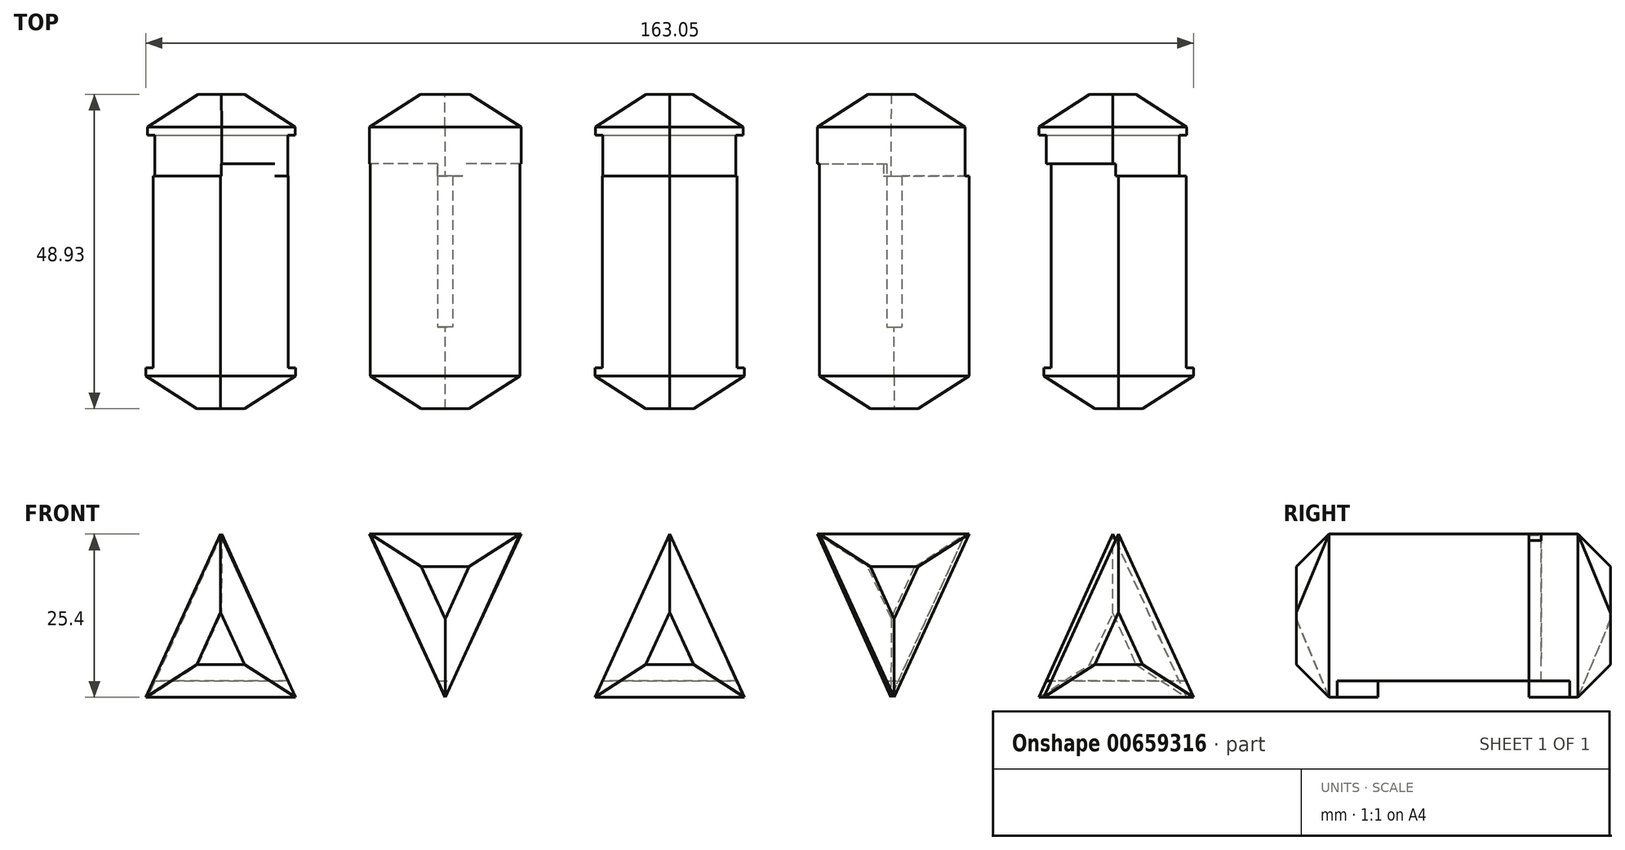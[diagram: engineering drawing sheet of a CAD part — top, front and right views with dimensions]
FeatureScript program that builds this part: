
annotation { "Feature Type Name" : "Feature", "Feature Type Description" : "" }
export const myFeature = defineFeature(function(context is Context, id is Id, definition is map)
    precondition{}
    {
        {
            var Q0;
            Q0=qCreatedBy(makeId("Top.planeOp"),FACE);
            var sketch = newSketch(context, id + "F0", { "sketchPlane" : qUnion([Q0])});
            skLineSegment(sketch, "E0.bottom", {"start": v(-40.34, -18.56) * mm, "end": v(39.23, -18.56) * mm});
            skLineSegment(sketch, "E0.top", {"start": v(-40.34, 17.67) * mm, "end": v(39.23, 17.67) * mm});
            skLineSegment(sketch, "E0.left", {"start": v(-40.34, -18.56) * mm, "end": v(-40.34, 17.67) * mm});
            skLineSegment(sketch, "E0.right", {"start": v(39.23, -18.56) * mm, "end": v(39.23, 17.67) * mm});
            skSolve(sketch);
        }
        {
            var Q0;
            Q0=makeQuery(id+"F0.imprint","IMPRINT",FACE,{"disambiguationData":[TD([[makeQuery(id+"F0.imprint","IMPRINT",EDGE,{"derivedFrom":sQuery(id+"F0.wireOp",EDGE,"E0.bottom")}),1.0]])]});
            extrude(context, id + "F1", {"entities" : qUnion([Q0]), "depth" : 12.7 * mm, "offsetDistance" : 25.4 * mm});
        }
        {
            var Q0;
            Q0=makeQuery(id+"F1.opExtrude","CAP_FACE",FACE,{"disambiguationData":[OSD([sQuery(id+"F0.wireOp",EDGE,"E0.bottom"),sQuery(id+"F0.wireOp",EDGE,"E0.top"),sQuery(id+"F0.wireOp",EDGE,"E0.left"),sQuery(id+"F0.wireOp",EDGE,"E0.right")])],"isStart":true});
            extrude(context, id + "F2", {"entities" : qUnion([Q0]), "operationType" : NewBodyOperationType.ADD, "depth" : 12.7 * mm, "offsetDistance" : 25.4 * mm});
        }
        {
            var Q0;
            {var subQ0=sQuery(id+"F0.wireOp",EDGE,"E0.left");Q0=makeQuery(id+"F2.boolean.opBoolean","MERGE",FACE,{"derivedFrom":[makeQuery(id+"F1.opExtrude","SWEPT_FACE",FACE,{"disambiguationData":[OSD([subQ0])]}),makeQuery(id+"F2.opExtrude","SWEPT_FACE",FACE,{"disambiguationData":[OSD([subQ0])]})]});}
            extrude(context, id + "F3", {"entities" : qUnion([Q0]), "operationType" : NewBodyOperationType.ADD, "depth" : 50.8 * mm, "offsetDistance" : 25.4 * mm});
        }
        {
            var Q0;
            {var subQ0=sQuery(id+"F0.wireOp",EDGE,"E0.right");Q0=makeQuery(id+"F2.boolean.opBoolean","MERGE",FACE,{"derivedFrom":[makeQuery(id+"F1.opExtrude","SWEPT_FACE",FACE,{"disambiguationData":[OSD([subQ0])]}),makeQuery(id+"F2.opExtrude","SWEPT_FACE",FACE,{"disambiguationData":[OSD([subQ0])]})]});}
            extrude(context, id + "F4", {"entities" : qUnion([Q0]), "operationType" : NewBodyOperationType.ADD, "depth" : 50.8 * mm, "offsetDistance" : 25.4 * mm});
        }
        {
            var Q0;
            {var subQ0=sQuery(id+"F0.wireOp",EDGE,"E0.bottom");Q0=makeQuery(id+"F4.boolean.opBoolean","MERGE",FACE,{"derivedFrom":[makeQuery(id+"F3.boolean.opBoolean","MERGE",FACE,{"derivedFrom":[makeQuery(id+"F2.boolean.opBoolean","MERGE",FACE,{"derivedFrom":[makeQuery(id+"F1.opExtrude","SWEPT_FACE",FACE,{"disambiguationData":[OSD([subQ0])]}),makeQuery(id+"F2.opExtrude","SWEPT_FACE",FACE,{"disambiguationData":[OSD([subQ0])]})]}),makeQuery(id+"F3.opExtrude","SWEPT_FACE",FACE,{"disambiguationData":[OSD([subQ0,sQuery(id+"F0.wireOp",EDGE,"E0.left")])]})]}),makeQuery(id+"F4.opExtrude","SWEPT_FACE",FACE,{"disambiguationData":[OSD([subQ0,sQuery(id+"F0.wireOp",EDGE,"E0.right")])]})]});}
            var sketch = newSketch(context, id + "F5", { "sketchPlane" : qUnion([Q0])});
            skLineSegment(sketch, "E1", {"start": v(-0.56, 12.7) * mm, "end": v(11.1, -12.7) * mm});
            skLineSegment(sketch, "E2", {"start": v(-0.56, 12.7) * mm, "end": v(-12.2, -12.7) * mm});
            skLineSegment(sketch, "E3", {"start": v(-12.2, -12.7) * mm, "end": v(-23.85, 12.7) * mm});
            skLineSegment(sketch, "E4", {"start": v(-23.85, 12.7) * mm, "end": v(-35.5, -12.7) * mm});
            skLineSegment(sketch, "E5", {"start": v(11.1, -12.7) * mm, "end": v(22.74, 12.7) * mm});
            skLineSegment(sketch, "E6", {"start": v(22.74, 12.7) * mm, "end": v(34.39, -12.7) * mm});
            skLineSegment(sketch, "E7", {"start": v(34.39, -12.7) * mm, "end": v(46.03, 12.7) * mm});
            skLineSegment(sketch, "E8", {"start": v(46.03, 12.7) * mm, "end": v(57.68, -12.7) * mm});
            skLineSegment(sketch, "E9", {"start": v(57.68, -12.7) * mm, "end": v(69.32, 12.7) * mm});
            skLineSegment(sketch, "E10", {"start": v(69.32, 12.7) * mm, "end": v(80.97, -12.7) * mm});
            skLineSegment(sketch, "E11", {"start": v(80.97, -12.7) * mm, "end": v(90.03, 7.05) * mm});
            skLineSegment(sketch, "E12", {"start": v(-35.5, -12.7) * mm, "end": v(-47.14, 12.7) * mm});
            skLineSegment(sketch, "E13", {"start": v(-47.14, 12.7) * mm, "end": v(-58.79, -12.7) * mm});
            skLineSegment(sketch, "E14", {"start": v(-58.79, -12.7) * mm, "end": v(-70.44, 12.7) * mm});
            skLineSegment(sketch, "E15", {"start": v(-70.44, 12.7) * mm, "end": v(-82.08, -12.7) * mm});
            skLineSegment(sketch, "E16", {"start": v(-82.08, -12.7) * mm, "end": v(-91.14, 7.05) * mm});
            skSolve(sketch);
        }
        {
            var Q0;
            {var subQ0=sQuery(id+"F0.wireOp",EDGE,"E0.top");Q0=makeQuery(id+"F4.boolean.opBoolean","MERGE",FACE,{"derivedFrom":[makeQuery(id+"F3.boolean.opBoolean","MERGE",FACE,{"derivedFrom":[makeQuery(id+"F2.boolean.opBoolean","MERGE",FACE,{"derivedFrom":[makeQuery(id+"F1.opExtrude","SWEPT_FACE",FACE,{"disambiguationData":[OSD([subQ0])]}),makeQuery(id+"F2.opExtrude","SWEPT_FACE",FACE,{"disambiguationData":[OSD([subQ0])]})]}),makeQuery(id+"F3.opExtrude","SWEPT_FACE",FACE,{"disambiguationData":[OSD([subQ0,sQuery(id+"F0.wireOp",EDGE,"E0.left")])]})]}),makeQuery(id+"F4.opExtrude","SWEPT_FACE",FACE,{"disambiguationData":[OSD([subQ0,sQuery(id+"F0.wireOp",EDGE,"E0.right")])]})]});}
            var sketch = newSketch(context, id + "F6", { "sketchPlane" : qUnion([Q0])});
            skLineSegment(sketch, "E17", {"start": v(0.56, 12.7) * mm, "end": v(12.1, -12.7) * mm});
            skLineSegment(sketch, "E18", {"start": v(12.1, -12.7) * mm, "end": v(23.69, 12.7) * mm});
            skLineSegment(sketch, "E19", {"start": v(23.69, 12.7) * mm, "end": v(35.54, -12.7) * mm});
            skLineSegment(sketch, "E20", {"start": v(35.54, -12.7) * mm, "end": v(47.26, 12.7) * mm});
            skLineSegment(sketch, "E21", {"start": v(47.26, 12.7) * mm, "end": v(58.85, -12.7) * mm});
            skLineSegment(sketch, "E22", {"start": v(58.85, -12.7) * mm, "end": v(70.3, 12.7) * mm});
            skLineSegment(sketch, "E23", {"start": v(70.3, 12.7) * mm, "end": v(81.84, -12.7) * mm});
            skLineSegment(sketch, "E24", {"start": v(81.84, -12.7) * mm, "end": v(91.14, 7.45) * mm});
            skLineSegment(sketch, "E25", {"start": v(0.56, 12.7) * mm, "end": v(-10.9, -12.7) * mm});
            skLineSegment(sketch, "E26", {"start": v(-10.9, -12.7) * mm, "end": v(-22.44, 12.7) * mm});
            skLineSegment(sketch, "E27", {"start": v(-22.44, 12.7) * mm, "end": v(-33.89, -12.7) * mm});
            skLineSegment(sketch, "E28", {"start": v(-33.89, -12.7) * mm, "end": v(-45.44, 12.7) * mm});
            skLineSegment(sketch, "E29", {"start": v(-45.44, 12.7) * mm, "end": v(-56.89, -12.7) * mm});
            skLineSegment(sketch, "E30", {"start": v(-56.89, -12.7) * mm, "end": v(-68.44, 12.7) * mm});
            skLineSegment(sketch, "E31", {"start": v(-68.44, 12.7) * mm, "end": v(-79.88, -12.7) * mm});
            skLineSegment(sketch, "E32", {"start": v(-79.88, -12.7) * mm, "end": v(-90.03, 6.92) * mm});
            skSolve(sketch);
        }
        {
            var Q0;
            {var subQ0=sQuery(id+"F5.wireOp",EDGE,"E1");Q0=makeQuery(id+"F5.imprint","IMPRINT",FACE,{"disambiguationData":[TD([[makeQuery(id+"F5.imprint","IMPRINT",EDGE,{"derivedFrom":subQ0}),-1.0]])]});}
            var Q1;
            {var subQ0=sQuery(id+"F5.wireOp",EDGE,"E6");Q1=makeQuery(id+"F5.imprint","IMPRINT",FACE,{"disambiguationData":[TD([[makeQuery(id+"F5.imprint","IMPRINT",EDGE,{"derivedFrom":subQ0}),1.0]])]});}
            var Q2;
            {var subQ0=sQuery(id+"F5.wireOp",EDGE,"E9");Q2=makeQuery(id+"F5.imprint","IMPRINT",FACE,{"disambiguationData":[TD([[makeQuery(id+"F5.imprint","IMPRINT",EDGE,{"derivedFrom":subQ0}),-1.0]])]});}
            var Q3;
            {var subQ0=sQuery(id+"F5.wireOp",EDGE,"E4");Q3=makeQuery(id+"F5.imprint","IMPRINT",FACE,{"disambiguationData":[TD([[makeQuery(id+"F5.imprint","IMPRINT",EDGE,{"derivedFrom":subQ0}),-1.0]])]});}
            var Q4;
            {var subQ0=sQuery(id+"F5.wireOp",EDGE,"E14");Q4=makeQuery(id+"F5.imprint","IMPRINT",FACE,{"disambiguationData":[TD([[makeQuery(id+"F5.imprint","IMPRINT",EDGE,{"derivedFrom":subQ0}),1.0]])]});}
            extrude(context, id + "F7", {"entities" : qUnion([Q0, Q1, Q2, Q3, Q4]), "operationType" : NewBodyOperationType.ADD, "depth" : 6.35 * mm, "offsetDistance" : 25.4 * mm});
        }
        {
            var Q0;
            Q0=makeQuery(id+"F7.opExtrude","CAP_FACE",FACE,{"disambiguationData":[OSD([sQuery(id+"F0.wireOp",EDGE,"E0.bottom"),sQuery(id+"F0.wireOp",EDGE,"E0.left"),sQuery(id+"F0.wireOp",EDGE,"E0.right"),sQuery(id+"F5.wireOp",EDGE,"E14"),sQuery(id+"F5.wireOp",EDGE,"E15")])],"isStart":false});
            var Q1;
            Q1=makeQuery(id+"F7.opExtrude","CAP_FACE",FACE,{"disambiguationData":[OSD([sQuery(id+"F0.wireOp",EDGE,"E0.bottom"),sQuery(id+"F0.wireOp",EDGE,"E0.left"),sQuery(id+"F0.wireOp",EDGE,"E0.right"),sQuery(id+"F5.wireOp",EDGE,"E4"),sQuery(id+"F5.wireOp",EDGE,"E12")])],"isStart":false});
            var Q2;
            Q2=makeQuery(id+"F7.opExtrude","CAP_FACE",FACE,{"disambiguationData":[OSD([sQuery(id+"F0.wireOp",EDGE,"E0.bottom"),sQuery(id+"F0.wireOp",EDGE,"E0.left"),sQuery(id+"F0.wireOp",EDGE,"E0.right"),sQuery(id+"F5.wireOp",EDGE,"E1"),sQuery(id+"F5.wireOp",EDGE,"E2")])],"isStart":false});
            var Q3;
            Q3=makeQuery(id+"F7.opExtrude","CAP_FACE",FACE,{"disambiguationData":[OSD([sQuery(id+"F0.wireOp",EDGE,"E0.bottom"),sQuery(id+"F0.wireOp",EDGE,"E0.left"),sQuery(id+"F0.wireOp",EDGE,"E0.right"),sQuery(id+"F5.wireOp",EDGE,"E6"),sQuery(id+"F5.wireOp",EDGE,"E7")])],"isStart":false});
            var Q4;
            Q4=makeQuery(id+"F7.opExtrude","CAP_FACE",FACE,{"disambiguationData":[OSD([sQuery(id+"F0.wireOp",EDGE,"E0.bottom"),sQuery(id+"F0.wireOp",EDGE,"E0.left"),sQuery(id+"F0.wireOp",EDGE,"E0.right"),sQuery(id+"F5.wireOp",EDGE,"E9"),sQuery(id+"F5.wireOp",EDGE,"E10")])],"isStart":false});
            chamfer(context, id + "F8", {"entities" : qUnion([Q0, Q1, Q2, Q3, Q4]), "width" : 5.08 * mm, "tangentPropagation" : true});
        }
        {
            var Q0;
            {var subQ0=sQuery(id+"F6.wireOp",EDGE,"E17");Q0=makeQuery(id+"F6.imprint","IMPRINT",FACE,{"disambiguationData":[TD([[makeQuery(id+"F6.imprint","IMPRINT",EDGE,{"derivedFrom":subQ0}),-1.0]])]});}
            var Q1;
            {var subQ0=sQuery(id+"F6.wireOp",EDGE,"E19");Q1=makeQuery(id+"F6.imprint","IMPRINT",FACE,{"disambiguationData":[TD([[makeQuery(id+"F6.imprint","IMPRINT",EDGE,{"derivedFrom":subQ0}),1.0]])]});}
            var Q2;
            {var subQ0=sQuery(id+"F6.wireOp",EDGE,"E22");Q2=makeQuery(id+"F6.imprint","IMPRINT",FACE,{"disambiguationData":[TD([[makeQuery(id+"F6.imprint","IMPRINT",EDGE,{"derivedFrom":subQ0}),-1.0]])]});}
            var Q3;
            {var subQ0=sQuery(id+"F6.wireOp",EDGE,"E27");Q3=makeQuery(id+"F6.imprint","IMPRINT",FACE,{"disambiguationData":[TD([[makeQuery(id+"F6.imprint","IMPRINT",EDGE,{"derivedFrom":subQ0}),-1.0]])]});}
            var Q4;
            {var subQ0=sQuery(id+"F6.wireOp",EDGE,"E30");Q4=makeQuery(id+"F6.imprint","IMPRINT",FACE,{"disambiguationData":[TD([[makeQuery(id+"F6.imprint","IMPRINT",EDGE,{"derivedFrom":subQ0}),1.0]])]});}
            extrude(context, id + "F9", {"entities" : qUnion([Q0, Q1, Q2, Q3, Q4]), "operationType" : NewBodyOperationType.ADD, "depth" : 6.35 * mm, "offsetDistance" : 25.4 * mm});
        }
        {
            var Q0;
            Q0=makeQuery(id+"F9.opExtrude","CAP_FACE",FACE,{"disambiguationData":[OSD([sQuery(id+"F0.wireOp",EDGE,"E0.top"),sQuery(id+"F0.wireOp",EDGE,"E0.left"),sQuery(id+"F0.wireOp",EDGE,"E0.right"),sQuery(id+"F6.wireOp",EDGE,"E30"),sQuery(id+"F6.wireOp",EDGE,"E31")])],"isStart":false});
            var Q1;
            Q1=makeQuery(id+"F9.opExtrude","CAP_FACE",FACE,{"disambiguationData":[OSD([sQuery(id+"F0.wireOp",EDGE,"E0.top"),sQuery(id+"F0.wireOp",EDGE,"E0.left"),sQuery(id+"F0.wireOp",EDGE,"E0.right"),sQuery(id+"F6.wireOp",EDGE,"E27"),sQuery(id+"F6.wireOp",EDGE,"E28")])],"isStart":false});
            var Q2;
            Q2=makeQuery(id+"F9.opExtrude","CAP_FACE",FACE,{"disambiguationData":[OSD([sQuery(id+"F0.wireOp",EDGE,"E0.top"),sQuery(id+"F0.wireOp",EDGE,"E0.left"),sQuery(id+"F0.wireOp",EDGE,"E0.right"),sQuery(id+"F6.wireOp",EDGE,"E17"),sQuery(id+"F6.wireOp",EDGE,"E25")])],"isStart":false});
            var Q3;
            Q3=makeQuery(id+"F9.opExtrude","CAP_FACE",FACE,{"disambiguationData":[OSD([sQuery(id+"F0.wireOp",EDGE,"E0.top"),sQuery(id+"F0.wireOp",EDGE,"E0.left"),sQuery(id+"F0.wireOp",EDGE,"E0.right"),sQuery(id+"F6.wireOp",EDGE,"E19"),sQuery(id+"F6.wireOp",EDGE,"E20")])],"isStart":false});
            var Q4;
            Q4=makeQuery(id+"F9.opExtrude","CAP_FACE",FACE,{"disambiguationData":[OSD([sQuery(id+"F0.wireOp",EDGE,"E0.top"),sQuery(id+"F0.wireOp",EDGE,"E0.left"),sQuery(id+"F0.wireOp",EDGE,"E0.right"),sQuery(id+"F6.wireOp",EDGE,"E22"),sQuery(id+"F6.wireOp",EDGE,"E23")])],"isStart":false});
            chamfer(context, id + "F10", {"entities" : qUnion([Q0, Q1, Q2, Q3, Q4]), "width" : 5.08 * mm, "tangentPropagation" : true});
        }
        {
            var Q0;
            {var subQ0=sQuery(id+"F0.wireOp",EDGE,"E0.right");var subQ1=sQuery(id+"F0.wireOp",EDGE,"E0.left");var subQ2=sQuery(id+"F0.wireOp",EDGE,"E0.bottom");var subQ3=makeQuery(id+"F3.opExtrude","SWEPT_FACE",FACE,{"disambiguationData":[OSD([subQ2,subQ1])]});var subQ4=sQuery(id+"F5.wireOp",EDGE,"E5");var subQ5=sQuery(id+"F5.wireOp",EDGE,"E1");var subQ6=makeQuery(id+"F4.boolean.opBoolean","MERGE",EDGE,{"derivedFrom":[makeQuery(id+"F3.boolean.opBoolean","MERGE",EDGE,{"derivedFrom":[makeQuery(id+"F2.opExtrude","CAP_EDGE",EDGE,{"disambiguationData":[OSD([subQ2])],"isStart":false}),makeQuery(id+"F3.opExtrude","SWEPT_EDGE",EDGE,{"disambiguationData":[OSD([subQ2,subQ1]),TDD([makeQuery(id+"F2.opExtrude","CAP_VERTEX",VERTEX,{"disambiguationData":[OSD([subQ2,subQ1])],"isStart":false})])]})]}),makeQuery(id+"F4.opExtrude","SWEPT_EDGE",EDGE,{"disambiguationData":[OSD([subQ2,subQ0]),TDD([makeQuery(id+"F2.opExtrude","CAP_VERTEX",VERTEX,{"disambiguationData":[OSD([subQ2,subQ0])],"isStart":false})])]})]});var subQ7=sQuery(id+"F5.wireOp",EDGE,"E3");var subQ8=sQuery(id+"F5.wireOp",EDGE,"E2");var subQ9=makeQuery(id+"F4.boolean.opBoolean","MERGE",EDGE,{"derivedFrom":[makeQuery(id+"F3.boolean.opBoolean","MERGE",EDGE,{"derivedFrom":[makeQuery(id+"F1.opExtrude","CAP_EDGE",EDGE,{"disambiguationData":[OSD([subQ2])],"isStart":false}),makeQuery(id+"F3.opExtrude","SWEPT_EDGE",EDGE,{"disambiguationData":[OSD([subQ2,subQ1]),TDD([makeQuery(id+"F1.opExtrude","CAP_VERTEX",VERTEX,{"disambiguationData":[OSD([subQ2,subQ1])],"isStart":false})])]})]}),makeQuery(id+"F4.opExtrude","SWEPT_EDGE",EDGE,{"disambiguationData":[OSD([subQ2,subQ0]),TDD([makeQuery(id+"F1.opExtrude","CAP_VERTEX",VERTEX,{"disambiguationData":[OSD([subQ2,subQ0])],"isStart":false})])]})]});var subQ10=sQuery(id+"F5.wireOp",EDGE,"E13");var subQ11=sQuery(id+"F5.wireOp",EDGE,"E6");var subQ12=sQuery(id+"F5.wireOp",EDGE,"E8");var subQ13=sQuery(id+"F5.wireOp",EDGE,"E7");var subQ14=makeQuery(id+"F1.opExtrude","SWEPT_FACE",FACE,{"disambiguationData":[OSD([subQ2])]});var subQ15=makeQuery(id+"F4.opExtrude","SWEPT_FACE",FACE,{"disambiguationData":[OSD([subQ2,subQ0])]});var subQ16=sQuery(id+"F0.wireOp",EDGE,"E0.top");var subQ17=makeQuery(id+"F2.opExtrude","SWEPT_FACE",FACE,{"disambiguationData":[OSD([subQ2])]});Q0=makeQuery(id+"F7.boolean.opBoolean","SPLIT",FACE,{"disambiguationData":[TD([subQ14,makeQuery(id+"F1.opExtrude","CAP_FACE",FACE,{"disambiguationData":[OSD([subQ2,subQ16,subQ1,subQ0])],"isStart":false}),subQ17,makeQuery(id+"F2.opExtrude","CAP_FACE",FACE,{"disambiguationData":[OSD([subQ2,subQ16,subQ1,subQ0])],"isStart":false}),makeQuery(id+"F3.opExtrude","SWEPT_FACE",FACE,{"disambiguationData":[OSD([subQ1]),TDD([makeQuery(id+"F1.opExtrude","CAP_EDGE",EDGE,{"disambiguationData":[OSD([subQ1])],"isStart":false})])]}),makeQuery(id+"F3.opExtrude","SWEPT_FACE",FACE,{"disambiguationData":[OSD([subQ1]),TDD([makeQuery(id+"F2.opExtrude","CAP_EDGE",EDGE,{"disambiguationData":[OSD([subQ1])],"isStart":false})])]}),subQ3,makeQuery(id+"F4.opExtrude","SWEPT_FACE",FACE,{"disambiguationData":[OSD([subQ0]),TDD([makeQuery(id+"F1.opExtrude","CAP_EDGE",EDGE,{"disambiguationData":[OSD([subQ0])],"isStart":false})])]}),makeQuery(id+"F4.opExtrude","SWEPT_FACE",FACE,{"disambiguationData":[OSD([subQ0]),TDD([makeQuery(id+"F2.opExtrude","CAP_EDGE",EDGE,{"disambiguationData":[OSD([subQ0])],"isStart":false})])]}),subQ15,makeQuery(id+"F7.opExtrude","SWEPT_FACE",FACE,{"disambiguationData":[OSD([subQ5])]}),makeQuery(id+"F7.opExtrude","SWEPT_FACE",FACE,{"disambiguationData":[OSD([subQ8])]}),makeQuery(id+"F7.opExtrude","SWEPT_FACE",FACE,{"disambiguationData":[OSD([subQ11])]}),makeQuery(id+"F7.opExtrude","SWEPT_FACE",FACE,{"disambiguationData":[OSD([subQ13])]}),makeQuery(id+"F7.opExtrude","SWEPT_FACE",FACE,{"disambiguationData":[OSD([subQ2,subQ1,subQ0]),TDD([makeQuery(id+"F5.imprint","IMPRINT",EDGE,{"disambiguationData":[TD([[makeQuery(id+"F5.imprint","INTERSECT",VERTEX,{"derivedFrom":[subQ9,subQ7,sQuery(id+"F5.wireOp",EDGE,"E4")]}),1.0]])],"derivedFrom":subQ9})])]}),makeQuery(id+"F7.opExtrude","SWEPT_FACE",FACE,{"disambiguationData":[OSD([subQ2,subQ1,subQ0]),TDD([makeQuery(id+"F5.imprint","IMPRINT",EDGE,{"disambiguationData":[TD([[makeQuery(id+"F5.imprint","INTERSECT",VERTEX,{"derivedFrom":[subQ9,subQ4,subQ11]}),-1.0]])],"derivedFrom":subQ9})])]}),makeQuery(id+"F7.opExtrude","SWEPT_FACE",FACE,{"disambiguationData":[OSD([subQ2,subQ1,subQ0]),TDD([makeQuery(id+"F5.imprint","IMPRINT",EDGE,{"disambiguationData":[TD([[makeQuery(id+"F5.imprint","INTERSECT",VERTEX,{"derivedFrom":[subQ6,subQ5,subQ4]}),1.0]])],"derivedFrom":subQ6})])]}),makeQuery(id+"F7.opExtrude","SWEPT_FACE",FACE,{"disambiguationData":[OSD([subQ2,subQ1,subQ0]),TDD([makeQuery(id+"F5.imprint","IMPRINT",EDGE,{"disambiguationData":[TD([[makeQuery(id+"F5.imprint","INTERSECT",VERTEX,{"derivedFrom":[subQ6,subQ12,sQuery(id+"F5.wireOp",EDGE,"E9")]}),-1.0]])],"derivedFrom":subQ6})])]}),makeQuery(id+"F7.opExtrude","SWEPT_FACE",FACE,{"disambiguationData":[OSD([subQ2,subQ1,subQ0]),TDD([makeQuery(id+"F5.imprint","IMPRINT",EDGE,{"disambiguationData":[TD([[makeQuery(id+"F5.imprint","INTERSECT",VERTEX,{"derivedFrom":[subQ6,subQ10,sQuery(id+"F5.wireOp",EDGE,"E14")]}),1.0]])],"derivedFrom":subQ6})])]})])],"derivedFrom":makeQuery(id+"F4.boolean.opBoolean","MERGE",FACE,{"derivedFrom":[makeQuery(id+"F3.boolean.opBoolean","MERGE",FACE,{"derivedFrom":[makeQuery(id+"F2.boolean.opBoolean","MERGE",FACE,{"derivedFrom":[subQ14,subQ17]}),subQ3]}),subQ15]})});}
            var Q1;
            {var subQ0=sQuery(id+"F0.wireOp",EDGE,"E0.right");var subQ1=sQuery(id+"F0.wireOp",EDGE,"E0.left");var subQ2=sQuery(id+"F0.wireOp",EDGE,"E0.bottom");var subQ3=makeQuery(id+"F3.opExtrude","SWEPT_FACE",FACE,{"disambiguationData":[OSD([subQ2,subQ1])]});var subQ4=sQuery(id+"F5.wireOp",EDGE,"E5");var subQ5=makeQuery(id+"F4.boolean.opBoolean","MERGE",EDGE,{"derivedFrom":[makeQuery(id+"F3.boolean.opBoolean","MERGE",EDGE,{"derivedFrom":[makeQuery(id+"F2.opExtrude","CAP_EDGE",EDGE,{"disambiguationData":[OSD([subQ2])],"isStart":false}),makeQuery(id+"F3.opExtrude","SWEPT_EDGE",EDGE,{"disambiguationData":[OSD([subQ2,subQ1]),TDD([makeQuery(id+"F2.opExtrude","CAP_VERTEX",VERTEX,{"disambiguationData":[OSD([subQ2,subQ1])],"isStart":false})])]})]}),makeQuery(id+"F4.opExtrude","SWEPT_EDGE",EDGE,{"disambiguationData":[OSD([subQ2,subQ0]),TDD([makeQuery(id+"F2.opExtrude","CAP_VERTEX",VERTEX,{"disambiguationData":[OSD([subQ2,subQ0])],"isStart":false})])]})]});var subQ6=sQuery(id+"F5.wireOp",EDGE,"E3");var subQ7=makeQuery(id+"F4.boolean.opBoolean","MERGE",EDGE,{"derivedFrom":[makeQuery(id+"F3.boolean.opBoolean","MERGE",EDGE,{"derivedFrom":[makeQuery(id+"F1.opExtrude","CAP_EDGE",EDGE,{"disambiguationData":[OSD([subQ2])],"isStart":false}),makeQuery(id+"F3.opExtrude","SWEPT_EDGE",EDGE,{"disambiguationData":[OSD([subQ2,subQ1]),TDD([makeQuery(id+"F1.opExtrude","CAP_VERTEX",VERTEX,{"disambiguationData":[OSD([subQ2,subQ1])],"isStart":false})])]})]}),makeQuery(id+"F4.opExtrude","SWEPT_EDGE",EDGE,{"disambiguationData":[OSD([subQ2,subQ0]),TDD([makeQuery(id+"F1.opExtrude","CAP_VERTEX",VERTEX,{"disambiguationData":[OSD([subQ2,subQ0])],"isStart":false})])]})]});var subQ8=sQuery(id+"F5.wireOp",EDGE,"E13");var subQ9=sQuery(id+"F5.wireOp",EDGE,"E6");var subQ10=sQuery(id+"F5.wireOp",EDGE,"E8");var subQ11=sQuery(id+"F5.wireOp",EDGE,"E7");var subQ12=makeQuery(id+"F1.opExtrude","SWEPT_FACE",FACE,{"disambiguationData":[OSD([subQ2])]});var subQ13=makeQuery(id+"F4.opExtrude","SWEPT_FACE",FACE,{"disambiguationData":[OSD([subQ2,subQ0])]});var subQ14=sQuery(id+"F0.wireOp",EDGE,"E0.top");var subQ15=makeQuery(id+"F2.opExtrude","SWEPT_FACE",FACE,{"disambiguationData":[OSD([subQ2])]});var subQ16=sQuery(id+"F5.wireOp",EDGE,"E9");var subQ17=sQuery(id+"F5.wireOp",EDGE,"E10");Q1=makeQuery(id+"F7.boolean.opBoolean","SPLIT",FACE,{"disambiguationData":[TD([subQ12,makeQuery(id+"F1.opExtrude","CAP_FACE",FACE,{"disambiguationData":[OSD([subQ2,subQ14,subQ1,subQ0])],"isStart":false}),subQ15,makeQuery(id+"F2.opExtrude","CAP_FACE",FACE,{"disambiguationData":[OSD([subQ2,subQ14,subQ1,subQ0])],"isStart":false}),makeQuery(id+"F3.opExtrude","SWEPT_FACE",FACE,{"disambiguationData":[OSD([subQ1]),TDD([makeQuery(id+"F1.opExtrude","CAP_EDGE",EDGE,{"disambiguationData":[OSD([subQ1])],"isStart":false})])]}),makeQuery(id+"F3.opExtrude","SWEPT_FACE",FACE,{"disambiguationData":[OSD([subQ1]),TDD([makeQuery(id+"F2.opExtrude","CAP_EDGE",EDGE,{"disambiguationData":[OSD([subQ1])],"isStart":false})])]}),subQ3,makeQuery(id+"F4.opExtrude","SWEPT_FACE",FACE,{"disambiguationData":[OSD([subQ0]),TDD([makeQuery(id+"F1.opExtrude","CAP_EDGE",EDGE,{"disambiguationData":[OSD([subQ0])],"isStart":false})])]}),makeQuery(id+"F4.opExtrude","SWEPT_FACE",FACE,{"disambiguationData":[OSD([subQ0]),TDD([makeQuery(id+"F2.opExtrude","CAP_EDGE",EDGE,{"disambiguationData":[OSD([subQ0])],"isStart":false})])]}),subQ13,makeQuery(id+"F7.opExtrude","SWEPT_FACE",FACE,{"disambiguationData":[OSD([subQ9])]}),makeQuery(id+"F7.opExtrude","SWEPT_FACE",FACE,{"disambiguationData":[OSD([subQ11])]}),makeQuery(id+"F7.opExtrude","SWEPT_FACE",FACE,{"disambiguationData":[OSD([subQ16])]}),makeQuery(id+"F7.opExtrude","SWEPT_FACE",FACE,{"disambiguationData":[OSD([subQ17])]}),makeQuery(id+"F7.opExtrude","SWEPT_FACE",FACE,{"disambiguationData":[OSD([subQ2,subQ1,subQ0]),TDD([makeQuery(id+"F5.imprint","IMPRINT",EDGE,{"disambiguationData":[TD([[makeQuery(id+"F5.imprint","INTERSECT",VERTEX,{"derivedFrom":[subQ7,subQ6,sQuery(id+"F5.wireOp",EDGE,"E4")]}),1.0]])],"derivedFrom":subQ7})])]}),makeQuery(id+"F7.opExtrude","SWEPT_FACE",FACE,{"disambiguationData":[OSD([subQ2,subQ1,subQ0]),TDD([makeQuery(id+"F5.imprint","IMPRINT",EDGE,{"disambiguationData":[TD([[makeQuery(id+"F5.imprint","INTERSECT",VERTEX,{"derivedFrom":[subQ7,subQ4,subQ9]}),-1.0]])],"derivedFrom":subQ7})])]}),makeQuery(id+"F7.opExtrude","SWEPT_FACE",FACE,{"disambiguationData":[OSD([subQ2,subQ1,subQ0]),TDD([makeQuery(id+"F5.imprint","IMPRINT",EDGE,{"disambiguationData":[TD([[makeQuery(id+"F5.imprint","INTERSECT",VERTEX,{"derivedFrom":[subQ5,sQuery(id+"F5.wireOp",EDGE,"E1"),subQ4]}),1.0]])],"derivedFrom":subQ5})])]}),makeQuery(id+"F7.opExtrude","SWEPT_FACE",FACE,{"disambiguationData":[OSD([subQ2,subQ1,subQ0]),TDD([makeQuery(id+"F5.imprint","IMPRINT",EDGE,{"disambiguationData":[TD([[makeQuery(id+"F5.imprint","INTERSECT",VERTEX,{"derivedFrom":[subQ5,subQ10,subQ16]}),-1.0]])],"derivedFrom":subQ5})])]}),makeQuery(id+"F7.opExtrude","SWEPT_FACE",FACE,{"disambiguationData":[OSD([subQ2,subQ1,subQ0]),TDD([makeQuery(id+"F5.imprint","IMPRINT",EDGE,{"disambiguationData":[TD([[makeQuery(id+"F5.imprint","INTERSECT",VERTEX,{"derivedFrom":[subQ5,subQ8,sQuery(id+"F5.wireOp",EDGE,"E14")]}),1.0]])],"derivedFrom":subQ5})])]})])],"derivedFrom":makeQuery(id+"F4.boolean.opBoolean","MERGE",FACE,{"derivedFrom":[makeQuery(id+"F3.boolean.opBoolean","MERGE",FACE,{"derivedFrom":[makeQuery(id+"F2.boolean.opBoolean","MERGE",FACE,{"derivedFrom":[subQ12,subQ15]}),subQ3]}),subQ13]})});}
            var Q2;
            {var subQ0=sQuery(id+"F0.wireOp",EDGE,"E0.right");var subQ1=sQuery(id+"F0.wireOp",EDGE,"E0.left");var subQ2=sQuery(id+"F0.wireOp",EDGE,"E0.bottom");var subQ3=makeQuery(id+"F3.opExtrude","SWEPT_FACE",FACE,{"disambiguationData":[OSD([subQ2,subQ1])]});var subQ4=sQuery(id+"F5.wireOp",EDGE,"E5");var subQ5=makeQuery(id+"F4.boolean.opBoolean","MERGE",EDGE,{"derivedFrom":[makeQuery(id+"F3.boolean.opBoolean","MERGE",EDGE,{"derivedFrom":[makeQuery(id+"F2.opExtrude","CAP_EDGE",EDGE,{"disambiguationData":[OSD([subQ2])],"isStart":false}),makeQuery(id+"F3.opExtrude","SWEPT_EDGE",EDGE,{"disambiguationData":[OSD([subQ2,subQ1]),TDD([makeQuery(id+"F2.opExtrude","CAP_VERTEX",VERTEX,{"disambiguationData":[OSD([subQ2,subQ1])],"isStart":false})])]})]}),makeQuery(id+"F4.opExtrude","SWEPT_EDGE",EDGE,{"disambiguationData":[OSD([subQ2,subQ0]),TDD([makeQuery(id+"F2.opExtrude","CAP_VERTEX",VERTEX,{"disambiguationData":[OSD([subQ2,subQ0])],"isStart":false})])]})]});var subQ6=sQuery(id+"F5.wireOp",EDGE,"E3");var subQ7=makeQuery(id+"F4.boolean.opBoolean","MERGE",EDGE,{"derivedFrom":[makeQuery(id+"F3.boolean.opBoolean","MERGE",EDGE,{"derivedFrom":[makeQuery(id+"F1.opExtrude","CAP_EDGE",EDGE,{"disambiguationData":[OSD([subQ2])],"isStart":false}),makeQuery(id+"F3.opExtrude","SWEPT_EDGE",EDGE,{"disambiguationData":[OSD([subQ2,subQ1]),TDD([makeQuery(id+"F1.opExtrude","CAP_VERTEX",VERTEX,{"disambiguationData":[OSD([subQ2,subQ1])],"isStart":false})])]})]}),makeQuery(id+"F4.opExtrude","SWEPT_EDGE",EDGE,{"disambiguationData":[OSD([subQ2,subQ0]),TDD([makeQuery(id+"F1.opExtrude","CAP_VERTEX",VERTEX,{"disambiguationData":[OSD([subQ2,subQ0])],"isStart":false})])]})]});var subQ8=sQuery(id+"F5.wireOp",EDGE,"E13");var subQ9=sQuery(id+"F5.wireOp",EDGE,"E8");var subQ10=makeQuery(id+"F1.opExtrude","SWEPT_FACE",FACE,{"disambiguationData":[OSD([subQ2])]});var subQ11=makeQuery(id+"F4.opExtrude","SWEPT_FACE",FACE,{"disambiguationData":[OSD([subQ2,subQ0])]});var subQ12=sQuery(id+"F0.wireOp",EDGE,"E0.top");var subQ13=makeQuery(id+"F2.opExtrude","SWEPT_FACE",FACE,{"disambiguationData":[OSD([subQ2])]});var subQ14=sQuery(id+"F5.wireOp",EDGE,"E9");var subQ15=sQuery(id+"F5.wireOp",EDGE,"E10");Q2=makeQuery(id+"F7.boolean.opBoolean","SPLIT",FACE,{"disambiguationData":[TD([subQ10,makeQuery(id+"F1.opExtrude","CAP_FACE",FACE,{"disambiguationData":[OSD([subQ2,subQ12,subQ1,subQ0])],"isStart":false}),subQ13,makeQuery(id+"F2.opExtrude","CAP_FACE",FACE,{"disambiguationData":[OSD([subQ2,subQ12,subQ1,subQ0])],"isStart":false}),makeQuery(id+"F3.opExtrude","SWEPT_FACE",FACE,{"disambiguationData":[OSD([subQ1]),TDD([makeQuery(id+"F1.opExtrude","CAP_EDGE",EDGE,{"disambiguationData":[OSD([subQ1])],"isStart":false})])]}),makeQuery(id+"F3.opExtrude","SWEPT_FACE",FACE,{"disambiguationData":[OSD([subQ1]),TDD([makeQuery(id+"F2.opExtrude","CAP_EDGE",EDGE,{"disambiguationData":[OSD([subQ1])],"isStart":false})])]}),subQ3,makeQuery(id+"F4.opExtrude","SWEPT_FACE",FACE,{"disambiguationData":[OSD([subQ0]),TDD([makeQuery(id+"F1.opExtrude","CAP_EDGE",EDGE,{"disambiguationData":[OSD([subQ0])],"isStart":false})])]}),makeQuery(id+"F4.opExtrude","SWEPT_FACE",FACE,{"disambiguationData":[OSD([subQ0]),TDD([makeQuery(id+"F2.opExtrude","CAP_EDGE",EDGE,{"disambiguationData":[OSD([subQ0])],"isStart":false})])]}),subQ11,makeQuery(id+"F4.opExtrude","CAP_FACE",FACE,{"disambiguationData":[OSD([subQ0])],"isStart":false}),makeQuery(id+"F7.opExtrude","SWEPT_FACE",FACE,{"disambiguationData":[OSD([subQ14])]}),makeQuery(id+"F7.opExtrude","SWEPT_FACE",FACE,{"disambiguationData":[OSD([subQ15])]}),makeQuery(id+"F7.opExtrude","SWEPT_FACE",FACE,{"disambiguationData":[OSD([subQ2,subQ1,subQ0]),TDD([makeQuery(id+"F5.imprint","IMPRINT",EDGE,{"disambiguationData":[TD([[makeQuery(id+"F5.imprint","INTERSECT",VERTEX,{"derivedFrom":[subQ7,subQ6,sQuery(id+"F5.wireOp",EDGE,"E4")]}),1.0]])],"derivedFrom":subQ7})])]}),makeQuery(id+"F7.opExtrude","SWEPT_FACE",FACE,{"disambiguationData":[OSD([subQ2,subQ1,subQ0]),TDD([makeQuery(id+"F5.imprint","IMPRINT",EDGE,{"disambiguationData":[TD([[makeQuery(id+"F5.imprint","INTERSECT",VERTEX,{"derivedFrom":[subQ7,subQ4,sQuery(id+"F5.wireOp",EDGE,"E6")]}),-1.0]])],"derivedFrom":subQ7})])]}),makeQuery(id+"F7.opExtrude","SWEPT_FACE",FACE,{"disambiguationData":[OSD([subQ2,subQ1,subQ0]),TDD([makeQuery(id+"F5.imprint","IMPRINT",EDGE,{"disambiguationData":[TD([[makeQuery(id+"F5.imprint","INTERSECT",VERTEX,{"derivedFrom":[subQ5,sQuery(id+"F5.wireOp",EDGE,"E1"),subQ4]}),1.0]])],"derivedFrom":subQ5})])]}),makeQuery(id+"F7.opExtrude","SWEPT_FACE",FACE,{"disambiguationData":[OSD([subQ2,subQ1,subQ0]),TDD([makeQuery(id+"F5.imprint","IMPRINT",EDGE,{"disambiguationData":[TD([[makeQuery(id+"F5.imprint","INTERSECT",VERTEX,{"derivedFrom":[subQ5,subQ9,subQ14]}),-1.0]])],"derivedFrom":subQ5})])]}),makeQuery(id+"F7.opExtrude","SWEPT_FACE",FACE,{"disambiguationData":[OSD([subQ2,subQ1,subQ0]),TDD([makeQuery(id+"F5.imprint","IMPRINT",EDGE,{"disambiguationData":[TD([[makeQuery(id+"F5.imprint","INTERSECT",VERTEX,{"derivedFrom":[subQ5,subQ8,sQuery(id+"F5.wireOp",EDGE,"E14")]}),1.0]])],"derivedFrom":subQ5})])]})])],"derivedFrom":makeQuery(id+"F4.boolean.opBoolean","MERGE",FACE,{"derivedFrom":[makeQuery(id+"F3.boolean.opBoolean","MERGE",FACE,{"derivedFrom":[makeQuery(id+"F2.boolean.opBoolean","MERGE",FACE,{"derivedFrom":[subQ10,subQ13]}),subQ3]}),subQ11]})});}
            var Q3;
            {var subQ0=sQuery(id+"F0.wireOp",EDGE,"E0.right");var subQ1=sQuery(id+"F5.wireOp",EDGE,"E12");var subQ2=sQuery(id+"F0.wireOp",EDGE,"E0.left");var subQ3=sQuery(id+"F0.wireOp",EDGE,"E0.bottom");var subQ4=makeQuery(id+"F3.opExtrude","SWEPT_FACE",FACE,{"disambiguationData":[OSD([subQ3,subQ2])]});var subQ5=sQuery(id+"F5.wireOp",EDGE,"E5");var subQ6=sQuery(id+"F5.wireOp",EDGE,"E1");var subQ7=makeQuery(id+"F4.boolean.opBoolean","MERGE",EDGE,{"derivedFrom":[makeQuery(id+"F3.boolean.opBoolean","MERGE",EDGE,{"derivedFrom":[makeQuery(id+"F2.opExtrude","CAP_EDGE",EDGE,{"disambiguationData":[OSD([subQ3])],"isStart":false}),makeQuery(id+"F3.opExtrude","SWEPT_EDGE",EDGE,{"disambiguationData":[OSD([subQ3,subQ2]),TDD([makeQuery(id+"F2.opExtrude","CAP_VERTEX",VERTEX,{"disambiguationData":[OSD([subQ3,subQ2])],"isStart":false})])]})]}),makeQuery(id+"F4.opExtrude","SWEPT_EDGE",EDGE,{"disambiguationData":[OSD([subQ3,subQ0]),TDD([makeQuery(id+"F2.opExtrude","CAP_VERTEX",VERTEX,{"disambiguationData":[OSD([subQ3,subQ0])],"isStart":false})])]})]});var subQ8=sQuery(id+"F5.wireOp",EDGE,"E3");var subQ9=sQuery(id+"F5.wireOp",EDGE,"E2");var subQ10=sQuery(id+"F5.wireOp",EDGE,"E4");var subQ11=makeQuery(id+"F4.boolean.opBoolean","MERGE",EDGE,{"derivedFrom":[makeQuery(id+"F3.boolean.opBoolean","MERGE",EDGE,{"derivedFrom":[makeQuery(id+"F1.opExtrude","CAP_EDGE",EDGE,{"disambiguationData":[OSD([subQ3])],"isStart":false}),makeQuery(id+"F3.opExtrude","SWEPT_EDGE",EDGE,{"disambiguationData":[OSD([subQ3,subQ2]),TDD([makeQuery(id+"F1.opExtrude","CAP_VERTEX",VERTEX,{"disambiguationData":[OSD([subQ3,subQ2])],"isStart":false})])]})]}),makeQuery(id+"F4.opExtrude","SWEPT_EDGE",EDGE,{"disambiguationData":[OSD([subQ3,subQ0]),TDD([makeQuery(id+"F1.opExtrude","CAP_VERTEX",VERTEX,{"disambiguationData":[OSD([subQ3,subQ0])],"isStart":false})])]})]});var subQ12=sQuery(id+"F5.wireOp",EDGE,"E13");var subQ13=sQuery(id+"F5.wireOp",EDGE,"E8");var subQ14=makeQuery(id+"F1.opExtrude","SWEPT_FACE",FACE,{"disambiguationData":[OSD([subQ3])]});var subQ15=makeQuery(id+"F4.opExtrude","SWEPT_FACE",FACE,{"disambiguationData":[OSD([subQ3,subQ0])]});var subQ16=sQuery(id+"F0.wireOp",EDGE,"E0.top");var subQ17=makeQuery(id+"F2.opExtrude","SWEPT_FACE",FACE,{"disambiguationData":[OSD([subQ3])]});Q3=makeQuery(id+"F7.boolean.opBoolean","SPLIT",FACE,{"disambiguationData":[TD([subQ14,makeQuery(id+"F1.opExtrude","CAP_FACE",FACE,{"disambiguationData":[OSD([subQ3,subQ16,subQ2,subQ0])],"isStart":false}),subQ17,makeQuery(id+"F2.opExtrude","CAP_FACE",FACE,{"disambiguationData":[OSD([subQ3,subQ16,subQ2,subQ0])],"isStart":false}),makeQuery(id+"F3.opExtrude","SWEPT_FACE",FACE,{"disambiguationData":[OSD([subQ2]),TDD([makeQuery(id+"F1.opExtrude","CAP_EDGE",EDGE,{"disambiguationData":[OSD([subQ2])],"isStart":false})])]}),makeQuery(id+"F3.opExtrude","SWEPT_FACE",FACE,{"disambiguationData":[OSD([subQ2]),TDD([makeQuery(id+"F2.opExtrude","CAP_EDGE",EDGE,{"disambiguationData":[OSD([subQ2])],"isStart":false})])]}),subQ4,makeQuery(id+"F4.opExtrude","SWEPT_FACE",FACE,{"disambiguationData":[OSD([subQ0]),TDD([makeQuery(id+"F1.opExtrude","CAP_EDGE",EDGE,{"disambiguationData":[OSD([subQ0])],"isStart":false})])]}),makeQuery(id+"F4.opExtrude","SWEPT_FACE",FACE,{"disambiguationData":[OSD([subQ0]),TDD([makeQuery(id+"F2.opExtrude","CAP_EDGE",EDGE,{"disambiguationData":[OSD([subQ0])],"isStart":false})])]}),subQ15,makeQuery(id+"F7.opExtrude","SWEPT_FACE",FACE,{"disambiguationData":[OSD([subQ6])]}),makeQuery(id+"F7.opExtrude","SWEPT_FACE",FACE,{"disambiguationData":[OSD([subQ9])]}),makeQuery(id+"F7.opExtrude","SWEPT_FACE",FACE,{"disambiguationData":[OSD([subQ10])]}),makeQuery(id+"F7.opExtrude","SWEPT_FACE",FACE,{"disambiguationData":[OSD([subQ1])]}),makeQuery(id+"F7.opExtrude","SWEPT_FACE",FACE,{"disambiguationData":[OSD([subQ3,subQ2,subQ0]),TDD([makeQuery(id+"F5.imprint","IMPRINT",EDGE,{"disambiguationData":[TD([[makeQuery(id+"F5.imprint","INTERSECT",VERTEX,{"derivedFrom":[subQ11,subQ8,subQ10]}),1.0]])],"derivedFrom":subQ11})])]}),makeQuery(id+"F7.opExtrude","SWEPT_FACE",FACE,{"disambiguationData":[OSD([subQ3,subQ2,subQ0]),TDD([makeQuery(id+"F5.imprint","IMPRINT",EDGE,{"disambiguationData":[TD([[makeQuery(id+"F5.imprint","INTERSECT",VERTEX,{"derivedFrom":[subQ11,subQ5,sQuery(id+"F5.wireOp",EDGE,"E6")]}),-1.0]])],"derivedFrom":subQ11})])]}),makeQuery(id+"F7.opExtrude","SWEPT_FACE",FACE,{"disambiguationData":[OSD([subQ3,subQ2,subQ0]),TDD([makeQuery(id+"F5.imprint","IMPRINT",EDGE,{"disambiguationData":[TD([[makeQuery(id+"F5.imprint","INTERSECT",VERTEX,{"derivedFrom":[subQ7,subQ6,subQ5]}),1.0]])],"derivedFrom":subQ7})])]}),makeQuery(id+"F7.opExtrude","SWEPT_FACE",FACE,{"disambiguationData":[OSD([subQ3,subQ2,subQ0]),TDD([makeQuery(id+"F5.imprint","IMPRINT",EDGE,{"disambiguationData":[TD([[makeQuery(id+"F5.imprint","INTERSECT",VERTEX,{"derivedFrom":[subQ7,subQ13,sQuery(id+"F5.wireOp",EDGE,"E9")]}),-1.0]])],"derivedFrom":subQ7})])]}),makeQuery(id+"F7.opExtrude","SWEPT_FACE",FACE,{"disambiguationData":[OSD([subQ3,subQ2,subQ0]),TDD([makeQuery(id+"F5.imprint","IMPRINT",EDGE,{"disambiguationData":[TD([[makeQuery(id+"F5.imprint","INTERSECT",VERTEX,{"derivedFrom":[subQ7,subQ12,sQuery(id+"F5.wireOp",EDGE,"E14")]}),1.0]])],"derivedFrom":subQ7})])]})])],"derivedFrom":makeQuery(id+"F4.boolean.opBoolean","MERGE",FACE,{"derivedFrom":[makeQuery(id+"F3.boolean.opBoolean","MERGE",FACE,{"derivedFrom":[makeQuery(id+"F2.boolean.opBoolean","MERGE",FACE,{"derivedFrom":[subQ14,subQ17]}),subQ4]}),subQ15]})});}
            var Q4;
            {var subQ0=sQuery(id+"F0.wireOp",EDGE,"E0.right");var subQ1=sQuery(id+"F5.wireOp",EDGE,"E14");var subQ2=sQuery(id+"F5.wireOp",EDGE,"E12");var subQ3=sQuery(id+"F0.wireOp",EDGE,"E0.left");var subQ4=sQuery(id+"F0.wireOp",EDGE,"E0.bottom");var subQ5=makeQuery(id+"F3.opExtrude","SWEPT_FACE",FACE,{"disambiguationData":[OSD([subQ4,subQ3])]});var subQ6=sQuery(id+"F5.wireOp",EDGE,"E5");var subQ7=makeQuery(id+"F4.boolean.opBoolean","MERGE",EDGE,{"derivedFrom":[makeQuery(id+"F3.boolean.opBoolean","MERGE",EDGE,{"derivedFrom":[makeQuery(id+"F2.opExtrude","CAP_EDGE",EDGE,{"disambiguationData":[OSD([subQ4])],"isStart":false}),makeQuery(id+"F3.opExtrude","SWEPT_EDGE",EDGE,{"disambiguationData":[OSD([subQ4,subQ3]),TDD([makeQuery(id+"F2.opExtrude","CAP_VERTEX",VERTEX,{"disambiguationData":[OSD([subQ4,subQ3])],"isStart":false})])]})]}),makeQuery(id+"F4.opExtrude","SWEPT_EDGE",EDGE,{"disambiguationData":[OSD([subQ4,subQ0]),TDD([makeQuery(id+"F2.opExtrude","CAP_VERTEX",VERTEX,{"disambiguationData":[OSD([subQ4,subQ0])],"isStart":false})])]})]});var subQ8=sQuery(id+"F5.wireOp",EDGE,"E3");var subQ9=sQuery(id+"F5.wireOp",EDGE,"E4");var subQ10=makeQuery(id+"F4.boolean.opBoolean","MERGE",EDGE,{"derivedFrom":[makeQuery(id+"F3.boolean.opBoolean","MERGE",EDGE,{"derivedFrom":[makeQuery(id+"F1.opExtrude","CAP_EDGE",EDGE,{"disambiguationData":[OSD([subQ4])],"isStart":false}),makeQuery(id+"F3.opExtrude","SWEPT_EDGE",EDGE,{"disambiguationData":[OSD([subQ4,subQ3]),TDD([makeQuery(id+"F1.opExtrude","CAP_VERTEX",VERTEX,{"disambiguationData":[OSD([subQ4,subQ3])],"isStart":false})])]})]}),makeQuery(id+"F4.opExtrude","SWEPT_EDGE",EDGE,{"disambiguationData":[OSD([subQ4,subQ0]),TDD([makeQuery(id+"F1.opExtrude","CAP_VERTEX",VERTEX,{"disambiguationData":[OSD([subQ4,subQ0])],"isStart":false})])]})]});var subQ11=sQuery(id+"F5.wireOp",EDGE,"E13");var subQ12=sQuery(id+"F5.wireOp",EDGE,"E8");var subQ13=makeQuery(id+"F1.opExtrude","SWEPT_FACE",FACE,{"disambiguationData":[OSD([subQ4])]});var subQ14=makeQuery(id+"F4.opExtrude","SWEPT_FACE",FACE,{"disambiguationData":[OSD([subQ4,subQ0])]});var subQ15=sQuery(id+"F0.wireOp",EDGE,"E0.top");var subQ16=sQuery(id+"F5.wireOp",EDGE,"E15");var subQ17=makeQuery(id+"F2.opExtrude","SWEPT_FACE",FACE,{"disambiguationData":[OSD([subQ4])]});Q4=makeQuery(id+"F7.boolean.opBoolean","SPLIT",FACE,{"disambiguationData":[TD([subQ13,makeQuery(id+"F1.opExtrude","CAP_FACE",FACE,{"disambiguationData":[OSD([subQ4,subQ15,subQ3,subQ0])],"isStart":false}),subQ17,makeQuery(id+"F2.opExtrude","CAP_FACE",FACE,{"disambiguationData":[OSD([subQ4,subQ15,subQ3,subQ0])],"isStart":false}),makeQuery(id+"F3.opExtrude","SWEPT_FACE",FACE,{"disambiguationData":[OSD([subQ3]),TDD([makeQuery(id+"F1.opExtrude","CAP_EDGE",EDGE,{"disambiguationData":[OSD([subQ3])],"isStart":false})])]}),makeQuery(id+"F3.opExtrude","SWEPT_FACE",FACE,{"disambiguationData":[OSD([subQ3]),TDD([makeQuery(id+"F2.opExtrude","CAP_EDGE",EDGE,{"disambiguationData":[OSD([subQ3])],"isStart":false})])]}),subQ5,makeQuery(id+"F4.opExtrude","SWEPT_FACE",FACE,{"disambiguationData":[OSD([subQ0]),TDD([makeQuery(id+"F1.opExtrude","CAP_EDGE",EDGE,{"disambiguationData":[OSD([subQ0])],"isStart":false})])]}),makeQuery(id+"F4.opExtrude","SWEPT_FACE",FACE,{"disambiguationData":[OSD([subQ0]),TDD([makeQuery(id+"F2.opExtrude","CAP_EDGE",EDGE,{"disambiguationData":[OSD([subQ0])],"isStart":false})])]}),subQ14,makeQuery(id+"F7.opExtrude","SWEPT_FACE",FACE,{"disambiguationData":[OSD([subQ9])]}),makeQuery(id+"F7.opExtrude","SWEPT_FACE",FACE,{"disambiguationData":[OSD([subQ2])]}),makeQuery(id+"F7.opExtrude","SWEPT_FACE",FACE,{"disambiguationData":[OSD([subQ1])]}),makeQuery(id+"F7.opExtrude","SWEPT_FACE",FACE,{"disambiguationData":[OSD([subQ16])]}),makeQuery(id+"F7.opExtrude","SWEPT_FACE",FACE,{"disambiguationData":[OSD([subQ4,subQ3,subQ0]),TDD([makeQuery(id+"F5.imprint","IMPRINT",EDGE,{"disambiguationData":[TD([[makeQuery(id+"F5.imprint","INTERSECT",VERTEX,{"derivedFrom":[subQ10,subQ8,subQ9]}),1.0]])],"derivedFrom":subQ10})])]}),makeQuery(id+"F7.opExtrude","SWEPT_FACE",FACE,{"disambiguationData":[OSD([subQ4,subQ3,subQ0]),TDD([makeQuery(id+"F5.imprint","IMPRINT",EDGE,{"disambiguationData":[TD([[makeQuery(id+"F5.imprint","INTERSECT",VERTEX,{"derivedFrom":[subQ10,subQ6,sQuery(id+"F5.wireOp",EDGE,"E6")]}),-1.0]])],"derivedFrom":subQ10})])]}),makeQuery(id+"F7.opExtrude","SWEPT_FACE",FACE,{"disambiguationData":[OSD([subQ4,subQ3,subQ0]),TDD([makeQuery(id+"F5.imprint","IMPRINT",EDGE,{"disambiguationData":[TD([[makeQuery(id+"F5.imprint","INTERSECT",VERTEX,{"derivedFrom":[subQ7,sQuery(id+"F5.wireOp",EDGE,"E1"),subQ6]}),1.0]])],"derivedFrom":subQ7})])]}),makeQuery(id+"F7.opExtrude","SWEPT_FACE",FACE,{"disambiguationData":[OSD([subQ4,subQ3,subQ0]),TDD([makeQuery(id+"F5.imprint","IMPRINT",EDGE,{"disambiguationData":[TD([[makeQuery(id+"F5.imprint","INTERSECT",VERTEX,{"derivedFrom":[subQ7,subQ12,sQuery(id+"F5.wireOp",EDGE,"E9")]}),-1.0]])],"derivedFrom":subQ7})])]}),makeQuery(id+"F7.opExtrude","SWEPT_FACE",FACE,{"disambiguationData":[OSD([subQ4,subQ3,subQ0]),TDD([makeQuery(id+"F5.imprint","IMPRINT",EDGE,{"disambiguationData":[TD([[makeQuery(id+"F5.imprint","INTERSECT",VERTEX,{"derivedFrom":[subQ7,subQ11,subQ1]}),1.0]])],"derivedFrom":subQ7})])]})])],"derivedFrom":makeQuery(id+"F4.boolean.opBoolean","MERGE",FACE,{"derivedFrom":[makeQuery(id+"F3.boolean.opBoolean","MERGE",FACE,{"derivedFrom":[makeQuery(id+"F2.boolean.opBoolean","MERGE",FACE,{"derivedFrom":[subQ13,subQ17]}),subQ5]}),subQ14]})});}
            var Q5;
            {var subQ0=sQuery(id+"F0.wireOp",EDGE,"E0.right");var subQ1=sQuery(id+"F5.wireOp",EDGE,"E14");var subQ2=sQuery(id+"F0.wireOp",EDGE,"E0.left");var subQ3=sQuery(id+"F0.wireOp",EDGE,"E0.bottom");var subQ4=makeQuery(id+"F3.opExtrude","SWEPT_FACE",FACE,{"disambiguationData":[OSD([subQ3,subQ2])]});var subQ5=sQuery(id+"F5.wireOp",EDGE,"E5");var subQ6=makeQuery(id+"F4.boolean.opBoolean","MERGE",EDGE,{"derivedFrom":[makeQuery(id+"F3.boolean.opBoolean","MERGE",EDGE,{"derivedFrom":[makeQuery(id+"F2.opExtrude","CAP_EDGE",EDGE,{"disambiguationData":[OSD([subQ3])],"isStart":false}),makeQuery(id+"F3.opExtrude","SWEPT_EDGE",EDGE,{"disambiguationData":[OSD([subQ3,subQ2]),TDD([makeQuery(id+"F2.opExtrude","CAP_VERTEX",VERTEX,{"disambiguationData":[OSD([subQ3,subQ2])],"isStart":false})])]})]}),makeQuery(id+"F4.opExtrude","SWEPT_EDGE",EDGE,{"disambiguationData":[OSD([subQ3,subQ0]),TDD([makeQuery(id+"F2.opExtrude","CAP_VERTEX",VERTEX,{"disambiguationData":[OSD([subQ3,subQ0])],"isStart":false})])]})]});var subQ7=sQuery(id+"F5.wireOp",EDGE,"E3");var subQ8=makeQuery(id+"F4.boolean.opBoolean","MERGE",EDGE,{"derivedFrom":[makeQuery(id+"F3.boolean.opBoolean","MERGE",EDGE,{"derivedFrom":[makeQuery(id+"F1.opExtrude","CAP_EDGE",EDGE,{"disambiguationData":[OSD([subQ3])],"isStart":false}),makeQuery(id+"F3.opExtrude","SWEPT_EDGE",EDGE,{"disambiguationData":[OSD([subQ3,subQ2]),TDD([makeQuery(id+"F1.opExtrude","CAP_VERTEX",VERTEX,{"disambiguationData":[OSD([subQ3,subQ2])],"isStart":false})])]})]}),makeQuery(id+"F4.opExtrude","SWEPT_EDGE",EDGE,{"disambiguationData":[OSD([subQ3,subQ0]),TDD([makeQuery(id+"F1.opExtrude","CAP_VERTEX",VERTEX,{"disambiguationData":[OSD([subQ3,subQ0])],"isStart":false})])]})]});var subQ9=sQuery(id+"F5.wireOp",EDGE,"E13");var subQ10=sQuery(id+"F5.wireOp",EDGE,"E8");var subQ11=makeQuery(id+"F1.opExtrude","SWEPT_FACE",FACE,{"disambiguationData":[OSD([subQ3])]});var subQ12=makeQuery(id+"F4.opExtrude","SWEPT_FACE",FACE,{"disambiguationData":[OSD([subQ3,subQ0])]});var subQ13=sQuery(id+"F0.wireOp",EDGE,"E0.top");var subQ14=sQuery(id+"F5.wireOp",EDGE,"E15");var subQ15=makeQuery(id+"F2.opExtrude","SWEPT_FACE",FACE,{"disambiguationData":[OSD([subQ3])]});Q5=makeQuery(id+"F7.boolean.opBoolean","SPLIT",FACE,{"disambiguationData":[TD([subQ11,makeQuery(id+"F1.opExtrude","CAP_FACE",FACE,{"disambiguationData":[OSD([subQ3,subQ13,subQ2,subQ0])],"isStart":false}),subQ15,makeQuery(id+"F2.opExtrude","CAP_FACE",FACE,{"disambiguationData":[OSD([subQ3,subQ13,subQ2,subQ0])],"isStart":false}),makeQuery(id+"F3.opExtrude","SWEPT_FACE",FACE,{"disambiguationData":[OSD([subQ2]),TDD([makeQuery(id+"F1.opExtrude","CAP_EDGE",EDGE,{"disambiguationData":[OSD([subQ2])],"isStart":false})])]}),makeQuery(id+"F3.opExtrude","SWEPT_FACE",FACE,{"disambiguationData":[OSD([subQ2]),TDD([makeQuery(id+"F2.opExtrude","CAP_EDGE",EDGE,{"disambiguationData":[OSD([subQ2])],"isStart":false})])]}),subQ4,makeQuery(id+"F3.opExtrude","CAP_FACE",FACE,{"disambiguationData":[OSD([subQ2])],"isStart":false}),makeQuery(id+"F4.opExtrude","SWEPT_FACE",FACE,{"disambiguationData":[OSD([subQ0]),TDD([makeQuery(id+"F1.opExtrude","CAP_EDGE",EDGE,{"disambiguationData":[OSD([subQ0])],"isStart":false})])]}),makeQuery(id+"F4.opExtrude","SWEPT_FACE",FACE,{"disambiguationData":[OSD([subQ0]),TDD([makeQuery(id+"F2.opExtrude","CAP_EDGE",EDGE,{"disambiguationData":[OSD([subQ0])],"isStart":false})])]}),subQ12,makeQuery(id+"F7.opExtrude","SWEPT_FACE",FACE,{"disambiguationData":[OSD([subQ1])]}),makeQuery(id+"F7.opExtrude","SWEPT_FACE",FACE,{"disambiguationData":[OSD([subQ14])]}),makeQuery(id+"F7.opExtrude","SWEPT_FACE",FACE,{"disambiguationData":[OSD([subQ3,subQ2,subQ0]),TDD([makeQuery(id+"F5.imprint","IMPRINT",EDGE,{"disambiguationData":[TD([[makeQuery(id+"F5.imprint","INTERSECT",VERTEX,{"derivedFrom":[subQ8,subQ7,sQuery(id+"F5.wireOp",EDGE,"E4")]}),1.0]])],"derivedFrom":subQ8})])]}),makeQuery(id+"F7.opExtrude","SWEPT_FACE",FACE,{"disambiguationData":[OSD([subQ3,subQ2,subQ0]),TDD([makeQuery(id+"F5.imprint","IMPRINT",EDGE,{"disambiguationData":[TD([[makeQuery(id+"F5.imprint","INTERSECT",VERTEX,{"derivedFrom":[subQ8,subQ5,sQuery(id+"F5.wireOp",EDGE,"E6")]}),-1.0]])],"derivedFrom":subQ8})])]}),makeQuery(id+"F7.opExtrude","SWEPT_FACE",FACE,{"disambiguationData":[OSD([subQ3,subQ2,subQ0]),TDD([makeQuery(id+"F5.imprint","IMPRINT",EDGE,{"disambiguationData":[TD([[makeQuery(id+"F5.imprint","INTERSECT",VERTEX,{"derivedFrom":[subQ6,sQuery(id+"F5.wireOp",EDGE,"E1"),subQ5]}),1.0]])],"derivedFrom":subQ6})])]}),makeQuery(id+"F7.opExtrude","SWEPT_FACE",FACE,{"disambiguationData":[OSD([subQ3,subQ2,subQ0]),TDD([makeQuery(id+"F5.imprint","IMPRINT",EDGE,{"disambiguationData":[TD([[makeQuery(id+"F5.imprint","INTERSECT",VERTEX,{"derivedFrom":[subQ6,subQ10,sQuery(id+"F5.wireOp",EDGE,"E9")]}),-1.0]])],"derivedFrom":subQ6})])]}),makeQuery(id+"F7.opExtrude","SWEPT_FACE",FACE,{"disambiguationData":[OSD([subQ3,subQ2,subQ0]),TDD([makeQuery(id+"F5.imprint","IMPRINT",EDGE,{"disambiguationData":[TD([[makeQuery(id+"F5.imprint","INTERSECT",VERTEX,{"derivedFrom":[subQ6,subQ9,subQ1]}),1.0]])],"derivedFrom":subQ6})])]})])],"derivedFrom":makeQuery(id+"F4.boolean.opBoolean","MERGE",FACE,{"derivedFrom":[makeQuery(id+"F3.boolean.opBoolean","MERGE",FACE,{"derivedFrom":[makeQuery(id+"F2.boolean.opBoolean","MERGE",FACE,{"derivedFrom":[subQ11,subQ15]}),subQ4]}),subQ12]})});}
            var Q6;
            {var subQ0=sQuery(id+"F6.wireOp",EDGE,"E18");var subQ1=sQuery(id+"F0.wireOp",EDGE,"E0.right");var subQ2=sQuery(id+"F0.wireOp",EDGE,"E0.top");var subQ3=sQuery(id+"F0.wireOp",EDGE,"E0.left");var subQ4=makeQuery(id+"F4.boolean.opBoolean","MERGE",EDGE,{"derivedFrom":[makeQuery(id+"F3.boolean.opBoolean","MERGE",EDGE,{"derivedFrom":[makeQuery(id+"F2.opExtrude","CAP_EDGE",EDGE,{"disambiguationData":[OSD([subQ2])],"isStart":false}),makeQuery(id+"F3.opExtrude","SWEPT_EDGE",EDGE,{"disambiguationData":[OSD([subQ2,subQ3]),TDD([makeQuery(id+"F2.opExtrude","CAP_VERTEX",VERTEX,{"disambiguationData":[OSD([subQ2,subQ3])],"isStart":false})])]})]}),makeQuery(id+"F4.opExtrude","SWEPT_EDGE",EDGE,{"disambiguationData":[OSD([subQ2,subQ1]),TDD([makeQuery(id+"F2.opExtrude","CAP_VERTEX",VERTEX,{"disambiguationData":[OSD([subQ2,subQ1])],"isStart":false})])]})]});var subQ5=sQuery(id+"F6.wireOp",EDGE,"E26");var subQ6=sQuery(id+"F6.wireOp",EDGE,"E23");var subQ7=makeQuery(id+"F3.opExtrude","SWEPT_FACE",FACE,{"disambiguationData":[OSD([subQ2,subQ3])]});var subQ8=sQuery(id+"F6.wireOp",EDGE,"E22");var subQ9=makeQuery(id+"F4.boolean.opBoolean","MERGE",EDGE,{"derivedFrom":[makeQuery(id+"F3.boolean.opBoolean","MERGE",EDGE,{"derivedFrom":[makeQuery(id+"F1.opExtrude","CAP_EDGE",EDGE,{"disambiguationData":[OSD([subQ2])],"isStart":false}),makeQuery(id+"F3.opExtrude","SWEPT_EDGE",EDGE,{"disambiguationData":[OSD([subQ2,subQ3]),TDD([makeQuery(id+"F1.opExtrude","CAP_VERTEX",VERTEX,{"disambiguationData":[OSD([subQ2,subQ3])],"isStart":false})])]})]}),makeQuery(id+"F4.opExtrude","SWEPT_EDGE",EDGE,{"disambiguationData":[OSD([subQ2,subQ1]),TDD([makeQuery(id+"F1.opExtrude","CAP_VERTEX",VERTEX,{"disambiguationData":[OSD([subQ2,subQ1])],"isStart":false})])]})]});var subQ10=sQuery(id+"F6.wireOp",EDGE,"E21");var subQ11=sQuery(id+"F5.wireOp",EDGE,"E13");var subQ12=sQuery(id+"F0.wireOp",EDGE,"E0.bottom");var subQ13=makeQuery(id+"F4.boolean.opBoolean","MERGE",EDGE,{"derivedFrom":[makeQuery(id+"F3.boolean.opBoolean","MERGE",EDGE,{"derivedFrom":[makeQuery(id+"F2.opExtrude","CAP_EDGE",EDGE,{"disambiguationData":[OSD([subQ12])],"isStart":false}),makeQuery(id+"F3.opExtrude","SWEPT_EDGE",EDGE,{"disambiguationData":[OSD([subQ12,subQ3]),TDD([makeQuery(id+"F2.opExtrude","CAP_VERTEX",VERTEX,{"disambiguationData":[OSD([subQ12,subQ3])],"isStart":false})])]})]}),makeQuery(id+"F4.opExtrude","SWEPT_EDGE",EDGE,{"disambiguationData":[OSD([subQ12,subQ1]),TDD([makeQuery(id+"F2.opExtrude","CAP_VERTEX",VERTEX,{"disambiguationData":[OSD([subQ12,subQ1])],"isStart":false})])]})]});var subQ14=sQuery(id+"F5.wireOp",EDGE,"E5");var subQ15=sQuery(id+"F5.wireOp",EDGE,"E3");var subQ16=makeQuery(id+"F4.opExtrude","SWEPT_FACE",FACE,{"disambiguationData":[OSD([subQ2,subQ1])]});var subQ17=makeQuery(id+"F2.opExtrude","SWEPT_FACE",FACE,{"disambiguationData":[OSD([subQ2])]});var subQ18=sQuery(id+"F6.wireOp",EDGE,"E29");var subQ19=sQuery(id+"F5.wireOp",EDGE,"E8");var subQ20=makeQuery(id+"F4.boolean.opBoolean","MERGE",EDGE,{"derivedFrom":[makeQuery(id+"F3.boolean.opBoolean","MERGE",EDGE,{"derivedFrom":[makeQuery(id+"F1.opExtrude","CAP_EDGE",EDGE,{"disambiguationData":[OSD([subQ12])],"isStart":false}),makeQuery(id+"F3.opExtrude","SWEPT_EDGE",EDGE,{"disambiguationData":[OSD([subQ12,subQ3]),TDD([makeQuery(id+"F1.opExtrude","CAP_VERTEX",VERTEX,{"disambiguationData":[OSD([subQ12,subQ3])],"isStart":false})])]})]}),makeQuery(id+"F4.opExtrude","SWEPT_EDGE",EDGE,{"disambiguationData":[OSD([subQ12,subQ1]),TDD([makeQuery(id+"F1.opExtrude","CAP_VERTEX",VERTEX,{"disambiguationData":[OSD([subQ12,subQ1])],"isStart":false})])]})]});var subQ21=makeQuery(id+"F1.opExtrude","SWEPT_FACE",FACE,{"disambiguationData":[OSD([subQ2])]});Q6=makeQuery(id+"F9.boolean.opBoolean","SPLIT",FACE,{"disambiguationData":[TD([makeQuery(id+"F1.opExtrude","CAP_FACE",FACE,{"disambiguationData":[OSD([subQ12,subQ2,subQ3,subQ1])],"isStart":false}),subQ21,subQ17,makeQuery(id+"F2.opExtrude","CAP_FACE",FACE,{"disambiguationData":[OSD([subQ12,subQ2,subQ3,subQ1])],"isStart":false}),makeQuery(id+"F3.opExtrude","SWEPT_FACE",FACE,{"disambiguationData":[OSD([subQ3]),TDD([makeQuery(id+"F1.opExtrude","CAP_EDGE",EDGE,{"disambiguationData":[OSD([subQ3])],"isStart":false})])]}),makeQuery(id+"F3.opExtrude","SWEPT_FACE",FACE,{"disambiguationData":[OSD([subQ3]),TDD([makeQuery(id+"F2.opExtrude","CAP_EDGE",EDGE,{"disambiguationData":[OSD([subQ3])],"isStart":false})])]}),subQ7,makeQuery(id+"F3.opExtrude","CAP_FACE",FACE,{"disambiguationData":[OSD([subQ3])],"isStart":false}),makeQuery(id+"F4.opExtrude","SWEPT_FACE",FACE,{"disambiguationData":[OSD([subQ1]),TDD([makeQuery(id+"F1.opExtrude","CAP_EDGE",EDGE,{"disambiguationData":[OSD([subQ1])],"isStart":false})])]}),makeQuery(id+"F4.opExtrude","SWEPT_FACE",FACE,{"disambiguationData":[OSD([subQ1]),TDD([makeQuery(id+"F2.opExtrude","CAP_EDGE",EDGE,{"disambiguationData":[OSD([subQ1])],"isStart":false})])]}),subQ16,makeQuery(id+"F7.opExtrude","SWEPT_FACE",FACE,{"disambiguationData":[OSD([subQ12,subQ3,subQ1]),TDD([makeQuery(id+"F5.imprint","IMPRINT",EDGE,{"disambiguationData":[TD([[makeQuery(id+"F5.imprint","INTERSECT",VERTEX,{"derivedFrom":[subQ20,subQ15,sQuery(id+"F5.wireOp",EDGE,"E4")]}),1.0]])],"derivedFrom":subQ20})])]}),makeQuery(id+"F7.opExtrude","SWEPT_FACE",FACE,{"disambiguationData":[OSD([subQ12,subQ3,subQ1]),TDD([makeQuery(id+"F5.imprint","IMPRINT",EDGE,{"disambiguationData":[TD([[makeQuery(id+"F5.imprint","INTERSECT",VERTEX,{"derivedFrom":[subQ20,subQ14,sQuery(id+"F5.wireOp",EDGE,"E6")]}),-1.0]])],"derivedFrom":subQ20})])]}),makeQuery(id+"F7.opExtrude","SWEPT_FACE",FACE,{"disambiguationData":[OSD([subQ12,subQ3,subQ1]),TDD([makeQuery(id+"F5.imprint","IMPRINT",EDGE,{"disambiguationData":[TD([[makeQuery(id+"F5.imprint","INTERSECT",VERTEX,{"derivedFrom":[subQ13,sQuery(id+"F5.wireOp",EDGE,"E1"),subQ14]}),1.0]])],"derivedFrom":subQ13})])]}),makeQuery(id+"F7.opExtrude","SWEPT_FACE",FACE,{"disambiguationData":[OSD([subQ12,subQ3,subQ1]),TDD([makeQuery(id+"F5.imprint","IMPRINT",EDGE,{"disambiguationData":[TD([[makeQuery(id+"F5.imprint","INTERSECT",VERTEX,{"derivedFrom":[subQ13,subQ19,sQuery(id+"F5.wireOp",EDGE,"E9")]}),-1.0]])],"derivedFrom":subQ13})])]}),makeQuery(id+"F7.opExtrude","SWEPT_FACE",FACE,{"disambiguationData":[OSD([subQ12,subQ3,subQ1]),TDD([makeQuery(id+"F5.imprint","IMPRINT",EDGE,{"disambiguationData":[TD([[makeQuery(id+"F5.imprint","INTERSECT",VERTEX,{"derivedFrom":[subQ13,subQ11,sQuery(id+"F5.wireOp",EDGE,"E14")]}),1.0]])],"derivedFrom":subQ13})])]}),makeQuery(id+"F9.opExtrude","SWEPT_FACE",FACE,{"disambiguationData":[OSD([subQ8])]}),makeQuery(id+"F9.opExtrude","SWEPT_FACE",FACE,{"disambiguationData":[OSD([subQ6])]}),makeQuery(id+"F9.opExtrude","SWEPT_FACE",FACE,{"disambiguationData":[OSD([subQ2,subQ3,subQ1]),TDD([makeQuery(id+"F6.imprint","IMPRINT",EDGE,{"disambiguationData":[TD([[makeQuery(id+"F6.imprint","INTERSECT",VERTEX,{"derivedFrom":[subQ9,subQ0,sQuery(id+"F6.wireOp",EDGE,"E19")]}),1.0]])],"derivedFrom":subQ9})])]}),makeQuery(id+"F9.opExtrude","SWEPT_FACE",FACE,{"disambiguationData":[OSD([subQ2,subQ3,subQ1]),TDD([makeQuery(id+"F6.imprint","IMPRINT",EDGE,{"disambiguationData":[TD([[makeQuery(id+"F6.imprint","INTERSECT",VERTEX,{"derivedFrom":[subQ9,subQ5,sQuery(id+"F6.wireOp",EDGE,"E27")]}),-1.0]])],"derivedFrom":subQ9})])]}),makeQuery(id+"F9.opExtrude","SWEPT_FACE",FACE,{"disambiguationData":[OSD([subQ2,subQ3,subQ1]),TDD([makeQuery(id+"F6.imprint","IMPRINT",EDGE,{"disambiguationData":[TD([[makeQuery(id+"F6.imprint","INTERSECT",VERTEX,{"derivedFrom":[subQ4,sQuery(id+"F6.wireOp",EDGE,"E17"),subQ0]}),-1.0]])],"derivedFrom":subQ4})])]}),makeQuery(id+"F9.opExtrude","SWEPT_FACE",FACE,{"disambiguationData":[OSD([subQ2,subQ3,subQ1]),TDD([makeQuery(id+"F6.imprint","IMPRINT",EDGE,{"disambiguationData":[TD([[makeQuery(id+"F6.imprint","INTERSECT",VERTEX,{"derivedFrom":[subQ4,subQ10,subQ8]}),1.0]])],"derivedFrom":subQ4})])]}),makeQuery(id+"F9.opExtrude","SWEPT_FACE",FACE,{"disambiguationData":[OSD([subQ2,subQ3,subQ1]),TDD([makeQuery(id+"F6.imprint","IMPRINT",EDGE,{"disambiguationData":[TD([[makeQuery(id+"F6.imprint","INTERSECT",VERTEX,{"derivedFrom":[subQ4,subQ18,sQuery(id+"F6.wireOp",EDGE,"E30")]}),-1.0]])],"derivedFrom":subQ4})])]})])],"derivedFrom":makeQuery(id+"F4.boolean.opBoolean","MERGE",FACE,{"derivedFrom":[makeQuery(id+"F3.boolean.opBoolean","MERGE",FACE,{"derivedFrom":[makeQuery(id+"F2.boolean.opBoolean","MERGE",FACE,{"derivedFrom":[subQ21,subQ17]}),subQ7]}),subQ16]})});}
            var Q7;
            {var subQ0=sQuery(id+"F6.wireOp",EDGE,"E18");var subQ1=sQuery(id+"F0.wireOp",EDGE,"E0.right");var subQ2=sQuery(id+"F0.wireOp",EDGE,"E0.top");var subQ3=sQuery(id+"F0.wireOp",EDGE,"E0.left");var subQ4=makeQuery(id+"F4.boolean.opBoolean","MERGE",EDGE,{"derivedFrom":[makeQuery(id+"F3.boolean.opBoolean","MERGE",EDGE,{"derivedFrom":[makeQuery(id+"F2.opExtrude","CAP_EDGE",EDGE,{"disambiguationData":[OSD([subQ2])],"isStart":false}),makeQuery(id+"F3.opExtrude","SWEPT_EDGE",EDGE,{"disambiguationData":[OSD([subQ2,subQ3]),TDD([makeQuery(id+"F2.opExtrude","CAP_VERTEX",VERTEX,{"disambiguationData":[OSD([subQ2,subQ3])],"isStart":false})])]})]}),makeQuery(id+"F4.opExtrude","SWEPT_EDGE",EDGE,{"disambiguationData":[OSD([subQ2,subQ1]),TDD([makeQuery(id+"F2.opExtrude","CAP_VERTEX",VERTEX,{"disambiguationData":[OSD([subQ2,subQ1])],"isStart":false})])]})]});var subQ5=sQuery(id+"F6.wireOp",EDGE,"E26");var subQ6=makeQuery(id+"F4.boolean.opBoolean","MERGE",EDGE,{"derivedFrom":[makeQuery(id+"F3.boolean.opBoolean","MERGE",EDGE,{"derivedFrom":[makeQuery(id+"F1.opExtrude","CAP_EDGE",EDGE,{"disambiguationData":[OSD([subQ2])],"isStart":false}),makeQuery(id+"F3.opExtrude","SWEPT_EDGE",EDGE,{"disambiguationData":[OSD([subQ2,subQ3]),TDD([makeQuery(id+"F1.opExtrude","CAP_VERTEX",VERTEX,{"disambiguationData":[OSD([subQ2,subQ3])],"isStart":false})])]})]}),makeQuery(id+"F4.opExtrude","SWEPT_EDGE",EDGE,{"disambiguationData":[OSD([subQ2,subQ1]),TDD([makeQuery(id+"F1.opExtrude","CAP_VERTEX",VERTEX,{"disambiguationData":[OSD([subQ2,subQ1])],"isStart":false})])]})]});var subQ7=sQuery(id+"F6.wireOp",EDGE,"E29");var subQ8=makeQuery(id+"F2.opExtrude","SWEPT_FACE",FACE,{"disambiguationData":[OSD([subQ2])]});var subQ9=sQuery(id+"F6.wireOp",EDGE,"E23");var subQ10=makeQuery(id+"F3.opExtrude","SWEPT_FACE",FACE,{"disambiguationData":[OSD([subQ2,subQ3])]});var subQ11=sQuery(id+"F6.wireOp",EDGE,"E22");var subQ12=sQuery(id+"F6.wireOp",EDGE,"E20");var subQ13=sQuery(id+"F6.wireOp",EDGE,"E19");var subQ14=sQuery(id+"F6.wireOp",EDGE,"E21");var subQ15=sQuery(id+"F5.wireOp",EDGE,"E13");var subQ16=sQuery(id+"F0.wireOp",EDGE,"E0.bottom");var subQ17=makeQuery(id+"F4.boolean.opBoolean","MERGE",EDGE,{"derivedFrom":[makeQuery(id+"F3.boolean.opBoolean","MERGE",EDGE,{"derivedFrom":[makeQuery(id+"F2.opExtrude","CAP_EDGE",EDGE,{"disambiguationData":[OSD([subQ16])],"isStart":false}),makeQuery(id+"F3.opExtrude","SWEPT_EDGE",EDGE,{"disambiguationData":[OSD([subQ16,subQ3]),TDD([makeQuery(id+"F2.opExtrude","CAP_VERTEX",VERTEX,{"disambiguationData":[OSD([subQ16,subQ3])],"isStart":false})])]})]}),makeQuery(id+"F4.opExtrude","SWEPT_EDGE",EDGE,{"disambiguationData":[OSD([subQ16,subQ1]),TDD([makeQuery(id+"F2.opExtrude","CAP_VERTEX",VERTEX,{"disambiguationData":[OSD([subQ16,subQ1])],"isStart":false})])]})]});var subQ18=sQuery(id+"F5.wireOp",EDGE,"E5");var subQ19=sQuery(id+"F5.wireOp",EDGE,"E3");var subQ20=sQuery(id+"F5.wireOp",EDGE,"E8");var subQ21=makeQuery(id+"F4.boolean.opBoolean","MERGE",EDGE,{"derivedFrom":[makeQuery(id+"F3.boolean.opBoolean","MERGE",EDGE,{"derivedFrom":[makeQuery(id+"F1.opExtrude","CAP_EDGE",EDGE,{"disambiguationData":[OSD([subQ16])],"isStart":false}),makeQuery(id+"F3.opExtrude","SWEPT_EDGE",EDGE,{"disambiguationData":[OSD([subQ16,subQ3]),TDD([makeQuery(id+"F1.opExtrude","CAP_VERTEX",VERTEX,{"disambiguationData":[OSD([subQ16,subQ3])],"isStart":false})])]})]}),makeQuery(id+"F4.opExtrude","SWEPT_EDGE",EDGE,{"disambiguationData":[OSD([subQ16,subQ1]),TDD([makeQuery(id+"F1.opExtrude","CAP_VERTEX",VERTEX,{"disambiguationData":[OSD([subQ16,subQ1])],"isStart":false})])]})]});var subQ22=makeQuery(id+"F1.opExtrude","SWEPT_FACE",FACE,{"disambiguationData":[OSD([subQ2])]});var subQ23=makeQuery(id+"F4.opExtrude","SWEPT_FACE",FACE,{"disambiguationData":[OSD([subQ2,subQ1])]});Q7=makeQuery(id+"F9.boolean.opBoolean","SPLIT",FACE,{"disambiguationData":[TD([makeQuery(id+"F1.opExtrude","CAP_FACE",FACE,{"disambiguationData":[OSD([subQ16,subQ2,subQ3,subQ1])],"isStart":false}),subQ22,subQ8,makeQuery(id+"F2.opExtrude","CAP_FACE",FACE,{"disambiguationData":[OSD([subQ16,subQ2,subQ3,subQ1])],"isStart":false}),makeQuery(id+"F3.opExtrude","SWEPT_FACE",FACE,{"disambiguationData":[OSD([subQ3]),TDD([makeQuery(id+"F1.opExtrude","CAP_EDGE",EDGE,{"disambiguationData":[OSD([subQ3])],"isStart":false})])]}),makeQuery(id+"F3.opExtrude","SWEPT_FACE",FACE,{"disambiguationData":[OSD([subQ3]),TDD([makeQuery(id+"F2.opExtrude","CAP_EDGE",EDGE,{"disambiguationData":[OSD([subQ3])],"isStart":false})])]}),subQ10,makeQuery(id+"F4.opExtrude","SWEPT_FACE",FACE,{"disambiguationData":[OSD([subQ1]),TDD([makeQuery(id+"F1.opExtrude","CAP_EDGE",EDGE,{"disambiguationData":[OSD([subQ1])],"isStart":false})])]}),makeQuery(id+"F4.opExtrude","SWEPT_FACE",FACE,{"disambiguationData":[OSD([subQ1]),TDD([makeQuery(id+"F2.opExtrude","CAP_EDGE",EDGE,{"disambiguationData":[OSD([subQ1])],"isStart":false})])]}),subQ23,makeQuery(id+"F7.opExtrude","SWEPT_FACE",FACE,{"disambiguationData":[OSD([subQ16,subQ3,subQ1]),TDD([makeQuery(id+"F5.imprint","IMPRINT",EDGE,{"disambiguationData":[TD([[makeQuery(id+"F5.imprint","INTERSECT",VERTEX,{"derivedFrom":[subQ21,subQ19,sQuery(id+"F5.wireOp",EDGE,"E4")]}),1.0]])],"derivedFrom":subQ21})])]}),makeQuery(id+"F7.opExtrude","SWEPT_FACE",FACE,{"disambiguationData":[OSD([subQ16,subQ3,subQ1]),TDD([makeQuery(id+"F5.imprint","IMPRINT",EDGE,{"disambiguationData":[TD([[makeQuery(id+"F5.imprint","INTERSECT",VERTEX,{"derivedFrom":[subQ21,subQ18,sQuery(id+"F5.wireOp",EDGE,"E6")]}),-1.0]])],"derivedFrom":subQ21})])]}),makeQuery(id+"F7.opExtrude","SWEPT_FACE",FACE,{"disambiguationData":[OSD([subQ16,subQ3,subQ1]),TDD([makeQuery(id+"F5.imprint","IMPRINT",EDGE,{"disambiguationData":[TD([[makeQuery(id+"F5.imprint","INTERSECT",VERTEX,{"derivedFrom":[subQ17,sQuery(id+"F5.wireOp",EDGE,"E1"),subQ18]}),1.0]])],"derivedFrom":subQ17})])]}),makeQuery(id+"F7.opExtrude","SWEPT_FACE",FACE,{"disambiguationData":[OSD([subQ16,subQ3,subQ1]),TDD([makeQuery(id+"F5.imprint","IMPRINT",EDGE,{"disambiguationData":[TD([[makeQuery(id+"F5.imprint","INTERSECT",VERTEX,{"derivedFrom":[subQ17,subQ20,sQuery(id+"F5.wireOp",EDGE,"E9")]}),-1.0]])],"derivedFrom":subQ17})])]}),makeQuery(id+"F7.opExtrude","SWEPT_FACE",FACE,{"disambiguationData":[OSD([subQ16,subQ3,subQ1]),TDD([makeQuery(id+"F5.imprint","IMPRINT",EDGE,{"disambiguationData":[TD([[makeQuery(id+"F5.imprint","INTERSECT",VERTEX,{"derivedFrom":[subQ17,subQ15,sQuery(id+"F5.wireOp",EDGE,"E14")]}),1.0]])],"derivedFrom":subQ17})])]}),makeQuery(id+"F9.opExtrude","SWEPT_FACE",FACE,{"disambiguationData":[OSD([subQ13])]}),makeQuery(id+"F9.opExtrude","SWEPT_FACE",FACE,{"disambiguationData":[OSD([subQ12])]}),makeQuery(id+"F9.opExtrude","SWEPT_FACE",FACE,{"disambiguationData":[OSD([subQ11])]}),makeQuery(id+"F9.opExtrude","SWEPT_FACE",FACE,{"disambiguationData":[OSD([subQ9])]}),makeQuery(id+"F9.opExtrude","SWEPT_FACE",FACE,{"disambiguationData":[OSD([subQ2,subQ3,subQ1]),TDD([makeQuery(id+"F6.imprint","IMPRINT",EDGE,{"disambiguationData":[TD([[makeQuery(id+"F6.imprint","INTERSECT",VERTEX,{"derivedFrom":[subQ6,subQ0,subQ13]}),1.0]])],"derivedFrom":subQ6})])]}),makeQuery(id+"F9.opExtrude","SWEPT_FACE",FACE,{"disambiguationData":[OSD([subQ2,subQ3,subQ1]),TDD([makeQuery(id+"F6.imprint","IMPRINT",EDGE,{"disambiguationData":[TD([[makeQuery(id+"F6.imprint","INTERSECT",VERTEX,{"derivedFrom":[subQ6,subQ5,sQuery(id+"F6.wireOp",EDGE,"E27")]}),-1.0]])],"derivedFrom":subQ6})])]}),makeQuery(id+"F9.opExtrude","SWEPT_FACE",FACE,{"disambiguationData":[OSD([subQ2,subQ3,subQ1]),TDD([makeQuery(id+"F6.imprint","IMPRINT",EDGE,{"disambiguationData":[TD([[makeQuery(id+"F6.imprint","INTERSECT",VERTEX,{"derivedFrom":[subQ4,sQuery(id+"F6.wireOp",EDGE,"E17"),subQ0]}),-1.0]])],"derivedFrom":subQ4})])]}),makeQuery(id+"F9.opExtrude","SWEPT_FACE",FACE,{"disambiguationData":[OSD([subQ2,subQ3,subQ1]),TDD([makeQuery(id+"F6.imprint","IMPRINT",EDGE,{"disambiguationData":[TD([[makeQuery(id+"F6.imprint","INTERSECT",VERTEX,{"derivedFrom":[subQ4,subQ14,subQ11]}),1.0]])],"derivedFrom":subQ4})])]}),makeQuery(id+"F9.opExtrude","SWEPT_FACE",FACE,{"disambiguationData":[OSD([subQ2,subQ3,subQ1]),TDD([makeQuery(id+"F6.imprint","IMPRINT",EDGE,{"disambiguationData":[TD([[makeQuery(id+"F6.imprint","INTERSECT",VERTEX,{"derivedFrom":[subQ4,subQ7,sQuery(id+"F6.wireOp",EDGE,"E30")]}),-1.0]])],"derivedFrom":subQ4})])]})])],"derivedFrom":makeQuery(id+"F4.boolean.opBoolean","MERGE",FACE,{"derivedFrom":[makeQuery(id+"F3.boolean.opBoolean","MERGE",FACE,{"derivedFrom":[makeQuery(id+"F2.boolean.opBoolean","MERGE",FACE,{"derivedFrom":[subQ22,subQ8]}),subQ10]}),subQ23]})});}
            var Q8;
            {var subQ0=sQuery(id+"F6.wireOp",EDGE,"E18");var subQ1=sQuery(id+"F6.wireOp",EDGE,"E17");var subQ2=sQuery(id+"F0.wireOp",EDGE,"E0.right");var subQ3=sQuery(id+"F0.wireOp",EDGE,"E0.top");var subQ4=sQuery(id+"F0.wireOp",EDGE,"E0.left");var subQ5=makeQuery(id+"F4.boolean.opBoolean","MERGE",EDGE,{"derivedFrom":[makeQuery(id+"F3.boolean.opBoolean","MERGE",EDGE,{"derivedFrom":[makeQuery(id+"F2.opExtrude","CAP_EDGE",EDGE,{"disambiguationData":[OSD([subQ3])],"isStart":false}),makeQuery(id+"F3.opExtrude","SWEPT_EDGE",EDGE,{"disambiguationData":[OSD([subQ3,subQ4]),TDD([makeQuery(id+"F2.opExtrude","CAP_VERTEX",VERTEX,{"disambiguationData":[OSD([subQ3,subQ4])],"isStart":false})])]})]}),makeQuery(id+"F4.opExtrude","SWEPT_EDGE",EDGE,{"disambiguationData":[OSD([subQ3,subQ2]),TDD([makeQuery(id+"F2.opExtrude","CAP_VERTEX",VERTEX,{"disambiguationData":[OSD([subQ3,subQ2])],"isStart":false})])]})]});var subQ6=sQuery(id+"F6.wireOp",EDGE,"E26");var subQ7=sQuery(id+"F6.wireOp",EDGE,"E25");var subQ8=makeQuery(id+"F4.boolean.opBoolean","MERGE",EDGE,{"derivedFrom":[makeQuery(id+"F3.boolean.opBoolean","MERGE",EDGE,{"derivedFrom":[makeQuery(id+"F1.opExtrude","CAP_EDGE",EDGE,{"disambiguationData":[OSD([subQ3])],"isStart":false}),makeQuery(id+"F3.opExtrude","SWEPT_EDGE",EDGE,{"disambiguationData":[OSD([subQ3,subQ4]),TDD([makeQuery(id+"F1.opExtrude","CAP_VERTEX",VERTEX,{"disambiguationData":[OSD([subQ3,subQ4])],"isStart":false})])]})]}),makeQuery(id+"F4.opExtrude","SWEPT_EDGE",EDGE,{"disambiguationData":[OSD([subQ3,subQ2]),TDD([makeQuery(id+"F1.opExtrude","CAP_VERTEX",VERTEX,{"disambiguationData":[OSD([subQ3,subQ2])],"isStart":false})])]})]});var subQ9=sQuery(id+"F6.wireOp",EDGE,"E29");var subQ10=makeQuery(id+"F2.opExtrude","SWEPT_FACE",FACE,{"disambiguationData":[OSD([subQ3])]});var subQ11=sQuery(id+"F6.wireOp",EDGE,"E20");var subQ12=sQuery(id+"F6.wireOp",EDGE,"E19");var subQ13=sQuery(id+"F6.wireOp",EDGE,"E21");var subQ14=sQuery(id+"F5.wireOp",EDGE,"E13");var subQ15=sQuery(id+"F0.wireOp",EDGE,"E0.bottom");var subQ16=makeQuery(id+"F4.boolean.opBoolean","MERGE",EDGE,{"derivedFrom":[makeQuery(id+"F3.boolean.opBoolean","MERGE",EDGE,{"derivedFrom":[makeQuery(id+"F2.opExtrude","CAP_EDGE",EDGE,{"disambiguationData":[OSD([subQ15])],"isStart":false}),makeQuery(id+"F3.opExtrude","SWEPT_EDGE",EDGE,{"disambiguationData":[OSD([subQ15,subQ4]),TDD([makeQuery(id+"F2.opExtrude","CAP_VERTEX",VERTEX,{"disambiguationData":[OSD([subQ15,subQ4])],"isStart":false})])]})]}),makeQuery(id+"F4.opExtrude","SWEPT_EDGE",EDGE,{"disambiguationData":[OSD([subQ15,subQ2]),TDD([makeQuery(id+"F2.opExtrude","CAP_VERTEX",VERTEX,{"disambiguationData":[OSD([subQ15,subQ2])],"isStart":false})])]})]});var subQ17=sQuery(id+"F5.wireOp",EDGE,"E5");var subQ18=sQuery(id+"F5.wireOp",EDGE,"E3");var subQ19=sQuery(id+"F5.wireOp",EDGE,"E8");var subQ20=makeQuery(id+"F3.opExtrude","SWEPT_FACE",FACE,{"disambiguationData":[OSD([subQ3,subQ4])]});var subQ21=makeQuery(id+"F4.boolean.opBoolean","MERGE",EDGE,{"derivedFrom":[makeQuery(id+"F3.boolean.opBoolean","MERGE",EDGE,{"derivedFrom":[makeQuery(id+"F1.opExtrude","CAP_EDGE",EDGE,{"disambiguationData":[OSD([subQ15])],"isStart":false}),makeQuery(id+"F3.opExtrude","SWEPT_EDGE",EDGE,{"disambiguationData":[OSD([subQ15,subQ4]),TDD([makeQuery(id+"F1.opExtrude","CAP_VERTEX",VERTEX,{"disambiguationData":[OSD([subQ15,subQ4])],"isStart":false})])]})]}),makeQuery(id+"F4.opExtrude","SWEPT_EDGE",EDGE,{"disambiguationData":[OSD([subQ15,subQ2]),TDD([makeQuery(id+"F1.opExtrude","CAP_VERTEX",VERTEX,{"disambiguationData":[OSD([subQ15,subQ2])],"isStart":false})])]})]});var subQ22=makeQuery(id+"F1.opExtrude","SWEPT_FACE",FACE,{"disambiguationData":[OSD([subQ3])]});var subQ23=makeQuery(id+"F4.opExtrude","SWEPT_FACE",FACE,{"disambiguationData":[OSD([subQ3,subQ2])]});Q8=makeQuery(id+"F9.boolean.opBoolean","SPLIT",FACE,{"disambiguationData":[TD([makeQuery(id+"F1.opExtrude","CAP_FACE",FACE,{"disambiguationData":[OSD([subQ15,subQ3,subQ4,subQ2])],"isStart":false}),subQ22,subQ10,makeQuery(id+"F2.opExtrude","CAP_FACE",FACE,{"disambiguationData":[OSD([subQ15,subQ3,subQ4,subQ2])],"isStart":false}),makeQuery(id+"F3.opExtrude","SWEPT_FACE",FACE,{"disambiguationData":[OSD([subQ4]),TDD([makeQuery(id+"F1.opExtrude","CAP_EDGE",EDGE,{"disambiguationData":[OSD([subQ4])],"isStart":false})])]}),makeQuery(id+"F3.opExtrude","SWEPT_FACE",FACE,{"disambiguationData":[OSD([subQ4]),TDD([makeQuery(id+"F2.opExtrude","CAP_EDGE",EDGE,{"disambiguationData":[OSD([subQ4])],"isStart":false})])]}),subQ20,makeQuery(id+"F4.opExtrude","SWEPT_FACE",FACE,{"disambiguationData":[OSD([subQ2]),TDD([makeQuery(id+"F1.opExtrude","CAP_EDGE",EDGE,{"disambiguationData":[OSD([subQ2])],"isStart":false})])]}),makeQuery(id+"F4.opExtrude","SWEPT_FACE",FACE,{"disambiguationData":[OSD([subQ2]),TDD([makeQuery(id+"F2.opExtrude","CAP_EDGE",EDGE,{"disambiguationData":[OSD([subQ2])],"isStart":false})])]}),subQ23,makeQuery(id+"F7.opExtrude","SWEPT_FACE",FACE,{"disambiguationData":[OSD([subQ15,subQ4,subQ2]),TDD([makeQuery(id+"F5.imprint","IMPRINT",EDGE,{"disambiguationData":[TD([[makeQuery(id+"F5.imprint","INTERSECT",VERTEX,{"derivedFrom":[subQ21,subQ18,sQuery(id+"F5.wireOp",EDGE,"E4")]}),1.0]])],"derivedFrom":subQ21})])]}),makeQuery(id+"F7.opExtrude","SWEPT_FACE",FACE,{"disambiguationData":[OSD([subQ15,subQ4,subQ2]),TDD([makeQuery(id+"F5.imprint","IMPRINT",EDGE,{"disambiguationData":[TD([[makeQuery(id+"F5.imprint","INTERSECT",VERTEX,{"derivedFrom":[subQ21,subQ17,sQuery(id+"F5.wireOp",EDGE,"E6")]}),-1.0]])],"derivedFrom":subQ21})])]}),makeQuery(id+"F7.opExtrude","SWEPT_FACE",FACE,{"disambiguationData":[OSD([subQ15,subQ4,subQ2]),TDD([makeQuery(id+"F5.imprint","IMPRINT",EDGE,{"disambiguationData":[TD([[makeQuery(id+"F5.imprint","INTERSECT",VERTEX,{"derivedFrom":[subQ16,sQuery(id+"F5.wireOp",EDGE,"E1"),subQ17]}),1.0]])],"derivedFrom":subQ16})])]}),makeQuery(id+"F7.opExtrude","SWEPT_FACE",FACE,{"disambiguationData":[OSD([subQ15,subQ4,subQ2]),TDD([makeQuery(id+"F5.imprint","IMPRINT",EDGE,{"disambiguationData":[TD([[makeQuery(id+"F5.imprint","INTERSECT",VERTEX,{"derivedFrom":[subQ16,subQ19,sQuery(id+"F5.wireOp",EDGE,"E9")]}),-1.0]])],"derivedFrom":subQ16})])]}),makeQuery(id+"F7.opExtrude","SWEPT_FACE",FACE,{"disambiguationData":[OSD([subQ15,subQ4,subQ2]),TDD([makeQuery(id+"F5.imprint","IMPRINT",EDGE,{"disambiguationData":[TD([[makeQuery(id+"F5.imprint","INTERSECT",VERTEX,{"derivedFrom":[subQ16,subQ14,sQuery(id+"F5.wireOp",EDGE,"E14")]}),1.0]])],"derivedFrom":subQ16})])]}),makeQuery(id+"F9.opExtrude","SWEPT_FACE",FACE,{"disambiguationData":[OSD([subQ1])]}),makeQuery(id+"F9.opExtrude","SWEPT_FACE",FACE,{"disambiguationData":[OSD([subQ12])]}),makeQuery(id+"F9.opExtrude","SWEPT_FACE",FACE,{"disambiguationData":[OSD([subQ11])]}),makeQuery(id+"F9.opExtrude","SWEPT_FACE",FACE,{"disambiguationData":[OSD([subQ7])]}),makeQuery(id+"F9.opExtrude","SWEPT_FACE",FACE,{"disambiguationData":[OSD([subQ3,subQ4,subQ2]),TDD([makeQuery(id+"F6.imprint","IMPRINT",EDGE,{"disambiguationData":[TD([[makeQuery(id+"F6.imprint","INTERSECT",VERTEX,{"derivedFrom":[subQ8,subQ0,subQ12]}),1.0]])],"derivedFrom":subQ8})])]}),makeQuery(id+"F9.opExtrude","SWEPT_FACE",FACE,{"disambiguationData":[OSD([subQ3,subQ4,subQ2]),TDD([makeQuery(id+"F6.imprint","IMPRINT",EDGE,{"disambiguationData":[TD([[makeQuery(id+"F6.imprint","INTERSECT",VERTEX,{"derivedFrom":[subQ8,subQ6,sQuery(id+"F6.wireOp",EDGE,"E27")]}),-1.0]])],"derivedFrom":subQ8})])]}),makeQuery(id+"F9.opExtrude","SWEPT_FACE",FACE,{"disambiguationData":[OSD([subQ3,subQ4,subQ2]),TDD([makeQuery(id+"F6.imprint","IMPRINT",EDGE,{"disambiguationData":[TD([[makeQuery(id+"F6.imprint","INTERSECT",VERTEX,{"derivedFrom":[subQ5,subQ1,subQ0]}),-1.0]])],"derivedFrom":subQ5})])]}),makeQuery(id+"F9.opExtrude","SWEPT_FACE",FACE,{"disambiguationData":[OSD([subQ3,subQ4,subQ2]),TDD([makeQuery(id+"F6.imprint","IMPRINT",EDGE,{"disambiguationData":[TD([[makeQuery(id+"F6.imprint","INTERSECT",VERTEX,{"derivedFrom":[subQ5,subQ13,sQuery(id+"F6.wireOp",EDGE,"E22")]}),1.0]])],"derivedFrom":subQ5})])]}),makeQuery(id+"F9.opExtrude","SWEPT_FACE",FACE,{"disambiguationData":[OSD([subQ3,subQ4,subQ2]),TDD([makeQuery(id+"F6.imprint","IMPRINT",EDGE,{"disambiguationData":[TD([[makeQuery(id+"F6.imprint","INTERSECT",VERTEX,{"derivedFrom":[subQ5,subQ9,sQuery(id+"F6.wireOp",EDGE,"E30")]}),-1.0]])],"derivedFrom":subQ5})])]})])],"derivedFrom":makeQuery(id+"F4.boolean.opBoolean","MERGE",FACE,{"derivedFrom":[makeQuery(id+"F3.boolean.opBoolean","MERGE",FACE,{"derivedFrom":[makeQuery(id+"F2.boolean.opBoolean","MERGE",FACE,{"derivedFrom":[subQ22,subQ10]}),subQ20]}),subQ23]})});}
            var Q9;
            {var subQ0=sQuery(id+"F6.wireOp",EDGE,"E18");var subQ1=sQuery(id+"F6.wireOp",EDGE,"E17");var subQ2=sQuery(id+"F0.wireOp",EDGE,"E0.right");var subQ3=sQuery(id+"F0.wireOp",EDGE,"E0.top");var subQ4=sQuery(id+"F0.wireOp",EDGE,"E0.left");var subQ5=makeQuery(id+"F4.boolean.opBoolean","MERGE",EDGE,{"derivedFrom":[makeQuery(id+"F3.boolean.opBoolean","MERGE",EDGE,{"derivedFrom":[makeQuery(id+"F2.opExtrude","CAP_EDGE",EDGE,{"disambiguationData":[OSD([subQ3])],"isStart":false}),makeQuery(id+"F3.opExtrude","SWEPT_EDGE",EDGE,{"disambiguationData":[OSD([subQ3,subQ4]),TDD([makeQuery(id+"F2.opExtrude","CAP_VERTEX",VERTEX,{"disambiguationData":[OSD([subQ3,subQ4])],"isStart":false})])]})]}),makeQuery(id+"F4.opExtrude","SWEPT_EDGE",EDGE,{"disambiguationData":[OSD([subQ3,subQ2]),TDD([makeQuery(id+"F2.opExtrude","CAP_VERTEX",VERTEX,{"disambiguationData":[OSD([subQ3,subQ2])],"isStart":false})])]})]});var subQ6=sQuery(id+"F6.wireOp",EDGE,"E26");var subQ7=sQuery(id+"F6.wireOp",EDGE,"E25");var subQ8=sQuery(id+"F6.wireOp",EDGE,"E27");var subQ9=makeQuery(id+"F4.boolean.opBoolean","MERGE",EDGE,{"derivedFrom":[makeQuery(id+"F3.boolean.opBoolean","MERGE",EDGE,{"derivedFrom":[makeQuery(id+"F1.opExtrude","CAP_EDGE",EDGE,{"disambiguationData":[OSD([subQ3])],"isStart":false}),makeQuery(id+"F3.opExtrude","SWEPT_EDGE",EDGE,{"disambiguationData":[OSD([subQ3,subQ4]),TDD([makeQuery(id+"F1.opExtrude","CAP_VERTEX",VERTEX,{"disambiguationData":[OSD([subQ3,subQ4])],"isStart":false})])]})]}),makeQuery(id+"F4.opExtrude","SWEPT_EDGE",EDGE,{"disambiguationData":[OSD([subQ3,subQ2]),TDD([makeQuery(id+"F1.opExtrude","CAP_VERTEX",VERTEX,{"disambiguationData":[OSD([subQ3,subQ2])],"isStart":false})])]})]});var subQ10=sQuery(id+"F6.wireOp",EDGE,"E29");var subQ11=sQuery(id+"F6.wireOp",EDGE,"E28");var subQ12=makeQuery(id+"F2.opExtrude","SWEPT_FACE",FACE,{"disambiguationData":[OSD([subQ3])]});var subQ13=sQuery(id+"F6.wireOp",EDGE,"E21");var subQ14=sQuery(id+"F5.wireOp",EDGE,"E13");var subQ15=sQuery(id+"F0.wireOp",EDGE,"E0.bottom");var subQ16=makeQuery(id+"F4.boolean.opBoolean","MERGE",EDGE,{"derivedFrom":[makeQuery(id+"F3.boolean.opBoolean","MERGE",EDGE,{"derivedFrom":[makeQuery(id+"F2.opExtrude","CAP_EDGE",EDGE,{"disambiguationData":[OSD([subQ15])],"isStart":false}),makeQuery(id+"F3.opExtrude","SWEPT_EDGE",EDGE,{"disambiguationData":[OSD([subQ15,subQ4]),TDD([makeQuery(id+"F2.opExtrude","CAP_VERTEX",VERTEX,{"disambiguationData":[OSD([subQ15,subQ4])],"isStart":false})])]})]}),makeQuery(id+"F4.opExtrude","SWEPT_EDGE",EDGE,{"disambiguationData":[OSD([subQ15,subQ2]),TDD([makeQuery(id+"F2.opExtrude","CAP_VERTEX",VERTEX,{"disambiguationData":[OSD([subQ15,subQ2])],"isStart":false})])]})]});var subQ17=sQuery(id+"F5.wireOp",EDGE,"E5");var subQ18=sQuery(id+"F5.wireOp",EDGE,"E3");var subQ19=sQuery(id+"F5.wireOp",EDGE,"E8");var subQ20=makeQuery(id+"F3.opExtrude","SWEPT_FACE",FACE,{"disambiguationData":[OSD([subQ3,subQ4])]});var subQ21=makeQuery(id+"F4.boolean.opBoolean","MERGE",EDGE,{"derivedFrom":[makeQuery(id+"F3.boolean.opBoolean","MERGE",EDGE,{"derivedFrom":[makeQuery(id+"F1.opExtrude","CAP_EDGE",EDGE,{"disambiguationData":[OSD([subQ15])],"isStart":false}),makeQuery(id+"F3.opExtrude","SWEPT_EDGE",EDGE,{"disambiguationData":[OSD([subQ15,subQ4]),TDD([makeQuery(id+"F1.opExtrude","CAP_VERTEX",VERTEX,{"disambiguationData":[OSD([subQ15,subQ4])],"isStart":false})])]})]}),makeQuery(id+"F4.opExtrude","SWEPT_EDGE",EDGE,{"disambiguationData":[OSD([subQ15,subQ2]),TDD([makeQuery(id+"F1.opExtrude","CAP_VERTEX",VERTEX,{"disambiguationData":[OSD([subQ15,subQ2])],"isStart":false})])]})]});var subQ22=makeQuery(id+"F1.opExtrude","SWEPT_FACE",FACE,{"disambiguationData":[OSD([subQ3])]});var subQ23=makeQuery(id+"F4.opExtrude","SWEPT_FACE",FACE,{"disambiguationData":[OSD([subQ3,subQ2])]});Q9=makeQuery(id+"F9.boolean.opBoolean","SPLIT",FACE,{"disambiguationData":[TD([makeQuery(id+"F1.opExtrude","CAP_FACE",FACE,{"disambiguationData":[OSD([subQ15,subQ3,subQ4,subQ2])],"isStart":false}),subQ22,subQ12,makeQuery(id+"F2.opExtrude","CAP_FACE",FACE,{"disambiguationData":[OSD([subQ15,subQ3,subQ4,subQ2])],"isStart":false}),makeQuery(id+"F3.opExtrude","SWEPT_FACE",FACE,{"disambiguationData":[OSD([subQ4]),TDD([makeQuery(id+"F1.opExtrude","CAP_EDGE",EDGE,{"disambiguationData":[OSD([subQ4])],"isStart":false})])]}),makeQuery(id+"F3.opExtrude","SWEPT_FACE",FACE,{"disambiguationData":[OSD([subQ4]),TDD([makeQuery(id+"F2.opExtrude","CAP_EDGE",EDGE,{"disambiguationData":[OSD([subQ4])],"isStart":false})])]}),subQ20,makeQuery(id+"F4.opExtrude","SWEPT_FACE",FACE,{"disambiguationData":[OSD([subQ2]),TDD([makeQuery(id+"F1.opExtrude","CAP_EDGE",EDGE,{"disambiguationData":[OSD([subQ2])],"isStart":false})])]}),makeQuery(id+"F4.opExtrude","SWEPT_FACE",FACE,{"disambiguationData":[OSD([subQ2]),TDD([makeQuery(id+"F2.opExtrude","CAP_EDGE",EDGE,{"disambiguationData":[OSD([subQ2])],"isStart":false})])]}),subQ23,makeQuery(id+"F7.opExtrude","SWEPT_FACE",FACE,{"disambiguationData":[OSD([subQ15,subQ4,subQ2]),TDD([makeQuery(id+"F5.imprint","IMPRINT",EDGE,{"disambiguationData":[TD([[makeQuery(id+"F5.imprint","INTERSECT",VERTEX,{"derivedFrom":[subQ21,subQ18,sQuery(id+"F5.wireOp",EDGE,"E4")]}),1.0]])],"derivedFrom":subQ21})])]}),makeQuery(id+"F7.opExtrude","SWEPT_FACE",FACE,{"disambiguationData":[OSD([subQ15,subQ4,subQ2]),TDD([makeQuery(id+"F5.imprint","IMPRINT",EDGE,{"disambiguationData":[TD([[makeQuery(id+"F5.imprint","INTERSECT",VERTEX,{"derivedFrom":[subQ21,subQ17,sQuery(id+"F5.wireOp",EDGE,"E6")]}),-1.0]])],"derivedFrom":subQ21})])]}),makeQuery(id+"F7.opExtrude","SWEPT_FACE",FACE,{"disambiguationData":[OSD([subQ15,subQ4,subQ2]),TDD([makeQuery(id+"F5.imprint","IMPRINT",EDGE,{"disambiguationData":[TD([[makeQuery(id+"F5.imprint","INTERSECT",VERTEX,{"derivedFrom":[subQ16,sQuery(id+"F5.wireOp",EDGE,"E1"),subQ17]}),1.0]])],"derivedFrom":subQ16})])]}),makeQuery(id+"F7.opExtrude","SWEPT_FACE",FACE,{"disambiguationData":[OSD([subQ15,subQ4,subQ2]),TDD([makeQuery(id+"F5.imprint","IMPRINT",EDGE,{"disambiguationData":[TD([[makeQuery(id+"F5.imprint","INTERSECT",VERTEX,{"derivedFrom":[subQ16,subQ19,sQuery(id+"F5.wireOp",EDGE,"E9")]}),-1.0]])],"derivedFrom":subQ16})])]}),makeQuery(id+"F7.opExtrude","SWEPT_FACE",FACE,{"disambiguationData":[OSD([subQ15,subQ4,subQ2]),TDD([makeQuery(id+"F5.imprint","IMPRINT",EDGE,{"disambiguationData":[TD([[makeQuery(id+"F5.imprint","INTERSECT",VERTEX,{"derivedFrom":[subQ16,subQ14,sQuery(id+"F5.wireOp",EDGE,"E14")]}),1.0]])],"derivedFrom":subQ16})])]}),makeQuery(id+"F9.opExtrude","SWEPT_FACE",FACE,{"disambiguationData":[OSD([subQ1])]}),makeQuery(id+"F9.opExtrude","SWEPT_FACE",FACE,{"disambiguationData":[OSD([subQ7])]}),makeQuery(id+"F9.opExtrude","SWEPT_FACE",FACE,{"disambiguationData":[OSD([subQ8])]}),makeQuery(id+"F9.opExtrude","SWEPT_FACE",FACE,{"disambiguationData":[OSD([subQ11])]}),makeQuery(id+"F9.opExtrude","SWEPT_FACE",FACE,{"disambiguationData":[OSD([subQ3,subQ4,subQ2]),TDD([makeQuery(id+"F6.imprint","IMPRINT",EDGE,{"disambiguationData":[TD([[makeQuery(id+"F6.imprint","INTERSECT",VERTEX,{"derivedFrom":[subQ9,subQ0,sQuery(id+"F6.wireOp",EDGE,"E19")]}),1.0]])],"derivedFrom":subQ9})])]}),makeQuery(id+"F9.opExtrude","SWEPT_FACE",FACE,{"disambiguationData":[OSD([subQ3,subQ4,subQ2]),TDD([makeQuery(id+"F6.imprint","IMPRINT",EDGE,{"disambiguationData":[TD([[makeQuery(id+"F6.imprint","INTERSECT",VERTEX,{"derivedFrom":[subQ9,subQ6,subQ8]}),-1.0]])],"derivedFrom":subQ9})])]}),makeQuery(id+"F9.opExtrude","SWEPT_FACE",FACE,{"disambiguationData":[OSD([subQ3,subQ4,subQ2]),TDD([makeQuery(id+"F6.imprint","IMPRINT",EDGE,{"disambiguationData":[TD([[makeQuery(id+"F6.imprint","INTERSECT",VERTEX,{"derivedFrom":[subQ5,subQ1,subQ0]}),-1.0]])],"derivedFrom":subQ5})])]}),makeQuery(id+"F9.opExtrude","SWEPT_FACE",FACE,{"disambiguationData":[OSD([subQ3,subQ4,subQ2]),TDD([makeQuery(id+"F6.imprint","IMPRINT",EDGE,{"disambiguationData":[TD([[makeQuery(id+"F6.imprint","INTERSECT",VERTEX,{"derivedFrom":[subQ5,subQ13,sQuery(id+"F6.wireOp",EDGE,"E22")]}),1.0]])],"derivedFrom":subQ5})])]}),makeQuery(id+"F9.opExtrude","SWEPT_FACE",FACE,{"disambiguationData":[OSD([subQ3,subQ4,subQ2]),TDD([makeQuery(id+"F6.imprint","IMPRINT",EDGE,{"disambiguationData":[TD([[makeQuery(id+"F6.imprint","INTERSECT",VERTEX,{"derivedFrom":[subQ5,subQ10,sQuery(id+"F6.wireOp",EDGE,"E30")]}),-1.0]])],"derivedFrom":subQ5})])]})])],"derivedFrom":makeQuery(id+"F4.boolean.opBoolean","MERGE",FACE,{"derivedFrom":[makeQuery(id+"F3.boolean.opBoolean","MERGE",FACE,{"derivedFrom":[makeQuery(id+"F2.boolean.opBoolean","MERGE",FACE,{"derivedFrom":[subQ22,subQ12]}),subQ20]}),subQ23]})});}
            var Q10;
            {var subQ0=sQuery(id+"F6.wireOp",EDGE,"E18");var subQ1=sQuery(id+"F0.wireOp",EDGE,"E0.right");var subQ2=sQuery(id+"F0.wireOp",EDGE,"E0.top");var subQ3=sQuery(id+"F0.wireOp",EDGE,"E0.left");var subQ4=makeQuery(id+"F4.boolean.opBoolean","MERGE",EDGE,{"derivedFrom":[makeQuery(id+"F3.boolean.opBoolean","MERGE",EDGE,{"derivedFrom":[makeQuery(id+"F2.opExtrude","CAP_EDGE",EDGE,{"disambiguationData":[OSD([subQ2])],"isStart":false}),makeQuery(id+"F3.opExtrude","SWEPT_EDGE",EDGE,{"disambiguationData":[OSD([subQ2,subQ3]),TDD([makeQuery(id+"F2.opExtrude","CAP_VERTEX",VERTEX,{"disambiguationData":[OSD([subQ2,subQ3])],"isStart":false})])]})]}),makeQuery(id+"F4.opExtrude","SWEPT_EDGE",EDGE,{"disambiguationData":[OSD([subQ2,subQ1]),TDD([makeQuery(id+"F2.opExtrude","CAP_VERTEX",VERTEX,{"disambiguationData":[OSD([subQ2,subQ1])],"isStart":false})])]})]});var subQ5=sQuery(id+"F6.wireOp",EDGE,"E26");var subQ6=sQuery(id+"F6.wireOp",EDGE,"E27");var subQ7=makeQuery(id+"F4.boolean.opBoolean","MERGE",EDGE,{"derivedFrom":[makeQuery(id+"F3.boolean.opBoolean","MERGE",EDGE,{"derivedFrom":[makeQuery(id+"F1.opExtrude","CAP_EDGE",EDGE,{"disambiguationData":[OSD([subQ2])],"isStart":false}),makeQuery(id+"F3.opExtrude","SWEPT_EDGE",EDGE,{"disambiguationData":[OSD([subQ2,subQ3]),TDD([makeQuery(id+"F1.opExtrude","CAP_VERTEX",VERTEX,{"disambiguationData":[OSD([subQ2,subQ3])],"isStart":false})])]})]}),makeQuery(id+"F4.opExtrude","SWEPT_EDGE",EDGE,{"disambiguationData":[OSD([subQ2,subQ1]),TDD([makeQuery(id+"F1.opExtrude","CAP_VERTEX",VERTEX,{"disambiguationData":[OSD([subQ2,subQ1])],"isStart":false})])]})]});var subQ8=sQuery(id+"F6.wireOp",EDGE,"E29");var subQ9=sQuery(id+"F6.wireOp",EDGE,"E28");var subQ10=makeQuery(id+"F2.opExtrude","SWEPT_FACE",FACE,{"disambiguationData":[OSD([subQ2])]});var subQ11=sQuery(id+"F6.wireOp",EDGE,"E21");var subQ12=sQuery(id+"F5.wireOp",EDGE,"E13");var subQ13=sQuery(id+"F0.wireOp",EDGE,"E0.bottom");var subQ14=makeQuery(id+"F4.boolean.opBoolean","MERGE",EDGE,{"derivedFrom":[makeQuery(id+"F3.boolean.opBoolean","MERGE",EDGE,{"derivedFrom":[makeQuery(id+"F2.opExtrude","CAP_EDGE",EDGE,{"disambiguationData":[OSD([subQ13])],"isStart":false}),makeQuery(id+"F3.opExtrude","SWEPT_EDGE",EDGE,{"disambiguationData":[OSD([subQ13,subQ3]),TDD([makeQuery(id+"F2.opExtrude","CAP_VERTEX",VERTEX,{"disambiguationData":[OSD([subQ13,subQ3])],"isStart":false})])]})]}),makeQuery(id+"F4.opExtrude","SWEPT_EDGE",EDGE,{"disambiguationData":[OSD([subQ13,subQ1]),TDD([makeQuery(id+"F2.opExtrude","CAP_VERTEX",VERTEX,{"disambiguationData":[OSD([subQ13,subQ1])],"isStart":false})])]})]});var subQ15=sQuery(id+"F5.wireOp",EDGE,"E5");var subQ16=sQuery(id+"F5.wireOp",EDGE,"E3");var subQ17=sQuery(id+"F6.wireOp",EDGE,"E31");var subQ18=sQuery(id+"F5.wireOp",EDGE,"E8");var subQ19=makeQuery(id+"F3.opExtrude","SWEPT_FACE",FACE,{"disambiguationData":[OSD([subQ2,subQ3])]});var subQ20=sQuery(id+"F6.wireOp",EDGE,"E30");var subQ21=makeQuery(id+"F4.boolean.opBoolean","MERGE",EDGE,{"derivedFrom":[makeQuery(id+"F3.boolean.opBoolean","MERGE",EDGE,{"derivedFrom":[makeQuery(id+"F1.opExtrude","CAP_EDGE",EDGE,{"disambiguationData":[OSD([subQ13])],"isStart":false}),makeQuery(id+"F3.opExtrude","SWEPT_EDGE",EDGE,{"disambiguationData":[OSD([subQ13,subQ3]),TDD([makeQuery(id+"F1.opExtrude","CAP_VERTEX",VERTEX,{"disambiguationData":[OSD([subQ13,subQ3])],"isStart":false})])]})]}),makeQuery(id+"F4.opExtrude","SWEPT_EDGE",EDGE,{"disambiguationData":[OSD([subQ13,subQ1]),TDD([makeQuery(id+"F1.opExtrude","CAP_VERTEX",VERTEX,{"disambiguationData":[OSD([subQ13,subQ1])],"isStart":false})])]})]});var subQ22=makeQuery(id+"F1.opExtrude","SWEPT_FACE",FACE,{"disambiguationData":[OSD([subQ2])]});var subQ23=makeQuery(id+"F4.opExtrude","SWEPT_FACE",FACE,{"disambiguationData":[OSD([subQ2,subQ1])]});Q10=makeQuery(id+"F9.boolean.opBoolean","SPLIT",FACE,{"disambiguationData":[TD([makeQuery(id+"F1.opExtrude","CAP_FACE",FACE,{"disambiguationData":[OSD([subQ13,subQ2,subQ3,subQ1])],"isStart":false}),subQ22,subQ10,makeQuery(id+"F2.opExtrude","CAP_FACE",FACE,{"disambiguationData":[OSD([subQ13,subQ2,subQ3,subQ1])],"isStart":false}),makeQuery(id+"F3.opExtrude","SWEPT_FACE",FACE,{"disambiguationData":[OSD([subQ3]),TDD([makeQuery(id+"F1.opExtrude","CAP_EDGE",EDGE,{"disambiguationData":[OSD([subQ3])],"isStart":false})])]}),makeQuery(id+"F3.opExtrude","SWEPT_FACE",FACE,{"disambiguationData":[OSD([subQ3]),TDD([makeQuery(id+"F2.opExtrude","CAP_EDGE",EDGE,{"disambiguationData":[OSD([subQ3])],"isStart":false})])]}),subQ19,makeQuery(id+"F4.opExtrude","SWEPT_FACE",FACE,{"disambiguationData":[OSD([subQ1]),TDD([makeQuery(id+"F1.opExtrude","CAP_EDGE",EDGE,{"disambiguationData":[OSD([subQ1])],"isStart":false})])]}),makeQuery(id+"F4.opExtrude","SWEPT_FACE",FACE,{"disambiguationData":[OSD([subQ1]),TDD([makeQuery(id+"F2.opExtrude","CAP_EDGE",EDGE,{"disambiguationData":[OSD([subQ1])],"isStart":false})])]}),subQ23,makeQuery(id+"F7.opExtrude","SWEPT_FACE",FACE,{"disambiguationData":[OSD([subQ13,subQ3,subQ1]),TDD([makeQuery(id+"F5.imprint","IMPRINT",EDGE,{"disambiguationData":[TD([[makeQuery(id+"F5.imprint","INTERSECT",VERTEX,{"derivedFrom":[subQ21,subQ16,sQuery(id+"F5.wireOp",EDGE,"E4")]}),1.0]])],"derivedFrom":subQ21})])]}),makeQuery(id+"F7.opExtrude","SWEPT_FACE",FACE,{"disambiguationData":[OSD([subQ13,subQ3,subQ1]),TDD([makeQuery(id+"F5.imprint","IMPRINT",EDGE,{"disambiguationData":[TD([[makeQuery(id+"F5.imprint","INTERSECT",VERTEX,{"derivedFrom":[subQ21,subQ15,sQuery(id+"F5.wireOp",EDGE,"E6")]}),-1.0]])],"derivedFrom":subQ21})])]}),makeQuery(id+"F7.opExtrude","SWEPT_FACE",FACE,{"disambiguationData":[OSD([subQ13,subQ3,subQ1]),TDD([makeQuery(id+"F5.imprint","IMPRINT",EDGE,{"disambiguationData":[TD([[makeQuery(id+"F5.imprint","INTERSECT",VERTEX,{"derivedFrom":[subQ14,sQuery(id+"F5.wireOp",EDGE,"E1"),subQ15]}),1.0]])],"derivedFrom":subQ14})])]}),makeQuery(id+"F7.opExtrude","SWEPT_FACE",FACE,{"disambiguationData":[OSD([subQ13,subQ3,subQ1]),TDD([makeQuery(id+"F5.imprint","IMPRINT",EDGE,{"disambiguationData":[TD([[makeQuery(id+"F5.imprint","INTERSECT",VERTEX,{"derivedFrom":[subQ14,subQ18,sQuery(id+"F5.wireOp",EDGE,"E9")]}),-1.0]])],"derivedFrom":subQ14})])]}),makeQuery(id+"F7.opExtrude","SWEPT_FACE",FACE,{"disambiguationData":[OSD([subQ13,subQ3,subQ1]),TDD([makeQuery(id+"F5.imprint","IMPRINT",EDGE,{"disambiguationData":[TD([[makeQuery(id+"F5.imprint","INTERSECT",VERTEX,{"derivedFrom":[subQ14,subQ12,sQuery(id+"F5.wireOp",EDGE,"E14")]}),1.0]])],"derivedFrom":subQ14})])]}),makeQuery(id+"F9.opExtrude","SWEPT_FACE",FACE,{"disambiguationData":[OSD([subQ6])]}),makeQuery(id+"F9.opExtrude","SWEPT_FACE",FACE,{"disambiguationData":[OSD([subQ9])]}),makeQuery(id+"F9.opExtrude","SWEPT_FACE",FACE,{"disambiguationData":[OSD([subQ20])]}),makeQuery(id+"F9.opExtrude","SWEPT_FACE",FACE,{"disambiguationData":[OSD([subQ17])]}),makeQuery(id+"F9.opExtrude","SWEPT_FACE",FACE,{"disambiguationData":[OSD([subQ2,subQ3,subQ1]),TDD([makeQuery(id+"F6.imprint","IMPRINT",EDGE,{"disambiguationData":[TD([[makeQuery(id+"F6.imprint","INTERSECT",VERTEX,{"derivedFrom":[subQ7,subQ0,sQuery(id+"F6.wireOp",EDGE,"E19")]}),1.0]])],"derivedFrom":subQ7})])]}),makeQuery(id+"F9.opExtrude","SWEPT_FACE",FACE,{"disambiguationData":[OSD([subQ2,subQ3,subQ1]),TDD([makeQuery(id+"F6.imprint","IMPRINT",EDGE,{"disambiguationData":[TD([[makeQuery(id+"F6.imprint","INTERSECT",VERTEX,{"derivedFrom":[subQ7,subQ5,subQ6]}),-1.0]])],"derivedFrom":subQ7})])]}),makeQuery(id+"F9.opExtrude","SWEPT_FACE",FACE,{"disambiguationData":[OSD([subQ2,subQ3,subQ1]),TDD([makeQuery(id+"F6.imprint","IMPRINT",EDGE,{"disambiguationData":[TD([[makeQuery(id+"F6.imprint","INTERSECT",VERTEX,{"derivedFrom":[subQ4,sQuery(id+"F6.wireOp",EDGE,"E17"),subQ0]}),-1.0]])],"derivedFrom":subQ4})])]}),makeQuery(id+"F9.opExtrude","SWEPT_FACE",FACE,{"disambiguationData":[OSD([subQ2,subQ3,subQ1]),TDD([makeQuery(id+"F6.imprint","IMPRINT",EDGE,{"disambiguationData":[TD([[makeQuery(id+"F6.imprint","INTERSECT",VERTEX,{"derivedFrom":[subQ4,subQ11,sQuery(id+"F6.wireOp",EDGE,"E22")]}),1.0]])],"derivedFrom":subQ4})])]}),makeQuery(id+"F9.opExtrude","SWEPT_FACE",FACE,{"disambiguationData":[OSD([subQ2,subQ3,subQ1]),TDD([makeQuery(id+"F6.imprint","IMPRINT",EDGE,{"disambiguationData":[TD([[makeQuery(id+"F6.imprint","INTERSECT",VERTEX,{"derivedFrom":[subQ4,subQ8,subQ20]}),-1.0]])],"derivedFrom":subQ4})])]})])],"derivedFrom":makeQuery(id+"F4.boolean.opBoolean","MERGE",FACE,{"derivedFrom":[makeQuery(id+"F3.boolean.opBoolean","MERGE",FACE,{"derivedFrom":[makeQuery(id+"F2.boolean.opBoolean","MERGE",FACE,{"derivedFrom":[subQ22,subQ10]}),subQ19]}),subQ23]})});}
            var Q11;
            {var subQ0=sQuery(id+"F6.wireOp",EDGE,"E18");var subQ1=sQuery(id+"F0.wireOp",EDGE,"E0.right");var subQ2=sQuery(id+"F0.wireOp",EDGE,"E0.top");var subQ3=sQuery(id+"F0.wireOp",EDGE,"E0.left");var subQ4=makeQuery(id+"F4.boolean.opBoolean","MERGE",EDGE,{"derivedFrom":[makeQuery(id+"F3.boolean.opBoolean","MERGE",EDGE,{"derivedFrom":[makeQuery(id+"F2.opExtrude","CAP_EDGE",EDGE,{"disambiguationData":[OSD([subQ2])],"isStart":false}),makeQuery(id+"F3.opExtrude","SWEPT_EDGE",EDGE,{"disambiguationData":[OSD([subQ2,subQ3]),TDD([makeQuery(id+"F2.opExtrude","CAP_VERTEX",VERTEX,{"disambiguationData":[OSD([subQ2,subQ3])],"isStart":false})])]})]}),makeQuery(id+"F4.opExtrude","SWEPT_EDGE",EDGE,{"disambiguationData":[OSD([subQ2,subQ1]),TDD([makeQuery(id+"F2.opExtrude","CAP_VERTEX",VERTEX,{"disambiguationData":[OSD([subQ2,subQ1])],"isStart":false})])]})]});var subQ5=sQuery(id+"F6.wireOp",EDGE,"E26");var subQ6=makeQuery(id+"F4.boolean.opBoolean","MERGE",EDGE,{"derivedFrom":[makeQuery(id+"F3.boolean.opBoolean","MERGE",EDGE,{"derivedFrom":[makeQuery(id+"F1.opExtrude","CAP_EDGE",EDGE,{"disambiguationData":[OSD([subQ2])],"isStart":false}),makeQuery(id+"F3.opExtrude","SWEPT_EDGE",EDGE,{"disambiguationData":[OSD([subQ2,subQ3]),TDD([makeQuery(id+"F1.opExtrude","CAP_VERTEX",VERTEX,{"disambiguationData":[OSD([subQ2,subQ3])],"isStart":false})])]})]}),makeQuery(id+"F4.opExtrude","SWEPT_EDGE",EDGE,{"disambiguationData":[OSD([subQ2,subQ1]),TDD([makeQuery(id+"F1.opExtrude","CAP_VERTEX",VERTEX,{"disambiguationData":[OSD([subQ2,subQ1])],"isStart":false})])]})]});var subQ7=sQuery(id+"F6.wireOp",EDGE,"E29");var subQ8=makeQuery(id+"F2.opExtrude","SWEPT_FACE",FACE,{"disambiguationData":[OSD([subQ2])]});var subQ9=sQuery(id+"F6.wireOp",EDGE,"E21");var subQ10=sQuery(id+"F5.wireOp",EDGE,"E13");var subQ11=sQuery(id+"F0.wireOp",EDGE,"E0.bottom");var subQ12=makeQuery(id+"F4.boolean.opBoolean","MERGE",EDGE,{"derivedFrom":[makeQuery(id+"F3.boolean.opBoolean","MERGE",EDGE,{"derivedFrom":[makeQuery(id+"F2.opExtrude","CAP_EDGE",EDGE,{"disambiguationData":[OSD([subQ11])],"isStart":false}),makeQuery(id+"F3.opExtrude","SWEPT_EDGE",EDGE,{"disambiguationData":[OSD([subQ11,subQ3]),TDD([makeQuery(id+"F2.opExtrude","CAP_VERTEX",VERTEX,{"disambiguationData":[OSD([subQ11,subQ3])],"isStart":false})])]})]}),makeQuery(id+"F4.opExtrude","SWEPT_EDGE",EDGE,{"disambiguationData":[OSD([subQ11,subQ1]),TDD([makeQuery(id+"F2.opExtrude","CAP_VERTEX",VERTEX,{"disambiguationData":[OSD([subQ11,subQ1])],"isStart":false})])]})]});var subQ13=sQuery(id+"F5.wireOp",EDGE,"E5");var subQ14=sQuery(id+"F5.wireOp",EDGE,"E3");var subQ15=sQuery(id+"F6.wireOp",EDGE,"E31");var subQ16=sQuery(id+"F5.wireOp",EDGE,"E8");var subQ17=makeQuery(id+"F3.opExtrude","SWEPT_FACE",FACE,{"disambiguationData":[OSD([subQ2,subQ3])]});var subQ18=sQuery(id+"F6.wireOp",EDGE,"E30");var subQ19=makeQuery(id+"F4.boolean.opBoolean","MERGE",EDGE,{"derivedFrom":[makeQuery(id+"F3.boolean.opBoolean","MERGE",EDGE,{"derivedFrom":[makeQuery(id+"F1.opExtrude","CAP_EDGE",EDGE,{"disambiguationData":[OSD([subQ11])],"isStart":false}),makeQuery(id+"F3.opExtrude","SWEPT_EDGE",EDGE,{"disambiguationData":[OSD([subQ11,subQ3]),TDD([makeQuery(id+"F1.opExtrude","CAP_VERTEX",VERTEX,{"disambiguationData":[OSD([subQ11,subQ3])],"isStart":false})])]})]}),makeQuery(id+"F4.opExtrude","SWEPT_EDGE",EDGE,{"disambiguationData":[OSD([subQ11,subQ1]),TDD([makeQuery(id+"F1.opExtrude","CAP_VERTEX",VERTEX,{"disambiguationData":[OSD([subQ11,subQ1])],"isStart":false})])]})]});var subQ20=makeQuery(id+"F1.opExtrude","SWEPT_FACE",FACE,{"disambiguationData":[OSD([subQ2])]});var subQ21=makeQuery(id+"F4.opExtrude","SWEPT_FACE",FACE,{"disambiguationData":[OSD([subQ2,subQ1])]});Q11=makeQuery(id+"F9.boolean.opBoolean","SPLIT",FACE,{"disambiguationData":[TD([makeQuery(id+"F1.opExtrude","CAP_FACE",FACE,{"disambiguationData":[OSD([subQ11,subQ2,subQ3,subQ1])],"isStart":false}),subQ20,subQ8,makeQuery(id+"F2.opExtrude","CAP_FACE",FACE,{"disambiguationData":[OSD([subQ11,subQ2,subQ3,subQ1])],"isStart":false}),makeQuery(id+"F3.opExtrude","SWEPT_FACE",FACE,{"disambiguationData":[OSD([subQ3]),TDD([makeQuery(id+"F1.opExtrude","CAP_EDGE",EDGE,{"disambiguationData":[OSD([subQ3])],"isStart":false})])]}),makeQuery(id+"F3.opExtrude","SWEPT_FACE",FACE,{"disambiguationData":[OSD([subQ3]),TDD([makeQuery(id+"F2.opExtrude","CAP_EDGE",EDGE,{"disambiguationData":[OSD([subQ3])],"isStart":false})])]}),subQ17,makeQuery(id+"F4.opExtrude","SWEPT_FACE",FACE,{"disambiguationData":[OSD([subQ1]),TDD([makeQuery(id+"F1.opExtrude","CAP_EDGE",EDGE,{"disambiguationData":[OSD([subQ1])],"isStart":false})])]}),makeQuery(id+"F4.opExtrude","SWEPT_FACE",FACE,{"disambiguationData":[OSD([subQ1]),TDD([makeQuery(id+"F2.opExtrude","CAP_EDGE",EDGE,{"disambiguationData":[OSD([subQ1])],"isStart":false})])]}),subQ21,makeQuery(id+"F4.opExtrude","CAP_FACE",FACE,{"disambiguationData":[OSD([subQ1])],"isStart":false}),makeQuery(id+"F7.opExtrude","SWEPT_FACE",FACE,{"disambiguationData":[OSD([subQ11,subQ3,subQ1]),TDD([makeQuery(id+"F5.imprint","IMPRINT",EDGE,{"disambiguationData":[TD([[makeQuery(id+"F5.imprint","INTERSECT",VERTEX,{"derivedFrom":[subQ19,subQ14,sQuery(id+"F5.wireOp",EDGE,"E4")]}),1.0]])],"derivedFrom":subQ19})])]}),makeQuery(id+"F7.opExtrude","SWEPT_FACE",FACE,{"disambiguationData":[OSD([subQ11,subQ3,subQ1]),TDD([makeQuery(id+"F5.imprint","IMPRINT",EDGE,{"disambiguationData":[TD([[makeQuery(id+"F5.imprint","INTERSECT",VERTEX,{"derivedFrom":[subQ19,subQ13,sQuery(id+"F5.wireOp",EDGE,"E6")]}),-1.0]])],"derivedFrom":subQ19})])]}),makeQuery(id+"F7.opExtrude","SWEPT_FACE",FACE,{"disambiguationData":[OSD([subQ11,subQ3,subQ1]),TDD([makeQuery(id+"F5.imprint","IMPRINT",EDGE,{"disambiguationData":[TD([[makeQuery(id+"F5.imprint","INTERSECT",VERTEX,{"derivedFrom":[subQ12,sQuery(id+"F5.wireOp",EDGE,"E1"),subQ13]}),1.0]])],"derivedFrom":subQ12})])]}),makeQuery(id+"F7.opExtrude","SWEPT_FACE",FACE,{"disambiguationData":[OSD([subQ11,subQ3,subQ1]),TDD([makeQuery(id+"F5.imprint","IMPRINT",EDGE,{"disambiguationData":[TD([[makeQuery(id+"F5.imprint","INTERSECT",VERTEX,{"derivedFrom":[subQ12,subQ16,sQuery(id+"F5.wireOp",EDGE,"E9")]}),-1.0]])],"derivedFrom":subQ12})])]}),makeQuery(id+"F7.opExtrude","SWEPT_FACE",FACE,{"disambiguationData":[OSD([subQ11,subQ3,subQ1]),TDD([makeQuery(id+"F5.imprint","IMPRINT",EDGE,{"disambiguationData":[TD([[makeQuery(id+"F5.imprint","INTERSECT",VERTEX,{"derivedFrom":[subQ12,subQ10,sQuery(id+"F5.wireOp",EDGE,"E14")]}),1.0]])],"derivedFrom":subQ12})])]}),makeQuery(id+"F9.opExtrude","SWEPT_FACE",FACE,{"disambiguationData":[OSD([subQ18])]}),makeQuery(id+"F9.opExtrude","SWEPT_FACE",FACE,{"disambiguationData":[OSD([subQ15])]}),makeQuery(id+"F9.opExtrude","SWEPT_FACE",FACE,{"disambiguationData":[OSD([subQ2,subQ3,subQ1]),TDD([makeQuery(id+"F6.imprint","IMPRINT",EDGE,{"disambiguationData":[TD([[makeQuery(id+"F6.imprint","INTERSECT",VERTEX,{"derivedFrom":[subQ6,subQ0,sQuery(id+"F6.wireOp",EDGE,"E19")]}),1.0]])],"derivedFrom":subQ6})])]}),makeQuery(id+"F9.opExtrude","SWEPT_FACE",FACE,{"disambiguationData":[OSD([subQ2,subQ3,subQ1]),TDD([makeQuery(id+"F6.imprint","IMPRINT",EDGE,{"disambiguationData":[TD([[makeQuery(id+"F6.imprint","INTERSECT",VERTEX,{"derivedFrom":[subQ6,subQ5,sQuery(id+"F6.wireOp",EDGE,"E27")]}),-1.0]])],"derivedFrom":subQ6})])]}),makeQuery(id+"F9.opExtrude","SWEPT_FACE",FACE,{"disambiguationData":[OSD([subQ2,subQ3,subQ1]),TDD([makeQuery(id+"F6.imprint","IMPRINT",EDGE,{"disambiguationData":[TD([[makeQuery(id+"F6.imprint","INTERSECT",VERTEX,{"derivedFrom":[subQ4,sQuery(id+"F6.wireOp",EDGE,"E17"),subQ0]}),-1.0]])],"derivedFrom":subQ4})])]}),makeQuery(id+"F9.opExtrude","SWEPT_FACE",FACE,{"disambiguationData":[OSD([subQ2,subQ3,subQ1]),TDD([makeQuery(id+"F6.imprint","IMPRINT",EDGE,{"disambiguationData":[TD([[makeQuery(id+"F6.imprint","INTERSECT",VERTEX,{"derivedFrom":[subQ4,subQ9,sQuery(id+"F6.wireOp",EDGE,"E22")]}),1.0]])],"derivedFrom":subQ4})])]}),makeQuery(id+"F9.opExtrude","SWEPT_FACE",FACE,{"disambiguationData":[OSD([subQ2,subQ3,subQ1]),TDD([makeQuery(id+"F6.imprint","IMPRINT",EDGE,{"disambiguationData":[TD([[makeQuery(id+"F6.imprint","INTERSECT",VERTEX,{"derivedFrom":[subQ4,subQ7,subQ18]}),-1.0]])],"derivedFrom":subQ4})])]})])],"derivedFrom":makeQuery(id+"F4.boolean.opBoolean","MERGE",FACE,{"derivedFrom":[makeQuery(id+"F3.boolean.opBoolean","MERGE",FACE,{"derivedFrom":[makeQuery(id+"F2.boolean.opBoolean","MERGE",FACE,{"derivedFrom":[subQ20,subQ8]}),subQ17]}),subQ21]})});}
            extrude(context, id + "F11", {"entities" : qUnion([Q0, Q1, Q2, Q3, Q4, Q5, Q6, Q7, Q8, Q9, Q10, Q11]), "operationType" : NewBodyOperationType.REMOVE, "oppositeDirection" : true, "depth" : 6.35 * mm, "offsetDistance" : 25.4 * mm});
        }
        {
            var Q0;
            {var subQ0=sQuery(id+"F6.wireOp",EDGE,"E18");var subQ1=sQuery(id+"F0.wireOp",EDGE,"E0.right");var subQ2=sQuery(id+"F0.wireOp",EDGE,"E0.top");var subQ3=sQuery(id+"F0.wireOp",EDGE,"E0.left");var subQ4=makeQuery(id+"F4.boolean.opBoolean","MERGE",EDGE,{"derivedFrom":[makeQuery(id+"F3.boolean.opBoolean","MERGE",EDGE,{"derivedFrom":[makeQuery(id+"F2.opExtrude","CAP_EDGE",EDGE,{"disambiguationData":[OSD([subQ2])],"isStart":false}),makeQuery(id+"F3.opExtrude","SWEPT_EDGE",EDGE,{"disambiguationData":[OSD([subQ2,subQ3]),TDD([makeQuery(id+"F2.opExtrude","CAP_VERTEX",VERTEX,{"disambiguationData":[OSD([subQ2,subQ3])],"isStart":false})])]})]}),makeQuery(id+"F4.opExtrude","SWEPT_EDGE",EDGE,{"disambiguationData":[OSD([subQ2,subQ1]),TDD([makeQuery(id+"F2.opExtrude","CAP_VERTEX",VERTEX,{"disambiguationData":[OSD([subQ2,subQ1])],"isStart":false})])]})]});var subQ5=sQuery(id+"F6.wireOp",EDGE,"E26");var subQ6=sQuery(id+"F6.wireOp",EDGE,"E23");var subQ7=makeQuery(id+"F3.opExtrude","SWEPT_FACE",FACE,{"disambiguationData":[OSD([subQ2,subQ3])]});var subQ8=sQuery(id+"F6.wireOp",EDGE,"E22");var subQ9=makeQuery(id+"F4.boolean.opBoolean","MERGE",EDGE,{"derivedFrom":[makeQuery(id+"F3.boolean.opBoolean","MERGE",EDGE,{"derivedFrom":[makeQuery(id+"F1.opExtrude","CAP_EDGE",EDGE,{"disambiguationData":[OSD([subQ2])],"isStart":false}),makeQuery(id+"F3.opExtrude","SWEPT_EDGE",EDGE,{"disambiguationData":[OSD([subQ2,subQ3]),TDD([makeQuery(id+"F1.opExtrude","CAP_VERTEX",VERTEX,{"disambiguationData":[OSD([subQ2,subQ3])],"isStart":false})])]})]}),makeQuery(id+"F4.opExtrude","SWEPT_EDGE",EDGE,{"disambiguationData":[OSD([subQ2,subQ1]),TDD([makeQuery(id+"F1.opExtrude","CAP_VERTEX",VERTEX,{"disambiguationData":[OSD([subQ2,subQ1])],"isStart":false})])]})]});var subQ10=sQuery(id+"F6.wireOp",EDGE,"E21");var subQ11=sQuery(id+"F5.wireOp",EDGE,"E13");var subQ12=sQuery(id+"F0.wireOp",EDGE,"E0.bottom");var subQ13=makeQuery(id+"F4.boolean.opBoolean","MERGE",EDGE,{"derivedFrom":[makeQuery(id+"F3.boolean.opBoolean","MERGE",EDGE,{"derivedFrom":[makeQuery(id+"F2.opExtrude","CAP_EDGE",EDGE,{"disambiguationData":[OSD([subQ12])],"isStart":false}),makeQuery(id+"F3.opExtrude","SWEPT_EDGE",EDGE,{"disambiguationData":[OSD([subQ12,subQ3]),TDD([makeQuery(id+"F2.opExtrude","CAP_VERTEX",VERTEX,{"disambiguationData":[OSD([subQ12,subQ3])],"isStart":false})])]})]}),makeQuery(id+"F4.opExtrude","SWEPT_EDGE",EDGE,{"disambiguationData":[OSD([subQ12,subQ1]),TDD([makeQuery(id+"F2.opExtrude","CAP_VERTEX",VERTEX,{"disambiguationData":[OSD([subQ12,subQ1])],"isStart":false})])]})]});var subQ14=sQuery(id+"F5.wireOp",EDGE,"E5");var subQ15=sQuery(id+"F5.wireOp",EDGE,"E3");var subQ16=makeQuery(id+"F4.opExtrude","SWEPT_FACE",FACE,{"disambiguationData":[OSD([subQ2,subQ1])]});var subQ17=makeQuery(id+"F2.opExtrude","SWEPT_FACE",FACE,{"disambiguationData":[OSD([subQ2])]});var subQ18=sQuery(id+"F6.wireOp",EDGE,"E29");var subQ19=sQuery(id+"F5.wireOp",EDGE,"E8");var subQ20=makeQuery(id+"F4.boolean.opBoolean","MERGE",EDGE,{"derivedFrom":[makeQuery(id+"F3.boolean.opBoolean","MERGE",EDGE,{"derivedFrom":[makeQuery(id+"F1.opExtrude","CAP_EDGE",EDGE,{"disambiguationData":[OSD([subQ12])],"isStart":false}),makeQuery(id+"F3.opExtrude","SWEPT_EDGE",EDGE,{"disambiguationData":[OSD([subQ12,subQ3]),TDD([makeQuery(id+"F1.opExtrude","CAP_VERTEX",VERTEX,{"disambiguationData":[OSD([subQ12,subQ3])],"isStart":false})])]})]}),makeQuery(id+"F4.opExtrude","SWEPT_EDGE",EDGE,{"disambiguationData":[OSD([subQ12,subQ1]),TDD([makeQuery(id+"F1.opExtrude","CAP_VERTEX",VERTEX,{"disambiguationData":[OSD([subQ12,subQ1])],"isStart":false})])]})]});var subQ21=makeQuery(id+"F1.opExtrude","SWEPT_FACE",FACE,{"disambiguationData":[OSD([subQ2])]});Q0=makeQuery(id+"F9.boolean.opBoolean","SPLIT",FACE,{"disambiguationData":[TD([makeQuery(id+"F1.opExtrude","CAP_FACE",FACE,{"disambiguationData":[OSD([subQ12,subQ2,subQ3,subQ1])],"isStart":false}),subQ21,subQ17,makeQuery(id+"F2.opExtrude","CAP_FACE",FACE,{"disambiguationData":[OSD([subQ12,subQ2,subQ3,subQ1])],"isStart":false}),makeQuery(id+"F3.opExtrude","SWEPT_FACE",FACE,{"disambiguationData":[OSD([subQ3]),TDD([makeQuery(id+"F1.opExtrude","CAP_EDGE",EDGE,{"disambiguationData":[OSD([subQ3])],"isStart":false})])]}),makeQuery(id+"F3.opExtrude","SWEPT_FACE",FACE,{"disambiguationData":[OSD([subQ3]),TDD([makeQuery(id+"F2.opExtrude","CAP_EDGE",EDGE,{"disambiguationData":[OSD([subQ3])],"isStart":false})])]}),subQ7,makeQuery(id+"F3.opExtrude","CAP_FACE",FACE,{"disambiguationData":[OSD([subQ3])],"isStart":false}),makeQuery(id+"F4.opExtrude","SWEPT_FACE",FACE,{"disambiguationData":[OSD([subQ1]),TDD([makeQuery(id+"F1.opExtrude","CAP_EDGE",EDGE,{"disambiguationData":[OSD([subQ1])],"isStart":false})])]}),makeQuery(id+"F4.opExtrude","SWEPT_FACE",FACE,{"disambiguationData":[OSD([subQ1]),TDD([makeQuery(id+"F2.opExtrude","CAP_EDGE",EDGE,{"disambiguationData":[OSD([subQ1])],"isStart":false})])]}),subQ16,makeQuery(id+"F7.opExtrude","SWEPT_FACE",FACE,{"disambiguationData":[OSD([subQ12,subQ3,subQ1]),TDD([makeQuery(id+"F5.imprint","IMPRINT",EDGE,{"disambiguationData":[TD([[makeQuery(id+"F5.imprint","INTERSECT",VERTEX,{"derivedFrom":[subQ20,subQ15,sQuery(id+"F5.wireOp",EDGE,"E4")]}),1.0]])],"derivedFrom":subQ20})])]}),makeQuery(id+"F7.opExtrude","SWEPT_FACE",FACE,{"disambiguationData":[OSD([subQ12,subQ3,subQ1]),TDD([makeQuery(id+"F5.imprint","IMPRINT",EDGE,{"disambiguationData":[TD([[makeQuery(id+"F5.imprint","INTERSECT",VERTEX,{"derivedFrom":[subQ20,subQ14,sQuery(id+"F5.wireOp",EDGE,"E6")]}),-1.0]])],"derivedFrom":subQ20})])]}),makeQuery(id+"F7.opExtrude","SWEPT_FACE",FACE,{"disambiguationData":[OSD([subQ12,subQ3,subQ1]),TDD([makeQuery(id+"F5.imprint","IMPRINT",EDGE,{"disambiguationData":[TD([[makeQuery(id+"F5.imprint","INTERSECT",VERTEX,{"derivedFrom":[subQ13,sQuery(id+"F5.wireOp",EDGE,"E1"),subQ14]}),1.0]])],"derivedFrom":subQ13})])]}),makeQuery(id+"F7.opExtrude","SWEPT_FACE",FACE,{"disambiguationData":[OSD([subQ12,subQ3,subQ1]),TDD([makeQuery(id+"F5.imprint","IMPRINT",EDGE,{"disambiguationData":[TD([[makeQuery(id+"F5.imprint","INTERSECT",VERTEX,{"derivedFrom":[subQ13,subQ19,sQuery(id+"F5.wireOp",EDGE,"E9")]}),-1.0]])],"derivedFrom":subQ13})])]}),makeQuery(id+"F7.opExtrude","SWEPT_FACE",FACE,{"disambiguationData":[OSD([subQ12,subQ3,subQ1]),TDD([makeQuery(id+"F5.imprint","IMPRINT",EDGE,{"disambiguationData":[TD([[makeQuery(id+"F5.imprint","INTERSECT",VERTEX,{"derivedFrom":[subQ13,subQ11,sQuery(id+"F5.wireOp",EDGE,"E14")]}),1.0]])],"derivedFrom":subQ13})])]}),makeQuery(id+"F9.opExtrude","SWEPT_FACE",FACE,{"disambiguationData":[OSD([subQ8])]}),makeQuery(id+"F9.opExtrude","SWEPT_FACE",FACE,{"disambiguationData":[OSD([subQ6])]}),makeQuery(id+"F9.opExtrude","SWEPT_FACE",FACE,{"disambiguationData":[OSD([subQ2,subQ3,subQ1]),TDD([makeQuery(id+"F6.imprint","IMPRINT",EDGE,{"disambiguationData":[TD([[makeQuery(id+"F6.imprint","INTERSECT",VERTEX,{"derivedFrom":[subQ9,subQ0,sQuery(id+"F6.wireOp",EDGE,"E19")]}),1.0]])],"derivedFrom":subQ9})])]}),makeQuery(id+"F9.opExtrude","SWEPT_FACE",FACE,{"disambiguationData":[OSD([subQ2,subQ3,subQ1]),TDD([makeQuery(id+"F6.imprint","IMPRINT",EDGE,{"disambiguationData":[TD([[makeQuery(id+"F6.imprint","INTERSECT",VERTEX,{"derivedFrom":[subQ9,subQ5,sQuery(id+"F6.wireOp",EDGE,"E27")]}),-1.0]])],"derivedFrom":subQ9})])]}),makeQuery(id+"F9.opExtrude","SWEPT_FACE",FACE,{"disambiguationData":[OSD([subQ2,subQ3,subQ1]),TDD([makeQuery(id+"F6.imprint","IMPRINT",EDGE,{"disambiguationData":[TD([[makeQuery(id+"F6.imprint","INTERSECT",VERTEX,{"derivedFrom":[subQ4,sQuery(id+"F6.wireOp",EDGE,"E17"),subQ0]}),-1.0]])],"derivedFrom":subQ4})])]}),makeQuery(id+"F9.opExtrude","SWEPT_FACE",FACE,{"disambiguationData":[OSD([subQ2,subQ3,subQ1]),TDD([makeQuery(id+"F6.imprint","IMPRINT",EDGE,{"disambiguationData":[TD([[makeQuery(id+"F6.imprint","INTERSECT",VERTEX,{"derivedFrom":[subQ4,subQ10,subQ8]}),1.0]])],"derivedFrom":subQ4})])]}),makeQuery(id+"F9.opExtrude","SWEPT_FACE",FACE,{"disambiguationData":[OSD([subQ2,subQ3,subQ1]),TDD([makeQuery(id+"F6.imprint","IMPRINT",EDGE,{"disambiguationData":[TD([[makeQuery(id+"F6.imprint","INTERSECT",VERTEX,{"derivedFrom":[subQ4,subQ18,sQuery(id+"F6.wireOp",EDGE,"E30")]}),-1.0]])],"derivedFrom":subQ4})])]})])],"derivedFrom":makeQuery(id+"F4.boolean.opBoolean","MERGE",FACE,{"derivedFrom":[makeQuery(id+"F3.boolean.opBoolean","MERGE",FACE,{"derivedFrom":[makeQuery(id+"F2.boolean.opBoolean","MERGE",FACE,{"derivedFrom":[subQ21,subQ17]}),subQ7]}),subQ16]})});}
            var Q1;
            {var subQ0=sQuery(id+"F6.wireOp",EDGE,"E18");var subQ1=sQuery(id+"F0.wireOp",EDGE,"E0.right");var subQ2=sQuery(id+"F0.wireOp",EDGE,"E0.top");var subQ3=sQuery(id+"F0.wireOp",EDGE,"E0.left");var subQ4=makeQuery(id+"F4.boolean.opBoolean","MERGE",EDGE,{"derivedFrom":[makeQuery(id+"F3.boolean.opBoolean","MERGE",EDGE,{"derivedFrom":[makeQuery(id+"F2.opExtrude","CAP_EDGE",EDGE,{"disambiguationData":[OSD([subQ2])],"isStart":false}),makeQuery(id+"F3.opExtrude","SWEPT_EDGE",EDGE,{"disambiguationData":[OSD([subQ2,subQ3]),TDD([makeQuery(id+"F2.opExtrude","CAP_VERTEX",VERTEX,{"disambiguationData":[OSD([subQ2,subQ3])],"isStart":false})])]})]}),makeQuery(id+"F4.opExtrude","SWEPT_EDGE",EDGE,{"disambiguationData":[OSD([subQ2,subQ1]),TDD([makeQuery(id+"F2.opExtrude","CAP_VERTEX",VERTEX,{"disambiguationData":[OSD([subQ2,subQ1])],"isStart":false})])]})]});var subQ5=sQuery(id+"F6.wireOp",EDGE,"E26");var subQ6=makeQuery(id+"F4.boolean.opBoolean","MERGE",EDGE,{"derivedFrom":[makeQuery(id+"F3.boolean.opBoolean","MERGE",EDGE,{"derivedFrom":[makeQuery(id+"F1.opExtrude","CAP_EDGE",EDGE,{"disambiguationData":[OSD([subQ2])],"isStart":false}),makeQuery(id+"F3.opExtrude","SWEPT_EDGE",EDGE,{"disambiguationData":[OSD([subQ2,subQ3]),TDD([makeQuery(id+"F1.opExtrude","CAP_VERTEX",VERTEX,{"disambiguationData":[OSD([subQ2,subQ3])],"isStart":false})])]})]}),makeQuery(id+"F4.opExtrude","SWEPT_EDGE",EDGE,{"disambiguationData":[OSD([subQ2,subQ1]),TDD([makeQuery(id+"F1.opExtrude","CAP_VERTEX",VERTEX,{"disambiguationData":[OSD([subQ2,subQ1])],"isStart":false})])]})]});var subQ7=sQuery(id+"F6.wireOp",EDGE,"E29");var subQ8=makeQuery(id+"F2.opExtrude","SWEPT_FACE",FACE,{"disambiguationData":[OSD([subQ2])]});var subQ9=sQuery(id+"F6.wireOp",EDGE,"E23");var subQ10=makeQuery(id+"F3.opExtrude","SWEPT_FACE",FACE,{"disambiguationData":[OSD([subQ2,subQ3])]});var subQ11=sQuery(id+"F6.wireOp",EDGE,"E22");var subQ12=sQuery(id+"F6.wireOp",EDGE,"E20");var subQ13=sQuery(id+"F6.wireOp",EDGE,"E19");var subQ14=sQuery(id+"F6.wireOp",EDGE,"E21");var subQ15=sQuery(id+"F5.wireOp",EDGE,"E13");var subQ16=sQuery(id+"F0.wireOp",EDGE,"E0.bottom");var subQ17=makeQuery(id+"F4.boolean.opBoolean","MERGE",EDGE,{"derivedFrom":[makeQuery(id+"F3.boolean.opBoolean","MERGE",EDGE,{"derivedFrom":[makeQuery(id+"F2.opExtrude","CAP_EDGE",EDGE,{"disambiguationData":[OSD([subQ16])],"isStart":false}),makeQuery(id+"F3.opExtrude","SWEPT_EDGE",EDGE,{"disambiguationData":[OSD([subQ16,subQ3]),TDD([makeQuery(id+"F2.opExtrude","CAP_VERTEX",VERTEX,{"disambiguationData":[OSD([subQ16,subQ3])],"isStart":false})])]})]}),makeQuery(id+"F4.opExtrude","SWEPT_EDGE",EDGE,{"disambiguationData":[OSD([subQ16,subQ1]),TDD([makeQuery(id+"F2.opExtrude","CAP_VERTEX",VERTEX,{"disambiguationData":[OSD([subQ16,subQ1])],"isStart":false})])]})]});var subQ18=sQuery(id+"F5.wireOp",EDGE,"E5");var subQ19=sQuery(id+"F5.wireOp",EDGE,"E3");var subQ20=sQuery(id+"F5.wireOp",EDGE,"E8");var subQ21=makeQuery(id+"F4.boolean.opBoolean","MERGE",EDGE,{"derivedFrom":[makeQuery(id+"F3.boolean.opBoolean","MERGE",EDGE,{"derivedFrom":[makeQuery(id+"F1.opExtrude","CAP_EDGE",EDGE,{"disambiguationData":[OSD([subQ16])],"isStart":false}),makeQuery(id+"F3.opExtrude","SWEPT_EDGE",EDGE,{"disambiguationData":[OSD([subQ16,subQ3]),TDD([makeQuery(id+"F1.opExtrude","CAP_VERTEX",VERTEX,{"disambiguationData":[OSD([subQ16,subQ3])],"isStart":false})])]})]}),makeQuery(id+"F4.opExtrude","SWEPT_EDGE",EDGE,{"disambiguationData":[OSD([subQ16,subQ1]),TDD([makeQuery(id+"F1.opExtrude","CAP_VERTEX",VERTEX,{"disambiguationData":[OSD([subQ16,subQ1])],"isStart":false})])]})]});var subQ22=makeQuery(id+"F1.opExtrude","SWEPT_FACE",FACE,{"disambiguationData":[OSD([subQ2])]});var subQ23=makeQuery(id+"F4.opExtrude","SWEPT_FACE",FACE,{"disambiguationData":[OSD([subQ2,subQ1])]});Q1=makeQuery(id+"F9.boolean.opBoolean","SPLIT",FACE,{"disambiguationData":[TD([makeQuery(id+"F1.opExtrude","CAP_FACE",FACE,{"disambiguationData":[OSD([subQ16,subQ2,subQ3,subQ1])],"isStart":false}),subQ22,subQ8,makeQuery(id+"F2.opExtrude","CAP_FACE",FACE,{"disambiguationData":[OSD([subQ16,subQ2,subQ3,subQ1])],"isStart":false}),makeQuery(id+"F3.opExtrude","SWEPT_FACE",FACE,{"disambiguationData":[OSD([subQ3]),TDD([makeQuery(id+"F1.opExtrude","CAP_EDGE",EDGE,{"disambiguationData":[OSD([subQ3])],"isStart":false})])]}),makeQuery(id+"F3.opExtrude","SWEPT_FACE",FACE,{"disambiguationData":[OSD([subQ3]),TDD([makeQuery(id+"F2.opExtrude","CAP_EDGE",EDGE,{"disambiguationData":[OSD([subQ3])],"isStart":false})])]}),subQ10,makeQuery(id+"F4.opExtrude","SWEPT_FACE",FACE,{"disambiguationData":[OSD([subQ1]),TDD([makeQuery(id+"F1.opExtrude","CAP_EDGE",EDGE,{"disambiguationData":[OSD([subQ1])],"isStart":false})])]}),makeQuery(id+"F4.opExtrude","SWEPT_FACE",FACE,{"disambiguationData":[OSD([subQ1]),TDD([makeQuery(id+"F2.opExtrude","CAP_EDGE",EDGE,{"disambiguationData":[OSD([subQ1])],"isStart":false})])]}),subQ23,makeQuery(id+"F7.opExtrude","SWEPT_FACE",FACE,{"disambiguationData":[OSD([subQ16,subQ3,subQ1]),TDD([makeQuery(id+"F5.imprint","IMPRINT",EDGE,{"disambiguationData":[TD([[makeQuery(id+"F5.imprint","INTERSECT",VERTEX,{"derivedFrom":[subQ21,subQ19,sQuery(id+"F5.wireOp",EDGE,"E4")]}),1.0]])],"derivedFrom":subQ21})])]}),makeQuery(id+"F7.opExtrude","SWEPT_FACE",FACE,{"disambiguationData":[OSD([subQ16,subQ3,subQ1]),TDD([makeQuery(id+"F5.imprint","IMPRINT",EDGE,{"disambiguationData":[TD([[makeQuery(id+"F5.imprint","INTERSECT",VERTEX,{"derivedFrom":[subQ21,subQ18,sQuery(id+"F5.wireOp",EDGE,"E6")]}),-1.0]])],"derivedFrom":subQ21})])]}),makeQuery(id+"F7.opExtrude","SWEPT_FACE",FACE,{"disambiguationData":[OSD([subQ16,subQ3,subQ1]),TDD([makeQuery(id+"F5.imprint","IMPRINT",EDGE,{"disambiguationData":[TD([[makeQuery(id+"F5.imprint","INTERSECT",VERTEX,{"derivedFrom":[subQ17,sQuery(id+"F5.wireOp",EDGE,"E1"),subQ18]}),1.0]])],"derivedFrom":subQ17})])]}),makeQuery(id+"F7.opExtrude","SWEPT_FACE",FACE,{"disambiguationData":[OSD([subQ16,subQ3,subQ1]),TDD([makeQuery(id+"F5.imprint","IMPRINT",EDGE,{"disambiguationData":[TD([[makeQuery(id+"F5.imprint","INTERSECT",VERTEX,{"derivedFrom":[subQ17,subQ20,sQuery(id+"F5.wireOp",EDGE,"E9")]}),-1.0]])],"derivedFrom":subQ17})])]}),makeQuery(id+"F7.opExtrude","SWEPT_FACE",FACE,{"disambiguationData":[OSD([subQ16,subQ3,subQ1]),TDD([makeQuery(id+"F5.imprint","IMPRINT",EDGE,{"disambiguationData":[TD([[makeQuery(id+"F5.imprint","INTERSECT",VERTEX,{"derivedFrom":[subQ17,subQ15,sQuery(id+"F5.wireOp",EDGE,"E14")]}),1.0]])],"derivedFrom":subQ17})])]}),makeQuery(id+"F9.opExtrude","SWEPT_FACE",FACE,{"disambiguationData":[OSD([subQ13])]}),makeQuery(id+"F9.opExtrude","SWEPT_FACE",FACE,{"disambiguationData":[OSD([subQ12])]}),makeQuery(id+"F9.opExtrude","SWEPT_FACE",FACE,{"disambiguationData":[OSD([subQ11])]}),makeQuery(id+"F9.opExtrude","SWEPT_FACE",FACE,{"disambiguationData":[OSD([subQ9])]}),makeQuery(id+"F9.opExtrude","SWEPT_FACE",FACE,{"disambiguationData":[OSD([subQ2,subQ3,subQ1]),TDD([makeQuery(id+"F6.imprint","IMPRINT",EDGE,{"disambiguationData":[TD([[makeQuery(id+"F6.imprint","INTERSECT",VERTEX,{"derivedFrom":[subQ6,subQ0,subQ13]}),1.0]])],"derivedFrom":subQ6})])]}),makeQuery(id+"F9.opExtrude","SWEPT_FACE",FACE,{"disambiguationData":[OSD([subQ2,subQ3,subQ1]),TDD([makeQuery(id+"F6.imprint","IMPRINT",EDGE,{"disambiguationData":[TD([[makeQuery(id+"F6.imprint","INTERSECT",VERTEX,{"derivedFrom":[subQ6,subQ5,sQuery(id+"F6.wireOp",EDGE,"E27")]}),-1.0]])],"derivedFrom":subQ6})])]}),makeQuery(id+"F9.opExtrude","SWEPT_FACE",FACE,{"disambiguationData":[OSD([subQ2,subQ3,subQ1]),TDD([makeQuery(id+"F6.imprint","IMPRINT",EDGE,{"disambiguationData":[TD([[makeQuery(id+"F6.imprint","INTERSECT",VERTEX,{"derivedFrom":[subQ4,sQuery(id+"F6.wireOp",EDGE,"E17"),subQ0]}),-1.0]])],"derivedFrom":subQ4})])]}),makeQuery(id+"F9.opExtrude","SWEPT_FACE",FACE,{"disambiguationData":[OSD([subQ2,subQ3,subQ1]),TDD([makeQuery(id+"F6.imprint","IMPRINT",EDGE,{"disambiguationData":[TD([[makeQuery(id+"F6.imprint","INTERSECT",VERTEX,{"derivedFrom":[subQ4,subQ14,subQ11]}),1.0]])],"derivedFrom":subQ4})])]}),makeQuery(id+"F9.opExtrude","SWEPT_FACE",FACE,{"disambiguationData":[OSD([subQ2,subQ3,subQ1]),TDD([makeQuery(id+"F6.imprint","IMPRINT",EDGE,{"disambiguationData":[TD([[makeQuery(id+"F6.imprint","INTERSECT",VERTEX,{"derivedFrom":[subQ4,subQ7,sQuery(id+"F6.wireOp",EDGE,"E30")]}),-1.0]])],"derivedFrom":subQ4})])]})])],"derivedFrom":makeQuery(id+"F4.boolean.opBoolean","MERGE",FACE,{"derivedFrom":[makeQuery(id+"F3.boolean.opBoolean","MERGE",FACE,{"derivedFrom":[makeQuery(id+"F2.boolean.opBoolean","MERGE",FACE,{"derivedFrom":[subQ22,subQ8]}),subQ10]}),subQ23]})});}
            var Q2;
            {var subQ0=sQuery(id+"F6.wireOp",EDGE,"E18");var subQ1=sQuery(id+"F6.wireOp",EDGE,"E17");var subQ2=sQuery(id+"F0.wireOp",EDGE,"E0.right");var subQ3=sQuery(id+"F0.wireOp",EDGE,"E0.top");var subQ4=sQuery(id+"F0.wireOp",EDGE,"E0.left");var subQ5=makeQuery(id+"F4.boolean.opBoolean","MERGE",EDGE,{"derivedFrom":[makeQuery(id+"F3.boolean.opBoolean","MERGE",EDGE,{"derivedFrom":[makeQuery(id+"F2.opExtrude","CAP_EDGE",EDGE,{"disambiguationData":[OSD([subQ3])],"isStart":false}),makeQuery(id+"F3.opExtrude","SWEPT_EDGE",EDGE,{"disambiguationData":[OSD([subQ3,subQ4]),TDD([makeQuery(id+"F2.opExtrude","CAP_VERTEX",VERTEX,{"disambiguationData":[OSD([subQ3,subQ4])],"isStart":false})])]})]}),makeQuery(id+"F4.opExtrude","SWEPT_EDGE",EDGE,{"disambiguationData":[OSD([subQ3,subQ2]),TDD([makeQuery(id+"F2.opExtrude","CAP_VERTEX",VERTEX,{"disambiguationData":[OSD([subQ3,subQ2])],"isStart":false})])]})]});var subQ6=sQuery(id+"F6.wireOp",EDGE,"E26");var subQ7=sQuery(id+"F6.wireOp",EDGE,"E25");var subQ8=makeQuery(id+"F4.boolean.opBoolean","MERGE",EDGE,{"derivedFrom":[makeQuery(id+"F3.boolean.opBoolean","MERGE",EDGE,{"derivedFrom":[makeQuery(id+"F1.opExtrude","CAP_EDGE",EDGE,{"disambiguationData":[OSD([subQ3])],"isStart":false}),makeQuery(id+"F3.opExtrude","SWEPT_EDGE",EDGE,{"disambiguationData":[OSD([subQ3,subQ4]),TDD([makeQuery(id+"F1.opExtrude","CAP_VERTEX",VERTEX,{"disambiguationData":[OSD([subQ3,subQ4])],"isStart":false})])]})]}),makeQuery(id+"F4.opExtrude","SWEPT_EDGE",EDGE,{"disambiguationData":[OSD([subQ3,subQ2]),TDD([makeQuery(id+"F1.opExtrude","CAP_VERTEX",VERTEX,{"disambiguationData":[OSD([subQ3,subQ2])],"isStart":false})])]})]});var subQ9=sQuery(id+"F6.wireOp",EDGE,"E29");var subQ10=makeQuery(id+"F2.opExtrude","SWEPT_FACE",FACE,{"disambiguationData":[OSD([subQ3])]});var subQ11=sQuery(id+"F6.wireOp",EDGE,"E20");var subQ12=sQuery(id+"F6.wireOp",EDGE,"E19");var subQ13=sQuery(id+"F6.wireOp",EDGE,"E21");var subQ14=sQuery(id+"F5.wireOp",EDGE,"E13");var subQ15=sQuery(id+"F0.wireOp",EDGE,"E0.bottom");var subQ16=makeQuery(id+"F4.boolean.opBoolean","MERGE",EDGE,{"derivedFrom":[makeQuery(id+"F3.boolean.opBoolean","MERGE",EDGE,{"derivedFrom":[makeQuery(id+"F2.opExtrude","CAP_EDGE",EDGE,{"disambiguationData":[OSD([subQ15])],"isStart":false}),makeQuery(id+"F3.opExtrude","SWEPT_EDGE",EDGE,{"disambiguationData":[OSD([subQ15,subQ4]),TDD([makeQuery(id+"F2.opExtrude","CAP_VERTEX",VERTEX,{"disambiguationData":[OSD([subQ15,subQ4])],"isStart":false})])]})]}),makeQuery(id+"F4.opExtrude","SWEPT_EDGE",EDGE,{"disambiguationData":[OSD([subQ15,subQ2]),TDD([makeQuery(id+"F2.opExtrude","CAP_VERTEX",VERTEX,{"disambiguationData":[OSD([subQ15,subQ2])],"isStart":false})])]})]});var subQ17=sQuery(id+"F5.wireOp",EDGE,"E5");var subQ18=sQuery(id+"F5.wireOp",EDGE,"E3");var subQ19=sQuery(id+"F5.wireOp",EDGE,"E8");var subQ20=makeQuery(id+"F3.opExtrude","SWEPT_FACE",FACE,{"disambiguationData":[OSD([subQ3,subQ4])]});var subQ21=makeQuery(id+"F4.boolean.opBoolean","MERGE",EDGE,{"derivedFrom":[makeQuery(id+"F3.boolean.opBoolean","MERGE",EDGE,{"derivedFrom":[makeQuery(id+"F1.opExtrude","CAP_EDGE",EDGE,{"disambiguationData":[OSD([subQ15])],"isStart":false}),makeQuery(id+"F3.opExtrude","SWEPT_EDGE",EDGE,{"disambiguationData":[OSD([subQ15,subQ4]),TDD([makeQuery(id+"F1.opExtrude","CAP_VERTEX",VERTEX,{"disambiguationData":[OSD([subQ15,subQ4])],"isStart":false})])]})]}),makeQuery(id+"F4.opExtrude","SWEPT_EDGE",EDGE,{"disambiguationData":[OSD([subQ15,subQ2]),TDD([makeQuery(id+"F1.opExtrude","CAP_VERTEX",VERTEX,{"disambiguationData":[OSD([subQ15,subQ2])],"isStart":false})])]})]});var subQ22=makeQuery(id+"F1.opExtrude","SWEPT_FACE",FACE,{"disambiguationData":[OSD([subQ3])]});var subQ23=makeQuery(id+"F4.opExtrude","SWEPT_FACE",FACE,{"disambiguationData":[OSD([subQ3,subQ2])]});Q2=makeQuery(id+"F9.boolean.opBoolean","SPLIT",FACE,{"disambiguationData":[TD([makeQuery(id+"F1.opExtrude","CAP_FACE",FACE,{"disambiguationData":[OSD([subQ15,subQ3,subQ4,subQ2])],"isStart":false}),subQ22,subQ10,makeQuery(id+"F2.opExtrude","CAP_FACE",FACE,{"disambiguationData":[OSD([subQ15,subQ3,subQ4,subQ2])],"isStart":false}),makeQuery(id+"F3.opExtrude","SWEPT_FACE",FACE,{"disambiguationData":[OSD([subQ4]),TDD([makeQuery(id+"F1.opExtrude","CAP_EDGE",EDGE,{"disambiguationData":[OSD([subQ4])],"isStart":false})])]}),makeQuery(id+"F3.opExtrude","SWEPT_FACE",FACE,{"disambiguationData":[OSD([subQ4]),TDD([makeQuery(id+"F2.opExtrude","CAP_EDGE",EDGE,{"disambiguationData":[OSD([subQ4])],"isStart":false})])]}),subQ20,makeQuery(id+"F4.opExtrude","SWEPT_FACE",FACE,{"disambiguationData":[OSD([subQ2]),TDD([makeQuery(id+"F1.opExtrude","CAP_EDGE",EDGE,{"disambiguationData":[OSD([subQ2])],"isStart":false})])]}),makeQuery(id+"F4.opExtrude","SWEPT_FACE",FACE,{"disambiguationData":[OSD([subQ2]),TDD([makeQuery(id+"F2.opExtrude","CAP_EDGE",EDGE,{"disambiguationData":[OSD([subQ2])],"isStart":false})])]}),subQ23,makeQuery(id+"F7.opExtrude","SWEPT_FACE",FACE,{"disambiguationData":[OSD([subQ15,subQ4,subQ2]),TDD([makeQuery(id+"F5.imprint","IMPRINT",EDGE,{"disambiguationData":[TD([[makeQuery(id+"F5.imprint","INTERSECT",VERTEX,{"derivedFrom":[subQ21,subQ18,sQuery(id+"F5.wireOp",EDGE,"E4")]}),1.0]])],"derivedFrom":subQ21})])]}),makeQuery(id+"F7.opExtrude","SWEPT_FACE",FACE,{"disambiguationData":[OSD([subQ15,subQ4,subQ2]),TDD([makeQuery(id+"F5.imprint","IMPRINT",EDGE,{"disambiguationData":[TD([[makeQuery(id+"F5.imprint","INTERSECT",VERTEX,{"derivedFrom":[subQ21,subQ17,sQuery(id+"F5.wireOp",EDGE,"E6")]}),-1.0]])],"derivedFrom":subQ21})])]}),makeQuery(id+"F7.opExtrude","SWEPT_FACE",FACE,{"disambiguationData":[OSD([subQ15,subQ4,subQ2]),TDD([makeQuery(id+"F5.imprint","IMPRINT",EDGE,{"disambiguationData":[TD([[makeQuery(id+"F5.imprint","INTERSECT",VERTEX,{"derivedFrom":[subQ16,sQuery(id+"F5.wireOp",EDGE,"E1"),subQ17]}),1.0]])],"derivedFrom":subQ16})])]}),makeQuery(id+"F7.opExtrude","SWEPT_FACE",FACE,{"disambiguationData":[OSD([subQ15,subQ4,subQ2]),TDD([makeQuery(id+"F5.imprint","IMPRINT",EDGE,{"disambiguationData":[TD([[makeQuery(id+"F5.imprint","INTERSECT",VERTEX,{"derivedFrom":[subQ16,subQ19,sQuery(id+"F5.wireOp",EDGE,"E9")]}),-1.0]])],"derivedFrom":subQ16})])]}),makeQuery(id+"F7.opExtrude","SWEPT_FACE",FACE,{"disambiguationData":[OSD([subQ15,subQ4,subQ2]),TDD([makeQuery(id+"F5.imprint","IMPRINT",EDGE,{"disambiguationData":[TD([[makeQuery(id+"F5.imprint","INTERSECT",VERTEX,{"derivedFrom":[subQ16,subQ14,sQuery(id+"F5.wireOp",EDGE,"E14")]}),1.0]])],"derivedFrom":subQ16})])]}),makeQuery(id+"F9.opExtrude","SWEPT_FACE",FACE,{"disambiguationData":[OSD([subQ1])]}),makeQuery(id+"F9.opExtrude","SWEPT_FACE",FACE,{"disambiguationData":[OSD([subQ12])]}),makeQuery(id+"F9.opExtrude","SWEPT_FACE",FACE,{"disambiguationData":[OSD([subQ11])]}),makeQuery(id+"F9.opExtrude","SWEPT_FACE",FACE,{"disambiguationData":[OSD([subQ7])]}),makeQuery(id+"F9.opExtrude","SWEPT_FACE",FACE,{"disambiguationData":[OSD([subQ3,subQ4,subQ2]),TDD([makeQuery(id+"F6.imprint","IMPRINT",EDGE,{"disambiguationData":[TD([[makeQuery(id+"F6.imprint","INTERSECT",VERTEX,{"derivedFrom":[subQ8,subQ0,subQ12]}),1.0]])],"derivedFrom":subQ8})])]}),makeQuery(id+"F9.opExtrude","SWEPT_FACE",FACE,{"disambiguationData":[OSD([subQ3,subQ4,subQ2]),TDD([makeQuery(id+"F6.imprint","IMPRINT",EDGE,{"disambiguationData":[TD([[makeQuery(id+"F6.imprint","INTERSECT",VERTEX,{"derivedFrom":[subQ8,subQ6,sQuery(id+"F6.wireOp",EDGE,"E27")]}),-1.0]])],"derivedFrom":subQ8})])]}),makeQuery(id+"F9.opExtrude","SWEPT_FACE",FACE,{"disambiguationData":[OSD([subQ3,subQ4,subQ2]),TDD([makeQuery(id+"F6.imprint","IMPRINT",EDGE,{"disambiguationData":[TD([[makeQuery(id+"F6.imprint","INTERSECT",VERTEX,{"derivedFrom":[subQ5,subQ1,subQ0]}),-1.0]])],"derivedFrom":subQ5})])]}),makeQuery(id+"F9.opExtrude","SWEPT_FACE",FACE,{"disambiguationData":[OSD([subQ3,subQ4,subQ2]),TDD([makeQuery(id+"F6.imprint","IMPRINT",EDGE,{"disambiguationData":[TD([[makeQuery(id+"F6.imprint","INTERSECT",VERTEX,{"derivedFrom":[subQ5,subQ13,sQuery(id+"F6.wireOp",EDGE,"E22")]}),1.0]])],"derivedFrom":subQ5})])]}),makeQuery(id+"F9.opExtrude","SWEPT_FACE",FACE,{"disambiguationData":[OSD([subQ3,subQ4,subQ2]),TDD([makeQuery(id+"F6.imprint","IMPRINT",EDGE,{"disambiguationData":[TD([[makeQuery(id+"F6.imprint","INTERSECT",VERTEX,{"derivedFrom":[subQ5,subQ9,sQuery(id+"F6.wireOp",EDGE,"E30")]}),-1.0]])],"derivedFrom":subQ5})])]})])],"derivedFrom":makeQuery(id+"F4.boolean.opBoolean","MERGE",FACE,{"derivedFrom":[makeQuery(id+"F3.boolean.opBoolean","MERGE",FACE,{"derivedFrom":[makeQuery(id+"F2.boolean.opBoolean","MERGE",FACE,{"derivedFrom":[subQ22,subQ10]}),subQ20]}),subQ23]})});}
            var Q3;
            {var subQ0=sQuery(id+"F6.wireOp",EDGE,"E18");var subQ1=sQuery(id+"F6.wireOp",EDGE,"E17");var subQ2=sQuery(id+"F0.wireOp",EDGE,"E0.right");var subQ3=sQuery(id+"F0.wireOp",EDGE,"E0.top");var subQ4=sQuery(id+"F0.wireOp",EDGE,"E0.left");var subQ5=makeQuery(id+"F4.boolean.opBoolean","MERGE",EDGE,{"derivedFrom":[makeQuery(id+"F3.boolean.opBoolean","MERGE",EDGE,{"derivedFrom":[makeQuery(id+"F2.opExtrude","CAP_EDGE",EDGE,{"disambiguationData":[OSD([subQ3])],"isStart":false}),makeQuery(id+"F3.opExtrude","SWEPT_EDGE",EDGE,{"disambiguationData":[OSD([subQ3,subQ4]),TDD([makeQuery(id+"F2.opExtrude","CAP_VERTEX",VERTEX,{"disambiguationData":[OSD([subQ3,subQ4])],"isStart":false})])]})]}),makeQuery(id+"F4.opExtrude","SWEPT_EDGE",EDGE,{"disambiguationData":[OSD([subQ3,subQ2]),TDD([makeQuery(id+"F2.opExtrude","CAP_VERTEX",VERTEX,{"disambiguationData":[OSD([subQ3,subQ2])],"isStart":false})])]})]});var subQ6=sQuery(id+"F6.wireOp",EDGE,"E26");var subQ7=sQuery(id+"F6.wireOp",EDGE,"E25");var subQ8=sQuery(id+"F6.wireOp",EDGE,"E27");var subQ9=makeQuery(id+"F4.boolean.opBoolean","MERGE",EDGE,{"derivedFrom":[makeQuery(id+"F3.boolean.opBoolean","MERGE",EDGE,{"derivedFrom":[makeQuery(id+"F1.opExtrude","CAP_EDGE",EDGE,{"disambiguationData":[OSD([subQ3])],"isStart":false}),makeQuery(id+"F3.opExtrude","SWEPT_EDGE",EDGE,{"disambiguationData":[OSD([subQ3,subQ4]),TDD([makeQuery(id+"F1.opExtrude","CAP_VERTEX",VERTEX,{"disambiguationData":[OSD([subQ3,subQ4])],"isStart":false})])]})]}),makeQuery(id+"F4.opExtrude","SWEPT_EDGE",EDGE,{"disambiguationData":[OSD([subQ3,subQ2]),TDD([makeQuery(id+"F1.opExtrude","CAP_VERTEX",VERTEX,{"disambiguationData":[OSD([subQ3,subQ2])],"isStart":false})])]})]});var subQ10=sQuery(id+"F6.wireOp",EDGE,"E29");var subQ11=sQuery(id+"F6.wireOp",EDGE,"E28");var subQ12=makeQuery(id+"F2.opExtrude","SWEPT_FACE",FACE,{"disambiguationData":[OSD([subQ3])]});var subQ13=sQuery(id+"F6.wireOp",EDGE,"E21");var subQ14=sQuery(id+"F5.wireOp",EDGE,"E13");var subQ15=sQuery(id+"F0.wireOp",EDGE,"E0.bottom");var subQ16=makeQuery(id+"F4.boolean.opBoolean","MERGE",EDGE,{"derivedFrom":[makeQuery(id+"F3.boolean.opBoolean","MERGE",EDGE,{"derivedFrom":[makeQuery(id+"F2.opExtrude","CAP_EDGE",EDGE,{"disambiguationData":[OSD([subQ15])],"isStart":false}),makeQuery(id+"F3.opExtrude","SWEPT_EDGE",EDGE,{"disambiguationData":[OSD([subQ15,subQ4]),TDD([makeQuery(id+"F2.opExtrude","CAP_VERTEX",VERTEX,{"disambiguationData":[OSD([subQ15,subQ4])],"isStart":false})])]})]}),makeQuery(id+"F4.opExtrude","SWEPT_EDGE",EDGE,{"disambiguationData":[OSD([subQ15,subQ2]),TDD([makeQuery(id+"F2.opExtrude","CAP_VERTEX",VERTEX,{"disambiguationData":[OSD([subQ15,subQ2])],"isStart":false})])]})]});var subQ17=sQuery(id+"F5.wireOp",EDGE,"E5");var subQ18=sQuery(id+"F5.wireOp",EDGE,"E3");var subQ19=sQuery(id+"F5.wireOp",EDGE,"E8");var subQ20=makeQuery(id+"F3.opExtrude","SWEPT_FACE",FACE,{"disambiguationData":[OSD([subQ3,subQ4])]});var subQ21=makeQuery(id+"F4.boolean.opBoolean","MERGE",EDGE,{"derivedFrom":[makeQuery(id+"F3.boolean.opBoolean","MERGE",EDGE,{"derivedFrom":[makeQuery(id+"F1.opExtrude","CAP_EDGE",EDGE,{"disambiguationData":[OSD([subQ15])],"isStart":false}),makeQuery(id+"F3.opExtrude","SWEPT_EDGE",EDGE,{"disambiguationData":[OSD([subQ15,subQ4]),TDD([makeQuery(id+"F1.opExtrude","CAP_VERTEX",VERTEX,{"disambiguationData":[OSD([subQ15,subQ4])],"isStart":false})])]})]}),makeQuery(id+"F4.opExtrude","SWEPT_EDGE",EDGE,{"disambiguationData":[OSD([subQ15,subQ2]),TDD([makeQuery(id+"F1.opExtrude","CAP_VERTEX",VERTEX,{"disambiguationData":[OSD([subQ15,subQ2])],"isStart":false})])]})]});var subQ22=makeQuery(id+"F1.opExtrude","SWEPT_FACE",FACE,{"disambiguationData":[OSD([subQ3])]});var subQ23=makeQuery(id+"F4.opExtrude","SWEPT_FACE",FACE,{"disambiguationData":[OSD([subQ3,subQ2])]});Q3=makeQuery(id+"F9.boolean.opBoolean","SPLIT",FACE,{"disambiguationData":[TD([makeQuery(id+"F1.opExtrude","CAP_FACE",FACE,{"disambiguationData":[OSD([subQ15,subQ3,subQ4,subQ2])],"isStart":false}),subQ22,subQ12,makeQuery(id+"F2.opExtrude","CAP_FACE",FACE,{"disambiguationData":[OSD([subQ15,subQ3,subQ4,subQ2])],"isStart":false}),makeQuery(id+"F3.opExtrude","SWEPT_FACE",FACE,{"disambiguationData":[OSD([subQ4]),TDD([makeQuery(id+"F1.opExtrude","CAP_EDGE",EDGE,{"disambiguationData":[OSD([subQ4])],"isStart":false})])]}),makeQuery(id+"F3.opExtrude","SWEPT_FACE",FACE,{"disambiguationData":[OSD([subQ4]),TDD([makeQuery(id+"F2.opExtrude","CAP_EDGE",EDGE,{"disambiguationData":[OSD([subQ4])],"isStart":false})])]}),subQ20,makeQuery(id+"F4.opExtrude","SWEPT_FACE",FACE,{"disambiguationData":[OSD([subQ2]),TDD([makeQuery(id+"F1.opExtrude","CAP_EDGE",EDGE,{"disambiguationData":[OSD([subQ2])],"isStart":false})])]}),makeQuery(id+"F4.opExtrude","SWEPT_FACE",FACE,{"disambiguationData":[OSD([subQ2]),TDD([makeQuery(id+"F2.opExtrude","CAP_EDGE",EDGE,{"disambiguationData":[OSD([subQ2])],"isStart":false})])]}),subQ23,makeQuery(id+"F7.opExtrude","SWEPT_FACE",FACE,{"disambiguationData":[OSD([subQ15,subQ4,subQ2]),TDD([makeQuery(id+"F5.imprint","IMPRINT",EDGE,{"disambiguationData":[TD([[makeQuery(id+"F5.imprint","INTERSECT",VERTEX,{"derivedFrom":[subQ21,subQ18,sQuery(id+"F5.wireOp",EDGE,"E4")]}),1.0]])],"derivedFrom":subQ21})])]}),makeQuery(id+"F7.opExtrude","SWEPT_FACE",FACE,{"disambiguationData":[OSD([subQ15,subQ4,subQ2]),TDD([makeQuery(id+"F5.imprint","IMPRINT",EDGE,{"disambiguationData":[TD([[makeQuery(id+"F5.imprint","INTERSECT",VERTEX,{"derivedFrom":[subQ21,subQ17,sQuery(id+"F5.wireOp",EDGE,"E6")]}),-1.0]])],"derivedFrom":subQ21})])]}),makeQuery(id+"F7.opExtrude","SWEPT_FACE",FACE,{"disambiguationData":[OSD([subQ15,subQ4,subQ2]),TDD([makeQuery(id+"F5.imprint","IMPRINT",EDGE,{"disambiguationData":[TD([[makeQuery(id+"F5.imprint","INTERSECT",VERTEX,{"derivedFrom":[subQ16,sQuery(id+"F5.wireOp",EDGE,"E1"),subQ17]}),1.0]])],"derivedFrom":subQ16})])]}),makeQuery(id+"F7.opExtrude","SWEPT_FACE",FACE,{"disambiguationData":[OSD([subQ15,subQ4,subQ2]),TDD([makeQuery(id+"F5.imprint","IMPRINT",EDGE,{"disambiguationData":[TD([[makeQuery(id+"F5.imprint","INTERSECT",VERTEX,{"derivedFrom":[subQ16,subQ19,sQuery(id+"F5.wireOp",EDGE,"E9")]}),-1.0]])],"derivedFrom":subQ16})])]}),makeQuery(id+"F7.opExtrude","SWEPT_FACE",FACE,{"disambiguationData":[OSD([subQ15,subQ4,subQ2]),TDD([makeQuery(id+"F5.imprint","IMPRINT",EDGE,{"disambiguationData":[TD([[makeQuery(id+"F5.imprint","INTERSECT",VERTEX,{"derivedFrom":[subQ16,subQ14,sQuery(id+"F5.wireOp",EDGE,"E14")]}),1.0]])],"derivedFrom":subQ16})])]}),makeQuery(id+"F9.opExtrude","SWEPT_FACE",FACE,{"disambiguationData":[OSD([subQ1])]}),makeQuery(id+"F9.opExtrude","SWEPT_FACE",FACE,{"disambiguationData":[OSD([subQ7])]}),makeQuery(id+"F9.opExtrude","SWEPT_FACE",FACE,{"disambiguationData":[OSD([subQ8])]}),makeQuery(id+"F9.opExtrude","SWEPT_FACE",FACE,{"disambiguationData":[OSD([subQ11])]}),makeQuery(id+"F9.opExtrude","SWEPT_FACE",FACE,{"disambiguationData":[OSD([subQ3,subQ4,subQ2]),TDD([makeQuery(id+"F6.imprint","IMPRINT",EDGE,{"disambiguationData":[TD([[makeQuery(id+"F6.imprint","INTERSECT",VERTEX,{"derivedFrom":[subQ9,subQ0,sQuery(id+"F6.wireOp",EDGE,"E19")]}),1.0]])],"derivedFrom":subQ9})])]}),makeQuery(id+"F9.opExtrude","SWEPT_FACE",FACE,{"disambiguationData":[OSD([subQ3,subQ4,subQ2]),TDD([makeQuery(id+"F6.imprint","IMPRINT",EDGE,{"disambiguationData":[TD([[makeQuery(id+"F6.imprint","INTERSECT",VERTEX,{"derivedFrom":[subQ9,subQ6,subQ8]}),-1.0]])],"derivedFrom":subQ9})])]}),makeQuery(id+"F9.opExtrude","SWEPT_FACE",FACE,{"disambiguationData":[OSD([subQ3,subQ4,subQ2]),TDD([makeQuery(id+"F6.imprint","IMPRINT",EDGE,{"disambiguationData":[TD([[makeQuery(id+"F6.imprint","INTERSECT",VERTEX,{"derivedFrom":[subQ5,subQ1,subQ0]}),-1.0]])],"derivedFrom":subQ5})])]}),makeQuery(id+"F9.opExtrude","SWEPT_FACE",FACE,{"disambiguationData":[OSD([subQ3,subQ4,subQ2]),TDD([makeQuery(id+"F6.imprint","IMPRINT",EDGE,{"disambiguationData":[TD([[makeQuery(id+"F6.imprint","INTERSECT",VERTEX,{"derivedFrom":[subQ5,subQ13,sQuery(id+"F6.wireOp",EDGE,"E22")]}),1.0]])],"derivedFrom":subQ5})])]}),makeQuery(id+"F9.opExtrude","SWEPT_FACE",FACE,{"disambiguationData":[OSD([subQ3,subQ4,subQ2]),TDD([makeQuery(id+"F6.imprint","IMPRINT",EDGE,{"disambiguationData":[TD([[makeQuery(id+"F6.imprint","INTERSECT",VERTEX,{"derivedFrom":[subQ5,subQ10,sQuery(id+"F6.wireOp",EDGE,"E30")]}),-1.0]])],"derivedFrom":subQ5})])]})])],"derivedFrom":makeQuery(id+"F4.boolean.opBoolean","MERGE",FACE,{"derivedFrom":[makeQuery(id+"F3.boolean.opBoolean","MERGE",FACE,{"derivedFrom":[makeQuery(id+"F2.boolean.opBoolean","MERGE",FACE,{"derivedFrom":[subQ22,subQ12]}),subQ20]}),subQ23]})});}
            var Q4;
            {var subQ0=sQuery(id+"F6.wireOp",EDGE,"E18");var subQ1=sQuery(id+"F0.wireOp",EDGE,"E0.right");var subQ2=sQuery(id+"F0.wireOp",EDGE,"E0.top");var subQ3=sQuery(id+"F0.wireOp",EDGE,"E0.left");var subQ4=makeQuery(id+"F4.boolean.opBoolean","MERGE",EDGE,{"derivedFrom":[makeQuery(id+"F3.boolean.opBoolean","MERGE",EDGE,{"derivedFrom":[makeQuery(id+"F2.opExtrude","CAP_EDGE",EDGE,{"disambiguationData":[OSD([subQ2])],"isStart":false}),makeQuery(id+"F3.opExtrude","SWEPT_EDGE",EDGE,{"disambiguationData":[OSD([subQ2,subQ3]),TDD([makeQuery(id+"F2.opExtrude","CAP_VERTEX",VERTEX,{"disambiguationData":[OSD([subQ2,subQ3])],"isStart":false})])]})]}),makeQuery(id+"F4.opExtrude","SWEPT_EDGE",EDGE,{"disambiguationData":[OSD([subQ2,subQ1]),TDD([makeQuery(id+"F2.opExtrude","CAP_VERTEX",VERTEX,{"disambiguationData":[OSD([subQ2,subQ1])],"isStart":false})])]})]});var subQ5=sQuery(id+"F6.wireOp",EDGE,"E26");var subQ6=sQuery(id+"F6.wireOp",EDGE,"E27");var subQ7=makeQuery(id+"F4.boolean.opBoolean","MERGE",EDGE,{"derivedFrom":[makeQuery(id+"F3.boolean.opBoolean","MERGE",EDGE,{"derivedFrom":[makeQuery(id+"F1.opExtrude","CAP_EDGE",EDGE,{"disambiguationData":[OSD([subQ2])],"isStart":false}),makeQuery(id+"F3.opExtrude","SWEPT_EDGE",EDGE,{"disambiguationData":[OSD([subQ2,subQ3]),TDD([makeQuery(id+"F1.opExtrude","CAP_VERTEX",VERTEX,{"disambiguationData":[OSD([subQ2,subQ3])],"isStart":false})])]})]}),makeQuery(id+"F4.opExtrude","SWEPT_EDGE",EDGE,{"disambiguationData":[OSD([subQ2,subQ1]),TDD([makeQuery(id+"F1.opExtrude","CAP_VERTEX",VERTEX,{"disambiguationData":[OSD([subQ2,subQ1])],"isStart":false})])]})]});var subQ8=sQuery(id+"F6.wireOp",EDGE,"E29");var subQ9=sQuery(id+"F6.wireOp",EDGE,"E28");var subQ10=makeQuery(id+"F2.opExtrude","SWEPT_FACE",FACE,{"disambiguationData":[OSD([subQ2])]});var subQ11=sQuery(id+"F6.wireOp",EDGE,"E21");var subQ12=sQuery(id+"F5.wireOp",EDGE,"E13");var subQ13=sQuery(id+"F0.wireOp",EDGE,"E0.bottom");var subQ14=makeQuery(id+"F4.boolean.opBoolean","MERGE",EDGE,{"derivedFrom":[makeQuery(id+"F3.boolean.opBoolean","MERGE",EDGE,{"derivedFrom":[makeQuery(id+"F2.opExtrude","CAP_EDGE",EDGE,{"disambiguationData":[OSD([subQ13])],"isStart":false}),makeQuery(id+"F3.opExtrude","SWEPT_EDGE",EDGE,{"disambiguationData":[OSD([subQ13,subQ3]),TDD([makeQuery(id+"F2.opExtrude","CAP_VERTEX",VERTEX,{"disambiguationData":[OSD([subQ13,subQ3])],"isStart":false})])]})]}),makeQuery(id+"F4.opExtrude","SWEPT_EDGE",EDGE,{"disambiguationData":[OSD([subQ13,subQ1]),TDD([makeQuery(id+"F2.opExtrude","CAP_VERTEX",VERTEX,{"disambiguationData":[OSD([subQ13,subQ1])],"isStart":false})])]})]});var subQ15=sQuery(id+"F5.wireOp",EDGE,"E5");var subQ16=sQuery(id+"F5.wireOp",EDGE,"E3");var subQ17=sQuery(id+"F6.wireOp",EDGE,"E31");var subQ18=sQuery(id+"F5.wireOp",EDGE,"E8");var subQ19=makeQuery(id+"F3.opExtrude","SWEPT_FACE",FACE,{"disambiguationData":[OSD([subQ2,subQ3])]});var subQ20=sQuery(id+"F6.wireOp",EDGE,"E30");var subQ21=makeQuery(id+"F4.boolean.opBoolean","MERGE",EDGE,{"derivedFrom":[makeQuery(id+"F3.boolean.opBoolean","MERGE",EDGE,{"derivedFrom":[makeQuery(id+"F1.opExtrude","CAP_EDGE",EDGE,{"disambiguationData":[OSD([subQ13])],"isStart":false}),makeQuery(id+"F3.opExtrude","SWEPT_EDGE",EDGE,{"disambiguationData":[OSD([subQ13,subQ3]),TDD([makeQuery(id+"F1.opExtrude","CAP_VERTEX",VERTEX,{"disambiguationData":[OSD([subQ13,subQ3])],"isStart":false})])]})]}),makeQuery(id+"F4.opExtrude","SWEPT_EDGE",EDGE,{"disambiguationData":[OSD([subQ13,subQ1]),TDD([makeQuery(id+"F1.opExtrude","CAP_VERTEX",VERTEX,{"disambiguationData":[OSD([subQ13,subQ1])],"isStart":false})])]})]});var subQ22=makeQuery(id+"F1.opExtrude","SWEPT_FACE",FACE,{"disambiguationData":[OSD([subQ2])]});var subQ23=makeQuery(id+"F4.opExtrude","SWEPT_FACE",FACE,{"disambiguationData":[OSD([subQ2,subQ1])]});Q4=makeQuery(id+"F9.boolean.opBoolean","SPLIT",FACE,{"disambiguationData":[TD([makeQuery(id+"F1.opExtrude","CAP_FACE",FACE,{"disambiguationData":[OSD([subQ13,subQ2,subQ3,subQ1])],"isStart":false}),subQ22,subQ10,makeQuery(id+"F2.opExtrude","CAP_FACE",FACE,{"disambiguationData":[OSD([subQ13,subQ2,subQ3,subQ1])],"isStart":false}),makeQuery(id+"F3.opExtrude","SWEPT_FACE",FACE,{"disambiguationData":[OSD([subQ3]),TDD([makeQuery(id+"F1.opExtrude","CAP_EDGE",EDGE,{"disambiguationData":[OSD([subQ3])],"isStart":false})])]}),makeQuery(id+"F3.opExtrude","SWEPT_FACE",FACE,{"disambiguationData":[OSD([subQ3]),TDD([makeQuery(id+"F2.opExtrude","CAP_EDGE",EDGE,{"disambiguationData":[OSD([subQ3])],"isStart":false})])]}),subQ19,makeQuery(id+"F4.opExtrude","SWEPT_FACE",FACE,{"disambiguationData":[OSD([subQ1]),TDD([makeQuery(id+"F1.opExtrude","CAP_EDGE",EDGE,{"disambiguationData":[OSD([subQ1])],"isStart":false})])]}),makeQuery(id+"F4.opExtrude","SWEPT_FACE",FACE,{"disambiguationData":[OSD([subQ1]),TDD([makeQuery(id+"F2.opExtrude","CAP_EDGE",EDGE,{"disambiguationData":[OSD([subQ1])],"isStart":false})])]}),subQ23,makeQuery(id+"F7.opExtrude","SWEPT_FACE",FACE,{"disambiguationData":[OSD([subQ13,subQ3,subQ1]),TDD([makeQuery(id+"F5.imprint","IMPRINT",EDGE,{"disambiguationData":[TD([[makeQuery(id+"F5.imprint","INTERSECT",VERTEX,{"derivedFrom":[subQ21,subQ16,sQuery(id+"F5.wireOp",EDGE,"E4")]}),1.0]])],"derivedFrom":subQ21})])]}),makeQuery(id+"F7.opExtrude","SWEPT_FACE",FACE,{"disambiguationData":[OSD([subQ13,subQ3,subQ1]),TDD([makeQuery(id+"F5.imprint","IMPRINT",EDGE,{"disambiguationData":[TD([[makeQuery(id+"F5.imprint","INTERSECT",VERTEX,{"derivedFrom":[subQ21,subQ15,sQuery(id+"F5.wireOp",EDGE,"E6")]}),-1.0]])],"derivedFrom":subQ21})])]}),makeQuery(id+"F7.opExtrude","SWEPT_FACE",FACE,{"disambiguationData":[OSD([subQ13,subQ3,subQ1]),TDD([makeQuery(id+"F5.imprint","IMPRINT",EDGE,{"disambiguationData":[TD([[makeQuery(id+"F5.imprint","INTERSECT",VERTEX,{"derivedFrom":[subQ14,sQuery(id+"F5.wireOp",EDGE,"E1"),subQ15]}),1.0]])],"derivedFrom":subQ14})])]}),makeQuery(id+"F7.opExtrude","SWEPT_FACE",FACE,{"disambiguationData":[OSD([subQ13,subQ3,subQ1]),TDD([makeQuery(id+"F5.imprint","IMPRINT",EDGE,{"disambiguationData":[TD([[makeQuery(id+"F5.imprint","INTERSECT",VERTEX,{"derivedFrom":[subQ14,subQ18,sQuery(id+"F5.wireOp",EDGE,"E9")]}),-1.0]])],"derivedFrom":subQ14})])]}),makeQuery(id+"F7.opExtrude","SWEPT_FACE",FACE,{"disambiguationData":[OSD([subQ13,subQ3,subQ1]),TDD([makeQuery(id+"F5.imprint","IMPRINT",EDGE,{"disambiguationData":[TD([[makeQuery(id+"F5.imprint","INTERSECT",VERTEX,{"derivedFrom":[subQ14,subQ12,sQuery(id+"F5.wireOp",EDGE,"E14")]}),1.0]])],"derivedFrom":subQ14})])]}),makeQuery(id+"F9.opExtrude","SWEPT_FACE",FACE,{"disambiguationData":[OSD([subQ6])]}),makeQuery(id+"F9.opExtrude","SWEPT_FACE",FACE,{"disambiguationData":[OSD([subQ9])]}),makeQuery(id+"F9.opExtrude","SWEPT_FACE",FACE,{"disambiguationData":[OSD([subQ20])]}),makeQuery(id+"F9.opExtrude","SWEPT_FACE",FACE,{"disambiguationData":[OSD([subQ17])]}),makeQuery(id+"F9.opExtrude","SWEPT_FACE",FACE,{"disambiguationData":[OSD([subQ2,subQ3,subQ1]),TDD([makeQuery(id+"F6.imprint","IMPRINT",EDGE,{"disambiguationData":[TD([[makeQuery(id+"F6.imprint","INTERSECT",VERTEX,{"derivedFrom":[subQ7,subQ0,sQuery(id+"F6.wireOp",EDGE,"E19")]}),1.0]])],"derivedFrom":subQ7})])]}),makeQuery(id+"F9.opExtrude","SWEPT_FACE",FACE,{"disambiguationData":[OSD([subQ2,subQ3,subQ1]),TDD([makeQuery(id+"F6.imprint","IMPRINT",EDGE,{"disambiguationData":[TD([[makeQuery(id+"F6.imprint","INTERSECT",VERTEX,{"derivedFrom":[subQ7,subQ5,subQ6]}),-1.0]])],"derivedFrom":subQ7})])]}),makeQuery(id+"F9.opExtrude","SWEPT_FACE",FACE,{"disambiguationData":[OSD([subQ2,subQ3,subQ1]),TDD([makeQuery(id+"F6.imprint","IMPRINT",EDGE,{"disambiguationData":[TD([[makeQuery(id+"F6.imprint","INTERSECT",VERTEX,{"derivedFrom":[subQ4,sQuery(id+"F6.wireOp",EDGE,"E17"),subQ0]}),-1.0]])],"derivedFrom":subQ4})])]}),makeQuery(id+"F9.opExtrude","SWEPT_FACE",FACE,{"disambiguationData":[OSD([subQ2,subQ3,subQ1]),TDD([makeQuery(id+"F6.imprint","IMPRINT",EDGE,{"disambiguationData":[TD([[makeQuery(id+"F6.imprint","INTERSECT",VERTEX,{"derivedFrom":[subQ4,subQ11,sQuery(id+"F6.wireOp",EDGE,"E22")]}),1.0]])],"derivedFrom":subQ4})])]}),makeQuery(id+"F9.opExtrude","SWEPT_FACE",FACE,{"disambiguationData":[OSD([subQ2,subQ3,subQ1]),TDD([makeQuery(id+"F6.imprint","IMPRINT",EDGE,{"disambiguationData":[TD([[makeQuery(id+"F6.imprint","INTERSECT",VERTEX,{"derivedFrom":[subQ4,subQ8,subQ20]}),-1.0]])],"derivedFrom":subQ4})])]})])],"derivedFrom":makeQuery(id+"F4.boolean.opBoolean","MERGE",FACE,{"derivedFrom":[makeQuery(id+"F3.boolean.opBoolean","MERGE",FACE,{"derivedFrom":[makeQuery(id+"F2.boolean.opBoolean","MERGE",FACE,{"derivedFrom":[subQ22,subQ10]}),subQ19]}),subQ23]})});}
            var Q5;
            {var subQ0=sQuery(id+"F6.wireOp",EDGE,"E18");var subQ1=sQuery(id+"F0.wireOp",EDGE,"E0.right");var subQ2=sQuery(id+"F0.wireOp",EDGE,"E0.top");var subQ3=sQuery(id+"F0.wireOp",EDGE,"E0.left");var subQ4=makeQuery(id+"F4.boolean.opBoolean","MERGE",EDGE,{"derivedFrom":[makeQuery(id+"F3.boolean.opBoolean","MERGE",EDGE,{"derivedFrom":[makeQuery(id+"F2.opExtrude","CAP_EDGE",EDGE,{"disambiguationData":[OSD([subQ2])],"isStart":false}),makeQuery(id+"F3.opExtrude","SWEPT_EDGE",EDGE,{"disambiguationData":[OSD([subQ2,subQ3]),TDD([makeQuery(id+"F2.opExtrude","CAP_VERTEX",VERTEX,{"disambiguationData":[OSD([subQ2,subQ3])],"isStart":false})])]})]}),makeQuery(id+"F4.opExtrude","SWEPT_EDGE",EDGE,{"disambiguationData":[OSD([subQ2,subQ1]),TDD([makeQuery(id+"F2.opExtrude","CAP_VERTEX",VERTEX,{"disambiguationData":[OSD([subQ2,subQ1])],"isStart":false})])]})]});var subQ5=sQuery(id+"F6.wireOp",EDGE,"E26");var subQ6=makeQuery(id+"F4.boolean.opBoolean","MERGE",EDGE,{"derivedFrom":[makeQuery(id+"F3.boolean.opBoolean","MERGE",EDGE,{"derivedFrom":[makeQuery(id+"F1.opExtrude","CAP_EDGE",EDGE,{"disambiguationData":[OSD([subQ2])],"isStart":false}),makeQuery(id+"F3.opExtrude","SWEPT_EDGE",EDGE,{"disambiguationData":[OSD([subQ2,subQ3]),TDD([makeQuery(id+"F1.opExtrude","CAP_VERTEX",VERTEX,{"disambiguationData":[OSD([subQ2,subQ3])],"isStart":false})])]})]}),makeQuery(id+"F4.opExtrude","SWEPT_EDGE",EDGE,{"disambiguationData":[OSD([subQ2,subQ1]),TDD([makeQuery(id+"F1.opExtrude","CAP_VERTEX",VERTEX,{"disambiguationData":[OSD([subQ2,subQ1])],"isStart":false})])]})]});var subQ7=sQuery(id+"F6.wireOp",EDGE,"E29");var subQ8=makeQuery(id+"F2.opExtrude","SWEPT_FACE",FACE,{"disambiguationData":[OSD([subQ2])]});var subQ9=sQuery(id+"F6.wireOp",EDGE,"E21");var subQ10=sQuery(id+"F5.wireOp",EDGE,"E13");var subQ11=sQuery(id+"F0.wireOp",EDGE,"E0.bottom");var subQ12=makeQuery(id+"F4.boolean.opBoolean","MERGE",EDGE,{"derivedFrom":[makeQuery(id+"F3.boolean.opBoolean","MERGE",EDGE,{"derivedFrom":[makeQuery(id+"F2.opExtrude","CAP_EDGE",EDGE,{"disambiguationData":[OSD([subQ11])],"isStart":false}),makeQuery(id+"F3.opExtrude","SWEPT_EDGE",EDGE,{"disambiguationData":[OSD([subQ11,subQ3]),TDD([makeQuery(id+"F2.opExtrude","CAP_VERTEX",VERTEX,{"disambiguationData":[OSD([subQ11,subQ3])],"isStart":false})])]})]}),makeQuery(id+"F4.opExtrude","SWEPT_EDGE",EDGE,{"disambiguationData":[OSD([subQ11,subQ1]),TDD([makeQuery(id+"F2.opExtrude","CAP_VERTEX",VERTEX,{"disambiguationData":[OSD([subQ11,subQ1])],"isStart":false})])]})]});var subQ13=sQuery(id+"F5.wireOp",EDGE,"E5");var subQ14=sQuery(id+"F5.wireOp",EDGE,"E3");var subQ15=sQuery(id+"F6.wireOp",EDGE,"E31");var subQ16=sQuery(id+"F5.wireOp",EDGE,"E8");var subQ17=makeQuery(id+"F3.opExtrude","SWEPT_FACE",FACE,{"disambiguationData":[OSD([subQ2,subQ3])]});var subQ18=sQuery(id+"F6.wireOp",EDGE,"E30");var subQ19=makeQuery(id+"F4.boolean.opBoolean","MERGE",EDGE,{"derivedFrom":[makeQuery(id+"F3.boolean.opBoolean","MERGE",EDGE,{"derivedFrom":[makeQuery(id+"F1.opExtrude","CAP_EDGE",EDGE,{"disambiguationData":[OSD([subQ11])],"isStart":false}),makeQuery(id+"F3.opExtrude","SWEPT_EDGE",EDGE,{"disambiguationData":[OSD([subQ11,subQ3]),TDD([makeQuery(id+"F1.opExtrude","CAP_VERTEX",VERTEX,{"disambiguationData":[OSD([subQ11,subQ3])],"isStart":false})])]})]}),makeQuery(id+"F4.opExtrude","SWEPT_EDGE",EDGE,{"disambiguationData":[OSD([subQ11,subQ1]),TDD([makeQuery(id+"F1.opExtrude","CAP_VERTEX",VERTEX,{"disambiguationData":[OSD([subQ11,subQ1])],"isStart":false})])]})]});var subQ20=makeQuery(id+"F1.opExtrude","SWEPT_FACE",FACE,{"disambiguationData":[OSD([subQ2])]});var subQ21=makeQuery(id+"F4.opExtrude","SWEPT_FACE",FACE,{"disambiguationData":[OSD([subQ2,subQ1])]});Q5=makeQuery(id+"F9.boolean.opBoolean","SPLIT",FACE,{"disambiguationData":[TD([makeQuery(id+"F1.opExtrude","CAP_FACE",FACE,{"disambiguationData":[OSD([subQ11,subQ2,subQ3,subQ1])],"isStart":false}),subQ20,subQ8,makeQuery(id+"F2.opExtrude","CAP_FACE",FACE,{"disambiguationData":[OSD([subQ11,subQ2,subQ3,subQ1])],"isStart":false}),makeQuery(id+"F3.opExtrude","SWEPT_FACE",FACE,{"disambiguationData":[OSD([subQ3]),TDD([makeQuery(id+"F1.opExtrude","CAP_EDGE",EDGE,{"disambiguationData":[OSD([subQ3])],"isStart":false})])]}),makeQuery(id+"F3.opExtrude","SWEPT_FACE",FACE,{"disambiguationData":[OSD([subQ3]),TDD([makeQuery(id+"F2.opExtrude","CAP_EDGE",EDGE,{"disambiguationData":[OSD([subQ3])],"isStart":false})])]}),subQ17,makeQuery(id+"F4.opExtrude","SWEPT_FACE",FACE,{"disambiguationData":[OSD([subQ1]),TDD([makeQuery(id+"F1.opExtrude","CAP_EDGE",EDGE,{"disambiguationData":[OSD([subQ1])],"isStart":false})])]}),makeQuery(id+"F4.opExtrude","SWEPT_FACE",FACE,{"disambiguationData":[OSD([subQ1]),TDD([makeQuery(id+"F2.opExtrude","CAP_EDGE",EDGE,{"disambiguationData":[OSD([subQ1])],"isStart":false})])]}),subQ21,makeQuery(id+"F4.opExtrude","CAP_FACE",FACE,{"disambiguationData":[OSD([subQ1])],"isStart":false}),makeQuery(id+"F7.opExtrude","SWEPT_FACE",FACE,{"disambiguationData":[OSD([subQ11,subQ3,subQ1]),TDD([makeQuery(id+"F5.imprint","IMPRINT",EDGE,{"disambiguationData":[TD([[makeQuery(id+"F5.imprint","INTERSECT",VERTEX,{"derivedFrom":[subQ19,subQ14,sQuery(id+"F5.wireOp",EDGE,"E4")]}),1.0]])],"derivedFrom":subQ19})])]}),makeQuery(id+"F7.opExtrude","SWEPT_FACE",FACE,{"disambiguationData":[OSD([subQ11,subQ3,subQ1]),TDD([makeQuery(id+"F5.imprint","IMPRINT",EDGE,{"disambiguationData":[TD([[makeQuery(id+"F5.imprint","INTERSECT",VERTEX,{"derivedFrom":[subQ19,subQ13,sQuery(id+"F5.wireOp",EDGE,"E6")]}),-1.0]])],"derivedFrom":subQ19})])]}),makeQuery(id+"F7.opExtrude","SWEPT_FACE",FACE,{"disambiguationData":[OSD([subQ11,subQ3,subQ1]),TDD([makeQuery(id+"F5.imprint","IMPRINT",EDGE,{"disambiguationData":[TD([[makeQuery(id+"F5.imprint","INTERSECT",VERTEX,{"derivedFrom":[subQ12,sQuery(id+"F5.wireOp",EDGE,"E1"),subQ13]}),1.0]])],"derivedFrom":subQ12})])]}),makeQuery(id+"F7.opExtrude","SWEPT_FACE",FACE,{"disambiguationData":[OSD([subQ11,subQ3,subQ1]),TDD([makeQuery(id+"F5.imprint","IMPRINT",EDGE,{"disambiguationData":[TD([[makeQuery(id+"F5.imprint","INTERSECT",VERTEX,{"derivedFrom":[subQ12,subQ16,sQuery(id+"F5.wireOp",EDGE,"E9")]}),-1.0]])],"derivedFrom":subQ12})])]}),makeQuery(id+"F7.opExtrude","SWEPT_FACE",FACE,{"disambiguationData":[OSD([subQ11,subQ3,subQ1]),TDD([makeQuery(id+"F5.imprint","IMPRINT",EDGE,{"disambiguationData":[TD([[makeQuery(id+"F5.imprint","INTERSECT",VERTEX,{"derivedFrom":[subQ12,subQ10,sQuery(id+"F5.wireOp",EDGE,"E14")]}),1.0]])],"derivedFrom":subQ12})])]}),makeQuery(id+"F9.opExtrude","SWEPT_FACE",FACE,{"disambiguationData":[OSD([subQ18])]}),makeQuery(id+"F9.opExtrude","SWEPT_FACE",FACE,{"disambiguationData":[OSD([subQ15])]}),makeQuery(id+"F9.opExtrude","SWEPT_FACE",FACE,{"disambiguationData":[OSD([subQ2,subQ3,subQ1]),TDD([makeQuery(id+"F6.imprint","IMPRINT",EDGE,{"disambiguationData":[TD([[makeQuery(id+"F6.imprint","INTERSECT",VERTEX,{"derivedFrom":[subQ6,subQ0,sQuery(id+"F6.wireOp",EDGE,"E19")]}),1.0]])],"derivedFrom":subQ6})])]}),makeQuery(id+"F9.opExtrude","SWEPT_FACE",FACE,{"disambiguationData":[OSD([subQ2,subQ3,subQ1]),TDD([makeQuery(id+"F6.imprint","IMPRINT",EDGE,{"disambiguationData":[TD([[makeQuery(id+"F6.imprint","INTERSECT",VERTEX,{"derivedFrom":[subQ6,subQ5,sQuery(id+"F6.wireOp",EDGE,"E27")]}),-1.0]])],"derivedFrom":subQ6})])]}),makeQuery(id+"F9.opExtrude","SWEPT_FACE",FACE,{"disambiguationData":[OSD([subQ2,subQ3,subQ1]),TDD([makeQuery(id+"F6.imprint","IMPRINT",EDGE,{"disambiguationData":[TD([[makeQuery(id+"F6.imprint","INTERSECT",VERTEX,{"derivedFrom":[subQ4,sQuery(id+"F6.wireOp",EDGE,"E17"),subQ0]}),-1.0]])],"derivedFrom":subQ4})])]}),makeQuery(id+"F9.opExtrude","SWEPT_FACE",FACE,{"disambiguationData":[OSD([subQ2,subQ3,subQ1]),TDD([makeQuery(id+"F6.imprint","IMPRINT",EDGE,{"disambiguationData":[TD([[makeQuery(id+"F6.imprint","INTERSECT",VERTEX,{"derivedFrom":[subQ4,subQ9,sQuery(id+"F6.wireOp",EDGE,"E22")]}),1.0]])],"derivedFrom":subQ4})])]}),makeQuery(id+"F9.opExtrude","SWEPT_FACE",FACE,{"disambiguationData":[OSD([subQ2,subQ3,subQ1]),TDD([makeQuery(id+"F6.imprint","IMPRINT",EDGE,{"disambiguationData":[TD([[makeQuery(id+"F6.imprint","INTERSECT",VERTEX,{"derivedFrom":[subQ4,subQ7,subQ18]}),-1.0]])],"derivedFrom":subQ4})])]})])],"derivedFrom":makeQuery(id+"F4.boolean.opBoolean","MERGE",FACE,{"derivedFrom":[makeQuery(id+"F3.boolean.opBoolean","MERGE",FACE,{"derivedFrom":[makeQuery(id+"F2.boolean.opBoolean","MERGE",FACE,{"derivedFrom":[subQ20,subQ8]}),subQ17]}),subQ21]})});}
            extrude(context, id + "F12", {"entities" : qUnion([Q0, Q1, Q2, Q3, Q4, Q5]), "operationType" : NewBodyOperationType.REMOVE, "oppositeDirection" : true, "depth" : 6.35 * mm, "offsetDistance" : 25.4 * mm});
        }
        {
            var Q0;
            {var subQ0=sQuery(id+"F0.wireOp",EDGE,"E0.right");var subQ1=sQuery(id+"F5.wireOp",EDGE,"E14");var subQ2=sQuery(id+"F0.wireOp",EDGE,"E0.left");var subQ3=sQuery(id+"F0.wireOp",EDGE,"E0.bottom");var subQ4=makeQuery(id+"F3.opExtrude","SWEPT_FACE",FACE,{"disambiguationData":[OSD([subQ3,subQ2])]});var subQ5=sQuery(id+"F5.wireOp",EDGE,"E5");var subQ6=makeQuery(id+"F4.boolean.opBoolean","MERGE",EDGE,{"derivedFrom":[makeQuery(id+"F3.boolean.opBoolean","MERGE",EDGE,{"derivedFrom":[makeQuery(id+"F2.opExtrude","CAP_EDGE",EDGE,{"disambiguationData":[OSD([subQ3])],"isStart":false}),makeQuery(id+"F3.opExtrude","SWEPT_EDGE",EDGE,{"disambiguationData":[OSD([subQ3,subQ2]),TDD([makeQuery(id+"F2.opExtrude","CAP_VERTEX",VERTEX,{"disambiguationData":[OSD([subQ3,subQ2])],"isStart":false})])]})]}),makeQuery(id+"F4.opExtrude","SWEPT_EDGE",EDGE,{"disambiguationData":[OSD([subQ3,subQ0]),TDD([makeQuery(id+"F2.opExtrude","CAP_VERTEX",VERTEX,{"disambiguationData":[OSD([subQ3,subQ0])],"isStart":false})])]})]});var subQ7=sQuery(id+"F5.wireOp",EDGE,"E3");var subQ8=makeQuery(id+"F4.boolean.opBoolean","MERGE",EDGE,{"derivedFrom":[makeQuery(id+"F3.boolean.opBoolean","MERGE",EDGE,{"derivedFrom":[makeQuery(id+"F1.opExtrude","CAP_EDGE",EDGE,{"disambiguationData":[OSD([subQ3])],"isStart":false}),makeQuery(id+"F3.opExtrude","SWEPT_EDGE",EDGE,{"disambiguationData":[OSD([subQ3,subQ2]),TDD([makeQuery(id+"F1.opExtrude","CAP_VERTEX",VERTEX,{"disambiguationData":[OSD([subQ3,subQ2])],"isStart":false})])]})]}),makeQuery(id+"F4.opExtrude","SWEPT_EDGE",EDGE,{"disambiguationData":[OSD([subQ3,subQ0]),TDD([makeQuery(id+"F1.opExtrude","CAP_VERTEX",VERTEX,{"disambiguationData":[OSD([subQ3,subQ0])],"isStart":false})])]})]});var subQ9=sQuery(id+"F5.wireOp",EDGE,"E13");var subQ10=sQuery(id+"F5.wireOp",EDGE,"E8");var subQ11=makeQuery(id+"F1.opExtrude","SWEPT_FACE",FACE,{"disambiguationData":[OSD([subQ3])]});var subQ12=makeQuery(id+"F4.opExtrude","SWEPT_FACE",FACE,{"disambiguationData":[OSD([subQ3,subQ0])]});var subQ13=sQuery(id+"F0.wireOp",EDGE,"E0.top");var subQ14=sQuery(id+"F5.wireOp",EDGE,"E15");var subQ15=makeQuery(id+"F2.opExtrude","SWEPT_FACE",FACE,{"disambiguationData":[OSD([subQ3])]});Q0=makeQuery(id+"F11.boolean.opBoolean","COPY",FACE,{"derivedFrom":makeQuery(id+"F11.opExtrude","CAP_FACE",FACE,{"disambiguationData":[OSD([subQ3,subQ2,subQ0]),TDD([makeQuery(id+"F7.boolean.opBoolean","SPLIT",FACE,{"disambiguationData":[TD([subQ11,makeQuery(id+"F1.opExtrude","CAP_FACE",FACE,{"disambiguationData":[OSD([subQ3,subQ13,subQ2,subQ0])],"isStart":false}),subQ15,makeQuery(id+"F2.opExtrude","CAP_FACE",FACE,{"disambiguationData":[OSD([subQ3,subQ13,subQ2,subQ0])],"isStart":false}),makeQuery(id+"F3.opExtrude","SWEPT_FACE",FACE,{"disambiguationData":[OSD([subQ2]),TDD([makeQuery(id+"F1.opExtrude","CAP_EDGE",EDGE,{"disambiguationData":[OSD([subQ2])],"isStart":false})])]}),makeQuery(id+"F3.opExtrude","SWEPT_FACE",FACE,{"disambiguationData":[OSD([subQ2]),TDD([makeQuery(id+"F2.opExtrude","CAP_EDGE",EDGE,{"disambiguationData":[OSD([subQ2])],"isStart":false})])]}),subQ4,makeQuery(id+"F3.opExtrude","CAP_FACE",FACE,{"disambiguationData":[OSD([subQ2])],"isStart":false}),makeQuery(id+"F4.opExtrude","SWEPT_FACE",FACE,{"disambiguationData":[OSD([subQ0]),TDD([makeQuery(id+"F1.opExtrude","CAP_EDGE",EDGE,{"disambiguationData":[OSD([subQ0])],"isStart":false})])]}),makeQuery(id+"F4.opExtrude","SWEPT_FACE",FACE,{"disambiguationData":[OSD([subQ0]),TDD([makeQuery(id+"F2.opExtrude","CAP_EDGE",EDGE,{"disambiguationData":[OSD([subQ0])],"isStart":false})])]}),subQ12,makeQuery(id+"F7.opExtrude","SWEPT_FACE",FACE,{"disambiguationData":[OSD([subQ1])]}),makeQuery(id+"F7.opExtrude","SWEPT_FACE",FACE,{"disambiguationData":[OSD([subQ14])]}),makeQuery(id+"F7.opExtrude","SWEPT_FACE",FACE,{"disambiguationData":[OSD([subQ3,subQ2,subQ0]),TDD([makeQuery(id+"F5.imprint","IMPRINT",EDGE,{"disambiguationData":[TD([[makeQuery(id+"F5.imprint","INTERSECT",VERTEX,{"derivedFrom":[subQ8,subQ7,sQuery(id+"F5.wireOp",EDGE,"E4")]}),1.0]])],"derivedFrom":subQ8})])]}),makeQuery(id+"F7.opExtrude","SWEPT_FACE",FACE,{"disambiguationData":[OSD([subQ3,subQ2,subQ0]),TDD([makeQuery(id+"F5.imprint","IMPRINT",EDGE,{"disambiguationData":[TD([[makeQuery(id+"F5.imprint","INTERSECT",VERTEX,{"derivedFrom":[subQ8,subQ5,sQuery(id+"F5.wireOp",EDGE,"E6")]}),-1.0]])],"derivedFrom":subQ8})])]}),makeQuery(id+"F7.opExtrude","SWEPT_FACE",FACE,{"disambiguationData":[OSD([subQ3,subQ2,subQ0]),TDD([makeQuery(id+"F5.imprint","IMPRINT",EDGE,{"disambiguationData":[TD([[makeQuery(id+"F5.imprint","INTERSECT",VERTEX,{"derivedFrom":[subQ6,sQuery(id+"F5.wireOp",EDGE,"E1"),subQ5]}),1.0]])],"derivedFrom":subQ6})])]}),makeQuery(id+"F7.opExtrude","SWEPT_FACE",FACE,{"disambiguationData":[OSD([subQ3,subQ2,subQ0]),TDD([makeQuery(id+"F5.imprint","IMPRINT",EDGE,{"disambiguationData":[TD([[makeQuery(id+"F5.imprint","INTERSECT",VERTEX,{"derivedFrom":[subQ6,subQ10,sQuery(id+"F5.wireOp",EDGE,"E9")]}),-1.0]])],"derivedFrom":subQ6})])]}),makeQuery(id+"F7.opExtrude","SWEPT_FACE",FACE,{"disambiguationData":[OSD([subQ3,subQ2,subQ0]),TDD([makeQuery(id+"F5.imprint","IMPRINT",EDGE,{"disambiguationData":[TD([[makeQuery(id+"F5.imprint","INTERSECT",VERTEX,{"derivedFrom":[subQ6,subQ9,subQ1]}),1.0]])],"derivedFrom":subQ6})])]})])],"derivedFrom":makeQuery(id+"F4.boolean.opBoolean","MERGE",FACE,{"derivedFrom":[makeQuery(id+"F3.boolean.opBoolean","MERGE",FACE,{"derivedFrom":[makeQuery(id+"F2.boolean.opBoolean","MERGE",FACE,{"derivedFrom":[subQ11,subQ15]}),subQ4]}),subQ12]})})])],"isStart":false})});}
            extrude(context, id + "F13", {"entities" : qUnion([Q0]), "operationType" : NewBodyOperationType.REMOVE, "oppositeDirection" : true, "depth" : 76.2 * mm, "offsetDistance" : 25.4 * mm});
        }
        {
            var Q0;
            {var subQ0=sQuery(id+"F0.wireOp",EDGE,"E0.right");var subQ1=sQuery(id+"F0.wireOp",EDGE,"E0.left");var subQ2=sQuery(id+"F0.wireOp",EDGE,"E0.bottom");var subQ3=makeQuery(id+"F3.opExtrude","SWEPT_FACE",FACE,{"disambiguationData":[OSD([subQ2,subQ1])]});var subQ4=sQuery(id+"F5.wireOp",EDGE,"E5");var subQ5=makeQuery(id+"F4.boolean.opBoolean","MERGE",EDGE,{"derivedFrom":[makeQuery(id+"F3.boolean.opBoolean","MERGE",EDGE,{"derivedFrom":[makeQuery(id+"F2.opExtrude","CAP_EDGE",EDGE,{"disambiguationData":[OSD([subQ2])],"isStart":false}),makeQuery(id+"F3.opExtrude","SWEPT_EDGE",EDGE,{"disambiguationData":[OSD([subQ2,subQ1]),TDD([makeQuery(id+"F2.opExtrude","CAP_VERTEX",VERTEX,{"disambiguationData":[OSD([subQ2,subQ1])],"isStart":false})])]})]}),makeQuery(id+"F4.opExtrude","SWEPT_EDGE",EDGE,{"disambiguationData":[OSD([subQ2,subQ0]),TDD([makeQuery(id+"F2.opExtrude","CAP_VERTEX",VERTEX,{"disambiguationData":[OSD([subQ2,subQ0])],"isStart":false})])]})]});var subQ6=sQuery(id+"F5.wireOp",EDGE,"E3");var subQ7=makeQuery(id+"F4.boolean.opBoolean","MERGE",EDGE,{"derivedFrom":[makeQuery(id+"F3.boolean.opBoolean","MERGE",EDGE,{"derivedFrom":[makeQuery(id+"F1.opExtrude","CAP_EDGE",EDGE,{"disambiguationData":[OSD([subQ2])],"isStart":false}),makeQuery(id+"F3.opExtrude","SWEPT_EDGE",EDGE,{"disambiguationData":[OSD([subQ2,subQ1]),TDD([makeQuery(id+"F1.opExtrude","CAP_VERTEX",VERTEX,{"disambiguationData":[OSD([subQ2,subQ1])],"isStart":false})])]})]}),makeQuery(id+"F4.opExtrude","SWEPT_EDGE",EDGE,{"disambiguationData":[OSD([subQ2,subQ0]),TDD([makeQuery(id+"F1.opExtrude","CAP_VERTEX",VERTEX,{"disambiguationData":[OSD([subQ2,subQ0])],"isStart":false})])]})]});var subQ8=sQuery(id+"F5.wireOp",EDGE,"E13");var subQ9=sQuery(id+"F5.wireOp",EDGE,"E8");var subQ10=makeQuery(id+"F1.opExtrude","SWEPT_FACE",FACE,{"disambiguationData":[OSD([subQ2])]});var subQ11=makeQuery(id+"F4.opExtrude","SWEPT_FACE",FACE,{"disambiguationData":[OSD([subQ2,subQ0])]});var subQ12=sQuery(id+"F0.wireOp",EDGE,"E0.top");var subQ13=makeQuery(id+"F2.opExtrude","SWEPT_FACE",FACE,{"disambiguationData":[OSD([subQ2])]});var subQ14=sQuery(id+"F5.wireOp",EDGE,"E9");var subQ15=sQuery(id+"F5.wireOp",EDGE,"E10");Q0=makeQuery(id+"F11.boolean.opBoolean","COPY",FACE,{"derivedFrom":makeQuery(id+"F11.opExtrude","CAP_FACE",FACE,{"disambiguationData":[OSD([subQ2,subQ1,subQ0]),TDD([makeQuery(id+"F7.boolean.opBoolean","SPLIT",FACE,{"disambiguationData":[TD([subQ10,makeQuery(id+"F1.opExtrude","CAP_FACE",FACE,{"disambiguationData":[OSD([subQ2,subQ12,subQ1,subQ0])],"isStart":false}),subQ13,makeQuery(id+"F2.opExtrude","CAP_FACE",FACE,{"disambiguationData":[OSD([subQ2,subQ12,subQ1,subQ0])],"isStart":false}),makeQuery(id+"F3.opExtrude","SWEPT_FACE",FACE,{"disambiguationData":[OSD([subQ1]),TDD([makeQuery(id+"F1.opExtrude","CAP_EDGE",EDGE,{"disambiguationData":[OSD([subQ1])],"isStart":false})])]}),makeQuery(id+"F3.opExtrude","SWEPT_FACE",FACE,{"disambiguationData":[OSD([subQ1]),TDD([makeQuery(id+"F2.opExtrude","CAP_EDGE",EDGE,{"disambiguationData":[OSD([subQ1])],"isStart":false})])]}),subQ3,makeQuery(id+"F4.opExtrude","SWEPT_FACE",FACE,{"disambiguationData":[OSD([subQ0]),TDD([makeQuery(id+"F1.opExtrude","CAP_EDGE",EDGE,{"disambiguationData":[OSD([subQ0])],"isStart":false})])]}),makeQuery(id+"F4.opExtrude","SWEPT_FACE",FACE,{"disambiguationData":[OSD([subQ0]),TDD([makeQuery(id+"F2.opExtrude","CAP_EDGE",EDGE,{"disambiguationData":[OSD([subQ0])],"isStart":false})])]}),subQ11,makeQuery(id+"F4.opExtrude","CAP_FACE",FACE,{"disambiguationData":[OSD([subQ0])],"isStart":false}),makeQuery(id+"F7.opExtrude","SWEPT_FACE",FACE,{"disambiguationData":[OSD([subQ14])]}),makeQuery(id+"F7.opExtrude","SWEPT_FACE",FACE,{"disambiguationData":[OSD([subQ15])]}),makeQuery(id+"F7.opExtrude","SWEPT_FACE",FACE,{"disambiguationData":[OSD([subQ2,subQ1,subQ0]),TDD([makeQuery(id+"F5.imprint","IMPRINT",EDGE,{"disambiguationData":[TD([[makeQuery(id+"F5.imprint","INTERSECT",VERTEX,{"derivedFrom":[subQ7,subQ6,sQuery(id+"F5.wireOp",EDGE,"E4")]}),1.0]])],"derivedFrom":subQ7})])]}),makeQuery(id+"F7.opExtrude","SWEPT_FACE",FACE,{"disambiguationData":[OSD([subQ2,subQ1,subQ0]),TDD([makeQuery(id+"F5.imprint","IMPRINT",EDGE,{"disambiguationData":[TD([[makeQuery(id+"F5.imprint","INTERSECT",VERTEX,{"derivedFrom":[subQ7,subQ4,sQuery(id+"F5.wireOp",EDGE,"E6")]}),-1.0]])],"derivedFrom":subQ7})])]}),makeQuery(id+"F7.opExtrude","SWEPT_FACE",FACE,{"disambiguationData":[OSD([subQ2,subQ1,subQ0]),TDD([makeQuery(id+"F5.imprint","IMPRINT",EDGE,{"disambiguationData":[TD([[makeQuery(id+"F5.imprint","INTERSECT",VERTEX,{"derivedFrom":[subQ5,sQuery(id+"F5.wireOp",EDGE,"E1"),subQ4]}),1.0]])],"derivedFrom":subQ5})])]}),makeQuery(id+"F7.opExtrude","SWEPT_FACE",FACE,{"disambiguationData":[OSD([subQ2,subQ1,subQ0]),TDD([makeQuery(id+"F5.imprint","IMPRINT",EDGE,{"disambiguationData":[TD([[makeQuery(id+"F5.imprint","INTERSECT",VERTEX,{"derivedFrom":[subQ5,subQ9,subQ14]}),-1.0]])],"derivedFrom":subQ5})])]}),makeQuery(id+"F7.opExtrude","SWEPT_FACE",FACE,{"disambiguationData":[OSD([subQ2,subQ1,subQ0]),TDD([makeQuery(id+"F5.imprint","IMPRINT",EDGE,{"disambiguationData":[TD([[makeQuery(id+"F5.imprint","INTERSECT",VERTEX,{"derivedFrom":[subQ5,subQ8,sQuery(id+"F5.wireOp",EDGE,"E14")]}),1.0]])],"derivedFrom":subQ5})])]})])],"derivedFrom":makeQuery(id+"F4.boolean.opBoolean","MERGE",FACE,{"derivedFrom":[makeQuery(id+"F3.boolean.opBoolean","MERGE",FACE,{"derivedFrom":[makeQuery(id+"F2.boolean.opBoolean","MERGE",FACE,{"derivedFrom":[subQ10,subQ13]}),subQ3]}),subQ11]})})])],"isStart":false})});}
            extrude(context, id + "F14", {"entities" : qUnion([Q0]), "operationType" : NewBodyOperationType.REMOVE, "oppositeDirection" : true, "depth" : 76.2 * mm, "offsetDistance" : 25.4 * mm});
        }
        {
            var Q0;
            {var subQ0=sQuery(id+"F0.wireOp",EDGE,"E0.right");var subQ1=sQuery(id+"F0.wireOp",EDGE,"E0.top");var subQ2=sQuery(id+"F0.wireOp",EDGE,"E0.left");var subQ3=makeQuery(id+"F4.boolean.opBoolean","MERGE",EDGE,{"derivedFrom":[makeQuery(id+"F3.boolean.opBoolean","MERGE",EDGE,{"derivedFrom":[makeQuery(id+"F2.opExtrude","CAP_EDGE",EDGE,{"disambiguationData":[OSD([subQ1])],"isStart":false}),makeQuery(id+"F3.opExtrude","SWEPT_EDGE",EDGE,{"disambiguationData":[OSD([subQ1,subQ2]),TDD([makeQuery(id+"F2.opExtrude","CAP_VERTEX",VERTEX,{"disambiguationData":[OSD([subQ1,subQ2])],"isStart":false})])]})]}),makeQuery(id+"F4.opExtrude","SWEPT_EDGE",EDGE,{"disambiguationData":[OSD([subQ1,subQ0]),TDD([makeQuery(id+"F2.opExtrude","CAP_VERTEX",VERTEX,{"disambiguationData":[OSD([subQ1,subQ0])],"isStart":false})])]})]});var subQ4=sQuery(id+"F0.wireOp",EDGE,"E0.bottom");var subQ5=makeQuery(id+"F4.boolean.opBoolean","MERGE",EDGE,{"derivedFrom":[makeQuery(id+"F3.boolean.opBoolean","MERGE",EDGE,{"derivedFrom":[makeQuery(id+"F2.opExtrude","CAP_EDGE",EDGE,{"disambiguationData":[OSD([subQ4])],"isStart":false}),makeQuery(id+"F3.opExtrude","SWEPT_EDGE",EDGE,{"disambiguationData":[OSD([subQ4,subQ2]),TDD([makeQuery(id+"F2.opExtrude","CAP_VERTEX",VERTEX,{"disambiguationData":[OSD([subQ4,subQ2])],"isStart":false})])]})]}),makeQuery(id+"F4.opExtrude","SWEPT_EDGE",EDGE,{"disambiguationData":[OSD([subQ4,subQ0]),TDD([makeQuery(id+"F2.opExtrude","CAP_VERTEX",VERTEX,{"disambiguationData":[OSD([subQ4,subQ0])],"isStart":false})])]})]});Q0=makeQuery(id+"F9.boolean.opBoolean","MERGE",FACE,{"derivedFrom":[makeQuery(id+"F7.boolean.opBoolean","MERGE",FACE,{"derivedFrom":[makeQuery(id+"F4.boolean.opBoolean","MERGE",FACE,{"derivedFrom":[makeQuery(id+"F3.boolean.opBoolean","MERGE",FACE,{"derivedFrom":[makeQuery(id+"F2.opExtrude","CAP_FACE",FACE,{"disambiguationData":[OSD([subQ4,subQ1,subQ2,subQ0])],"isStart":false}),makeQuery(id+"F3.opExtrude","SWEPT_FACE",FACE,{"disambiguationData":[OSD([subQ2]),TDD([makeQuery(id+"F2.opExtrude","CAP_EDGE",EDGE,{"disambiguationData":[OSD([subQ2])],"isStart":false})])]})]}),makeQuery(id+"F4.opExtrude","SWEPT_FACE",FACE,{"disambiguationData":[OSD([subQ0]),TDD([makeQuery(id+"F2.opExtrude","CAP_EDGE",EDGE,{"disambiguationData":[OSD([subQ0])],"isStart":false})])]})]}),makeQuery(id+"F7.opExtrude","SWEPT_FACE",FACE,{"disambiguationData":[OSD([subQ4,subQ2,subQ0]),TDD([makeQuery(id+"F5.imprint","IMPRINT",EDGE,{"disambiguationData":[TD([[makeQuery(id+"F5.imprint","INTERSECT",VERTEX,{"derivedFrom":[subQ5,sQuery(id+"F5.wireOp",EDGE,"E1"),sQuery(id+"F5.wireOp",EDGE,"E5")]}),1.0]])],"derivedFrom":subQ5})])]}),makeQuery(id+"F7.opExtrude","SWEPT_FACE",FACE,{"disambiguationData":[OSD([subQ4,subQ2,subQ0]),TDD([makeQuery(id+"F5.imprint","IMPRINT",EDGE,{"disambiguationData":[TD([[makeQuery(id+"F5.imprint","INTERSECT",VERTEX,{"derivedFrom":[subQ5,sQuery(id+"F5.wireOp",EDGE,"E8"),sQuery(id+"F5.wireOp",EDGE,"E9")]}),-1.0]])],"derivedFrom":subQ5})])]}),makeQuery(id+"F7.opExtrude","SWEPT_FACE",FACE,{"disambiguationData":[OSD([subQ4,subQ2,subQ0]),TDD([makeQuery(id+"F5.imprint","IMPRINT",EDGE,{"disambiguationData":[TD([[makeQuery(id+"F5.imprint","INTERSECT",VERTEX,{"derivedFrom":[subQ5,sQuery(id+"F5.wireOp",EDGE,"E13"),sQuery(id+"F5.wireOp",EDGE,"E14")]}),1.0]])],"derivedFrom":subQ5})])]})]}),makeQuery(id+"F9.opExtrude","SWEPT_FACE",FACE,{"disambiguationData":[OSD([subQ1,subQ2,subQ0]),TDD([makeQuery(id+"F6.imprint","IMPRINT",EDGE,{"disambiguationData":[TD([[makeQuery(id+"F6.imprint","INTERSECT",VERTEX,{"derivedFrom":[subQ3,sQuery(id+"F6.wireOp",EDGE,"E17"),sQuery(id+"F6.wireOp",EDGE,"E18")]}),-1.0]])],"derivedFrom":subQ3})])]}),makeQuery(id+"F9.opExtrude","SWEPT_FACE",FACE,{"disambiguationData":[OSD([subQ1,subQ2,subQ0]),TDD([makeQuery(id+"F6.imprint","IMPRINT",EDGE,{"disambiguationData":[TD([[makeQuery(id+"F6.imprint","INTERSECT",VERTEX,{"derivedFrom":[subQ3,sQuery(id+"F6.wireOp",EDGE,"E21"),sQuery(id+"F6.wireOp",EDGE,"E22")]}),1.0]])],"derivedFrom":subQ3})])]}),makeQuery(id+"F9.opExtrude","SWEPT_FACE",FACE,{"disambiguationData":[OSD([subQ1,subQ2,subQ0]),TDD([makeQuery(id+"F6.imprint","IMPRINT",EDGE,{"disambiguationData":[TD([[makeQuery(id+"F6.imprint","INTERSECT",VERTEX,{"derivedFrom":[subQ3,sQuery(id+"F6.wireOp",EDGE,"E29"),sQuery(id+"F6.wireOp",EDGE,"E30")]}),-1.0]])],"derivedFrom":subQ3})])]})]});}
            extrude(context, id + "F15", {"entities" : qUnion([Q0]), "operationType" : NewBodyOperationType.REMOVE, "oppositeDirection" : true, "depth" : 2.54 * mm, "offsetDistance" : 25.4 * mm});
        }
        {
            var Q0;
            {var subQ0=sQuery(id+"F0.wireOp",EDGE,"E0.right");var subQ1=sQuery(id+"F0.wireOp",EDGE,"E0.bottom");var subQ2=makeQuery(id+"F2.opExtrude","SWEPT_FACE",FACE,{"disambiguationData":[OSD([subQ1])]});var subQ3=sQuery(id+"F5.wireOp",EDGE,"E14");var subQ4=sQuery(id+"F0.wireOp",EDGE,"E0.left");var subQ5=makeQuery(id+"F3.opExtrude","SWEPT_FACE",FACE,{"disambiguationData":[OSD([subQ1,subQ4])]});var subQ6=sQuery(id+"F5.wireOp",EDGE,"E5");var subQ7=makeQuery(id+"F4.boolean.opBoolean","MERGE",EDGE,{"derivedFrom":[makeQuery(id+"F3.boolean.opBoolean","MERGE",EDGE,{"derivedFrom":[makeQuery(id+"F2.opExtrude","CAP_EDGE",EDGE,{"disambiguationData":[OSD([subQ1])],"isStart":false}),makeQuery(id+"F3.opExtrude","SWEPT_EDGE",EDGE,{"disambiguationData":[OSD([subQ1,subQ4]),TDD([makeQuery(id+"F2.opExtrude","CAP_VERTEX",VERTEX,{"disambiguationData":[OSD([subQ1,subQ4])],"isStart":false})])]})]}),makeQuery(id+"F4.opExtrude","SWEPT_EDGE",EDGE,{"disambiguationData":[OSD([subQ1,subQ0]),TDD([makeQuery(id+"F2.opExtrude","CAP_VERTEX",VERTEX,{"disambiguationData":[OSD([subQ1,subQ0])],"isStart":false})])]})]});var subQ8=sQuery(id+"F5.wireOp",EDGE,"E3");var subQ9=sQuery(id+"F0.wireOp",EDGE,"E0.top");var subQ10=makeQuery(id+"F4.boolean.opBoolean","MERGE",EDGE,{"derivedFrom":[makeQuery(id+"F3.boolean.opBoolean","MERGE",EDGE,{"derivedFrom":[makeQuery(id+"F1.opExtrude","CAP_EDGE",EDGE,{"disambiguationData":[OSD([subQ1])],"isStart":false}),makeQuery(id+"F3.opExtrude","SWEPT_EDGE",EDGE,{"disambiguationData":[OSD([subQ1,subQ4]),TDD([makeQuery(id+"F1.opExtrude","CAP_VERTEX",VERTEX,{"disambiguationData":[OSD([subQ1,subQ4])],"isStart":false})])]})]}),makeQuery(id+"F4.opExtrude","SWEPT_EDGE",EDGE,{"disambiguationData":[OSD([subQ1,subQ0]),TDD([makeQuery(id+"F1.opExtrude","CAP_VERTEX",VERTEX,{"disambiguationData":[OSD([subQ1,subQ0])],"isStart":false})])]})]});var subQ11=sQuery(id+"F5.wireOp",EDGE,"E8");var subQ12=sQuery(id+"F5.wireOp",EDGE,"E4");var subQ13=sQuery(id+"F5.wireOp",EDGE,"E13");var subQ14=sQuery(id+"F5.wireOp",EDGE,"E12");var subQ15=makeQuery(id+"F1.opExtrude","SWEPT_FACE",FACE,{"disambiguationData":[OSD([subQ1])]});var subQ16=makeQuery(id+"F4.opExtrude","SWEPT_FACE",FACE,{"disambiguationData":[OSD([subQ1,subQ0])]});var subQ17=sQuery(id+"F5.wireOp",EDGE,"E15");Q0=makeQuery(id+"F11.boolean.opBoolean","COPY",FACE,{"derivedFrom":makeQuery(id+"F11.opExtrude","CAP_FACE",FACE,{"disambiguationData":[OSD([subQ1,subQ4,subQ0]),TDD([makeQuery(id+"F7.boolean.opBoolean","SPLIT",FACE,{"disambiguationData":[TD([subQ15,makeQuery(id+"F1.opExtrude","CAP_FACE",FACE,{"disambiguationData":[OSD([subQ1,subQ9,subQ4,subQ0])],"isStart":false}),subQ2,makeQuery(id+"F2.opExtrude","CAP_FACE",FACE,{"disambiguationData":[OSD([subQ1,subQ9,subQ4,subQ0])],"isStart":false}),makeQuery(id+"F3.opExtrude","SWEPT_FACE",FACE,{"disambiguationData":[OSD([subQ4]),TDD([makeQuery(id+"F1.opExtrude","CAP_EDGE",EDGE,{"disambiguationData":[OSD([subQ4])],"isStart":false})])]}),makeQuery(id+"F3.opExtrude","SWEPT_FACE",FACE,{"disambiguationData":[OSD([subQ4]),TDD([makeQuery(id+"F2.opExtrude","CAP_EDGE",EDGE,{"disambiguationData":[OSD([subQ4])],"isStart":false})])]}),subQ5,makeQuery(id+"F4.opExtrude","SWEPT_FACE",FACE,{"disambiguationData":[OSD([subQ0]),TDD([makeQuery(id+"F1.opExtrude","CAP_EDGE",EDGE,{"disambiguationData":[OSD([subQ0])],"isStart":false})])]}),makeQuery(id+"F4.opExtrude","SWEPT_FACE",FACE,{"disambiguationData":[OSD([subQ0]),TDD([makeQuery(id+"F2.opExtrude","CAP_EDGE",EDGE,{"disambiguationData":[OSD([subQ0])],"isStart":false})])]}),subQ16,makeQuery(id+"F7.opExtrude","SWEPT_FACE",FACE,{"disambiguationData":[OSD([subQ12])]}),makeQuery(id+"F7.opExtrude","SWEPT_FACE",FACE,{"disambiguationData":[OSD([subQ14])]}),makeQuery(id+"F7.opExtrude","SWEPT_FACE",FACE,{"disambiguationData":[OSD([subQ3])]}),makeQuery(id+"F7.opExtrude","SWEPT_FACE",FACE,{"disambiguationData":[OSD([subQ17])]}),makeQuery(id+"F7.opExtrude","SWEPT_FACE",FACE,{"disambiguationData":[OSD([subQ1,subQ4,subQ0]),TDD([makeQuery(id+"F5.imprint","IMPRINT",EDGE,{"disambiguationData":[TD([[makeQuery(id+"F5.imprint","INTERSECT",VERTEX,{"derivedFrom":[subQ10,subQ8,subQ12]}),1.0]])],"derivedFrom":subQ10})])]}),makeQuery(id+"F7.opExtrude","SWEPT_FACE",FACE,{"disambiguationData":[OSD([subQ1,subQ4,subQ0]),TDD([makeQuery(id+"F5.imprint","IMPRINT",EDGE,{"disambiguationData":[TD([[makeQuery(id+"F5.imprint","INTERSECT",VERTEX,{"derivedFrom":[subQ10,subQ6,sQuery(id+"F5.wireOp",EDGE,"E6")]}),-1.0]])],"derivedFrom":subQ10})])]}),makeQuery(id+"F7.opExtrude","SWEPT_FACE",FACE,{"disambiguationData":[OSD([subQ1,subQ4,subQ0]),TDD([makeQuery(id+"F5.imprint","IMPRINT",EDGE,{"disambiguationData":[TD([[makeQuery(id+"F5.imprint","INTERSECT",VERTEX,{"derivedFrom":[subQ7,sQuery(id+"F5.wireOp",EDGE,"E1"),subQ6]}),1.0]])],"derivedFrom":subQ7})])]}),makeQuery(id+"F7.opExtrude","SWEPT_FACE",FACE,{"disambiguationData":[OSD([subQ1,subQ4,subQ0]),TDD([makeQuery(id+"F5.imprint","IMPRINT",EDGE,{"disambiguationData":[TD([[makeQuery(id+"F5.imprint","INTERSECT",VERTEX,{"derivedFrom":[subQ7,subQ11,sQuery(id+"F5.wireOp",EDGE,"E9")]}),-1.0]])],"derivedFrom":subQ7})])]}),makeQuery(id+"F7.opExtrude","SWEPT_FACE",FACE,{"disambiguationData":[OSD([subQ1,subQ4,subQ0]),TDD([makeQuery(id+"F5.imprint","IMPRINT",EDGE,{"disambiguationData":[TD([[makeQuery(id+"F5.imprint","INTERSECT",VERTEX,{"derivedFrom":[subQ7,subQ13,subQ3]}),1.0]])],"derivedFrom":subQ7})])]})])],"derivedFrom":makeQuery(id+"F4.boolean.opBoolean","MERGE",FACE,{"derivedFrom":[makeQuery(id+"F3.boolean.opBoolean","MERGE",FACE,{"derivedFrom":[makeQuery(id+"F2.boolean.opBoolean","MERGE",FACE,{"derivedFrom":[subQ15,subQ2]}),subQ5]}),subQ16]})})])],"isStart":false})});}
            extrude(context, id + "F16", {"entities" : qUnion([Q0]), "operationType" : NewBodyOperationType.REMOVE, "oppositeDirection" : true, "depth" : 25.4 * mm, "offsetDistance" : 25.4 * mm});
        }
        {
            var Q0;
            {var subQ0=sQuery(id+"F0.wireOp",EDGE,"E0.right");var subQ1=sQuery(id+"F0.wireOp",EDGE,"E0.bottom");var subQ2=makeQuery(id+"F2.opExtrude","SWEPT_FACE",FACE,{"disambiguationData":[OSD([subQ1])]});var subQ3=sQuery(id+"F0.wireOp",EDGE,"E0.left");var subQ4=makeQuery(id+"F3.opExtrude","SWEPT_FACE",FACE,{"disambiguationData":[OSD([subQ1,subQ3])]});var subQ5=sQuery(id+"F5.wireOp",EDGE,"E5");var subQ6=sQuery(id+"F5.wireOp",EDGE,"E1");var subQ7=makeQuery(id+"F4.boolean.opBoolean","MERGE",EDGE,{"derivedFrom":[makeQuery(id+"F3.boolean.opBoolean","MERGE",EDGE,{"derivedFrom":[makeQuery(id+"F2.opExtrude","CAP_EDGE",EDGE,{"disambiguationData":[OSD([subQ1])],"isStart":false}),makeQuery(id+"F3.opExtrude","SWEPT_EDGE",EDGE,{"disambiguationData":[OSD([subQ1,subQ3]),TDD([makeQuery(id+"F2.opExtrude","CAP_VERTEX",VERTEX,{"disambiguationData":[OSD([subQ1,subQ3])],"isStart":false})])]})]}),makeQuery(id+"F4.opExtrude","SWEPT_EDGE",EDGE,{"disambiguationData":[OSD([subQ1,subQ0]),TDD([makeQuery(id+"F2.opExtrude","CAP_VERTEX",VERTEX,{"disambiguationData":[OSD([subQ1,subQ0])],"isStart":false})])]})]});var subQ8=sQuery(id+"F5.wireOp",EDGE,"E3");var subQ9=sQuery(id+"F5.wireOp",EDGE,"E2");var subQ10=sQuery(id+"F0.wireOp",EDGE,"E0.top");var subQ11=makeQuery(id+"F4.boolean.opBoolean","MERGE",EDGE,{"derivedFrom":[makeQuery(id+"F3.boolean.opBoolean","MERGE",EDGE,{"derivedFrom":[makeQuery(id+"F1.opExtrude","CAP_EDGE",EDGE,{"disambiguationData":[OSD([subQ1])],"isStart":false}),makeQuery(id+"F3.opExtrude","SWEPT_EDGE",EDGE,{"disambiguationData":[OSD([subQ1,subQ3]),TDD([makeQuery(id+"F1.opExtrude","CAP_VERTEX",VERTEX,{"disambiguationData":[OSD([subQ1,subQ3])],"isStart":false})])]})]}),makeQuery(id+"F4.opExtrude","SWEPT_EDGE",EDGE,{"disambiguationData":[OSD([subQ1,subQ0]),TDD([makeQuery(id+"F1.opExtrude","CAP_VERTEX",VERTEX,{"disambiguationData":[OSD([subQ1,subQ0])],"isStart":false})])]})]});var subQ12=sQuery(id+"F5.wireOp",EDGE,"E8");var subQ13=sQuery(id+"F5.wireOp",EDGE,"E4");var subQ14=sQuery(id+"F5.wireOp",EDGE,"E13");var subQ15=sQuery(id+"F5.wireOp",EDGE,"E12");var subQ16=makeQuery(id+"F1.opExtrude","SWEPT_FACE",FACE,{"disambiguationData":[OSD([subQ1])]});var subQ17=makeQuery(id+"F4.opExtrude","SWEPT_FACE",FACE,{"disambiguationData":[OSD([subQ1,subQ0])]});Q0=makeQuery(id+"F11.boolean.opBoolean","COPY",FACE,{"derivedFrom":makeQuery(id+"F11.opExtrude","CAP_FACE",FACE,{"disambiguationData":[OSD([subQ1,subQ3,subQ0]),TDD([makeQuery(id+"F7.boolean.opBoolean","SPLIT",FACE,{"disambiguationData":[TD([subQ16,makeQuery(id+"F1.opExtrude","CAP_FACE",FACE,{"disambiguationData":[OSD([subQ1,subQ10,subQ3,subQ0])],"isStart":false}),subQ2,makeQuery(id+"F2.opExtrude","CAP_FACE",FACE,{"disambiguationData":[OSD([subQ1,subQ10,subQ3,subQ0])],"isStart":false}),makeQuery(id+"F3.opExtrude","SWEPT_FACE",FACE,{"disambiguationData":[OSD([subQ3]),TDD([makeQuery(id+"F1.opExtrude","CAP_EDGE",EDGE,{"disambiguationData":[OSD([subQ3])],"isStart":false})])]}),makeQuery(id+"F3.opExtrude","SWEPT_FACE",FACE,{"disambiguationData":[OSD([subQ3]),TDD([makeQuery(id+"F2.opExtrude","CAP_EDGE",EDGE,{"disambiguationData":[OSD([subQ3])],"isStart":false})])]}),subQ4,makeQuery(id+"F4.opExtrude","SWEPT_FACE",FACE,{"disambiguationData":[OSD([subQ0]),TDD([makeQuery(id+"F1.opExtrude","CAP_EDGE",EDGE,{"disambiguationData":[OSD([subQ0])],"isStart":false})])]}),makeQuery(id+"F4.opExtrude","SWEPT_FACE",FACE,{"disambiguationData":[OSD([subQ0]),TDD([makeQuery(id+"F2.opExtrude","CAP_EDGE",EDGE,{"disambiguationData":[OSD([subQ0])],"isStart":false})])]}),subQ17,makeQuery(id+"F7.opExtrude","SWEPT_FACE",FACE,{"disambiguationData":[OSD([subQ6])]}),makeQuery(id+"F7.opExtrude","SWEPT_FACE",FACE,{"disambiguationData":[OSD([subQ9])]}),makeQuery(id+"F7.opExtrude","SWEPT_FACE",FACE,{"disambiguationData":[OSD([subQ13])]}),makeQuery(id+"F7.opExtrude","SWEPT_FACE",FACE,{"disambiguationData":[OSD([subQ15])]}),makeQuery(id+"F7.opExtrude","SWEPT_FACE",FACE,{"disambiguationData":[OSD([subQ1,subQ3,subQ0]),TDD([makeQuery(id+"F5.imprint","IMPRINT",EDGE,{"disambiguationData":[TD([[makeQuery(id+"F5.imprint","INTERSECT",VERTEX,{"derivedFrom":[subQ11,subQ8,subQ13]}),1.0]])],"derivedFrom":subQ11})])]}),makeQuery(id+"F7.opExtrude","SWEPT_FACE",FACE,{"disambiguationData":[OSD([subQ1,subQ3,subQ0]),TDD([makeQuery(id+"F5.imprint","IMPRINT",EDGE,{"disambiguationData":[TD([[makeQuery(id+"F5.imprint","INTERSECT",VERTEX,{"derivedFrom":[subQ11,subQ5,sQuery(id+"F5.wireOp",EDGE,"E6")]}),-1.0]])],"derivedFrom":subQ11})])]}),makeQuery(id+"F7.opExtrude","SWEPT_FACE",FACE,{"disambiguationData":[OSD([subQ1,subQ3,subQ0]),TDD([makeQuery(id+"F5.imprint","IMPRINT",EDGE,{"disambiguationData":[TD([[makeQuery(id+"F5.imprint","INTERSECT",VERTEX,{"derivedFrom":[subQ7,subQ6,subQ5]}),1.0]])],"derivedFrom":subQ7})])]}),makeQuery(id+"F7.opExtrude","SWEPT_FACE",FACE,{"disambiguationData":[OSD([subQ1,subQ3,subQ0]),TDD([makeQuery(id+"F5.imprint","IMPRINT",EDGE,{"disambiguationData":[TD([[makeQuery(id+"F5.imprint","INTERSECT",VERTEX,{"derivedFrom":[subQ7,subQ12,sQuery(id+"F5.wireOp",EDGE,"E9")]}),-1.0]])],"derivedFrom":subQ7})])]}),makeQuery(id+"F7.opExtrude","SWEPT_FACE",FACE,{"disambiguationData":[OSD([subQ1,subQ3,subQ0]),TDD([makeQuery(id+"F5.imprint","IMPRINT",EDGE,{"disambiguationData":[TD([[makeQuery(id+"F5.imprint","INTERSECT",VERTEX,{"derivedFrom":[subQ7,subQ14,sQuery(id+"F5.wireOp",EDGE,"E14")]}),1.0]])],"derivedFrom":subQ7})])]})])],"derivedFrom":makeQuery(id+"F4.boolean.opBoolean","MERGE",FACE,{"derivedFrom":[makeQuery(id+"F3.boolean.opBoolean","MERGE",FACE,{"derivedFrom":[makeQuery(id+"F2.boolean.opBoolean","MERGE",FACE,{"derivedFrom":[subQ16,subQ2]}),subQ4]}),subQ17]})})])],"isStart":false})});}
            extrude(context, id + "F17", {"entities" : qUnion([Q0]), "operationType" : NewBodyOperationType.REMOVE, "oppositeDirection" : true, "depth" : 25.4 * mm, "offsetDistance" : 25.4 * mm});
        }
        {
            var Q0;
            {var subQ0=sQuery(id+"F0.wireOp",EDGE,"E0.right");var subQ1=sQuery(id+"F0.wireOp",EDGE,"E0.bottom");var subQ2=makeQuery(id+"F2.opExtrude","SWEPT_FACE",FACE,{"disambiguationData":[OSD([subQ1])]});var subQ3=sQuery(id+"F0.wireOp",EDGE,"E0.left");var subQ4=makeQuery(id+"F3.opExtrude","SWEPT_FACE",FACE,{"disambiguationData":[OSD([subQ1,subQ3])]});var subQ5=sQuery(id+"F5.wireOp",EDGE,"E5");var subQ6=sQuery(id+"F5.wireOp",EDGE,"E1");var subQ7=makeQuery(id+"F4.boolean.opBoolean","MERGE",EDGE,{"derivedFrom":[makeQuery(id+"F3.boolean.opBoolean","MERGE",EDGE,{"derivedFrom":[makeQuery(id+"F2.opExtrude","CAP_EDGE",EDGE,{"disambiguationData":[OSD([subQ1])],"isStart":false}),makeQuery(id+"F3.opExtrude","SWEPT_EDGE",EDGE,{"disambiguationData":[OSD([subQ1,subQ3]),TDD([makeQuery(id+"F2.opExtrude","CAP_VERTEX",VERTEX,{"disambiguationData":[OSD([subQ1,subQ3])],"isStart":false})])]})]}),makeQuery(id+"F4.opExtrude","SWEPT_EDGE",EDGE,{"disambiguationData":[OSD([subQ1,subQ0]),TDD([makeQuery(id+"F2.opExtrude","CAP_VERTEX",VERTEX,{"disambiguationData":[OSD([subQ1,subQ0])],"isStart":false})])]})]});var subQ8=sQuery(id+"F5.wireOp",EDGE,"E3");var subQ9=sQuery(id+"F5.wireOp",EDGE,"E2");var subQ10=sQuery(id+"F0.wireOp",EDGE,"E0.top");var subQ11=sQuery(id+"F5.wireOp",EDGE,"E6");var subQ12=makeQuery(id+"F4.boolean.opBoolean","MERGE",EDGE,{"derivedFrom":[makeQuery(id+"F3.boolean.opBoolean","MERGE",EDGE,{"derivedFrom":[makeQuery(id+"F1.opExtrude","CAP_EDGE",EDGE,{"disambiguationData":[OSD([subQ1])],"isStart":false}),makeQuery(id+"F3.opExtrude","SWEPT_EDGE",EDGE,{"disambiguationData":[OSD([subQ1,subQ3]),TDD([makeQuery(id+"F1.opExtrude","CAP_VERTEX",VERTEX,{"disambiguationData":[OSD([subQ1,subQ3])],"isStart":false})])]})]}),makeQuery(id+"F4.opExtrude","SWEPT_EDGE",EDGE,{"disambiguationData":[OSD([subQ1,subQ0]),TDD([makeQuery(id+"F1.opExtrude","CAP_VERTEX",VERTEX,{"disambiguationData":[OSD([subQ1,subQ0])],"isStart":false})])]})]});var subQ13=sQuery(id+"F5.wireOp",EDGE,"E8");var subQ14=sQuery(id+"F5.wireOp",EDGE,"E7");var subQ15=sQuery(id+"F5.wireOp",EDGE,"E13");var subQ16=makeQuery(id+"F1.opExtrude","SWEPT_FACE",FACE,{"disambiguationData":[OSD([subQ1])]});var subQ17=makeQuery(id+"F4.opExtrude","SWEPT_FACE",FACE,{"disambiguationData":[OSD([subQ1,subQ0])]});Q0=makeQuery(id+"F11.boolean.opBoolean","COPY",FACE,{"derivedFrom":makeQuery(id+"F11.opExtrude","CAP_FACE",FACE,{"disambiguationData":[OSD([subQ1,subQ3,subQ0]),TDD([makeQuery(id+"F7.boolean.opBoolean","SPLIT",FACE,{"disambiguationData":[TD([subQ16,makeQuery(id+"F1.opExtrude","CAP_FACE",FACE,{"disambiguationData":[OSD([subQ1,subQ10,subQ3,subQ0])],"isStart":false}),subQ2,makeQuery(id+"F2.opExtrude","CAP_FACE",FACE,{"disambiguationData":[OSD([subQ1,subQ10,subQ3,subQ0])],"isStart":false}),makeQuery(id+"F3.opExtrude","SWEPT_FACE",FACE,{"disambiguationData":[OSD([subQ3]),TDD([makeQuery(id+"F1.opExtrude","CAP_EDGE",EDGE,{"disambiguationData":[OSD([subQ3])],"isStart":false})])]}),makeQuery(id+"F3.opExtrude","SWEPT_FACE",FACE,{"disambiguationData":[OSD([subQ3]),TDD([makeQuery(id+"F2.opExtrude","CAP_EDGE",EDGE,{"disambiguationData":[OSD([subQ3])],"isStart":false})])]}),subQ4,makeQuery(id+"F4.opExtrude","SWEPT_FACE",FACE,{"disambiguationData":[OSD([subQ0]),TDD([makeQuery(id+"F1.opExtrude","CAP_EDGE",EDGE,{"disambiguationData":[OSD([subQ0])],"isStart":false})])]}),makeQuery(id+"F4.opExtrude","SWEPT_FACE",FACE,{"disambiguationData":[OSD([subQ0]),TDD([makeQuery(id+"F2.opExtrude","CAP_EDGE",EDGE,{"disambiguationData":[OSD([subQ0])],"isStart":false})])]}),subQ17,makeQuery(id+"F7.opExtrude","SWEPT_FACE",FACE,{"disambiguationData":[OSD([subQ6])]}),makeQuery(id+"F7.opExtrude","SWEPT_FACE",FACE,{"disambiguationData":[OSD([subQ9])]}),makeQuery(id+"F7.opExtrude","SWEPT_FACE",FACE,{"disambiguationData":[OSD([subQ11])]}),makeQuery(id+"F7.opExtrude","SWEPT_FACE",FACE,{"disambiguationData":[OSD([subQ14])]}),makeQuery(id+"F7.opExtrude","SWEPT_FACE",FACE,{"disambiguationData":[OSD([subQ1,subQ3,subQ0]),TDD([makeQuery(id+"F5.imprint","IMPRINT",EDGE,{"disambiguationData":[TD([[makeQuery(id+"F5.imprint","INTERSECT",VERTEX,{"derivedFrom":[subQ12,subQ8,sQuery(id+"F5.wireOp",EDGE,"E4")]}),1.0]])],"derivedFrom":subQ12})])]}),makeQuery(id+"F7.opExtrude","SWEPT_FACE",FACE,{"disambiguationData":[OSD([subQ1,subQ3,subQ0]),TDD([makeQuery(id+"F5.imprint","IMPRINT",EDGE,{"disambiguationData":[TD([[makeQuery(id+"F5.imprint","INTERSECT",VERTEX,{"derivedFrom":[subQ12,subQ5,subQ11]}),-1.0]])],"derivedFrom":subQ12})])]}),makeQuery(id+"F7.opExtrude","SWEPT_FACE",FACE,{"disambiguationData":[OSD([subQ1,subQ3,subQ0]),TDD([makeQuery(id+"F5.imprint","IMPRINT",EDGE,{"disambiguationData":[TD([[makeQuery(id+"F5.imprint","INTERSECT",VERTEX,{"derivedFrom":[subQ7,subQ6,subQ5]}),1.0]])],"derivedFrom":subQ7})])]}),makeQuery(id+"F7.opExtrude","SWEPT_FACE",FACE,{"disambiguationData":[OSD([subQ1,subQ3,subQ0]),TDD([makeQuery(id+"F5.imprint","IMPRINT",EDGE,{"disambiguationData":[TD([[makeQuery(id+"F5.imprint","INTERSECT",VERTEX,{"derivedFrom":[subQ7,subQ13,sQuery(id+"F5.wireOp",EDGE,"E9")]}),-1.0]])],"derivedFrom":subQ7})])]}),makeQuery(id+"F7.opExtrude","SWEPT_FACE",FACE,{"disambiguationData":[OSD([subQ1,subQ3,subQ0]),TDD([makeQuery(id+"F5.imprint","IMPRINT",EDGE,{"disambiguationData":[TD([[makeQuery(id+"F5.imprint","INTERSECT",VERTEX,{"derivedFrom":[subQ7,subQ15,sQuery(id+"F5.wireOp",EDGE,"E14")]}),1.0]])],"derivedFrom":subQ7})])]})])],"derivedFrom":makeQuery(id+"F4.boolean.opBoolean","MERGE",FACE,{"derivedFrom":[makeQuery(id+"F3.boolean.opBoolean","MERGE",FACE,{"derivedFrom":[makeQuery(id+"F2.boolean.opBoolean","MERGE",FACE,{"derivedFrom":[subQ16,subQ2]}),subQ4]}),subQ17]})})])],"isStart":false})});}
            extrude(context, id + "F18", {"entities" : qUnion([Q0]), "operationType" : NewBodyOperationType.REMOVE, "oppositeDirection" : true, "depth" : 25.4 * mm, "offsetDistance" : 25.4 * mm});
        }
        {
            var Q0;
            {var subQ0=sQuery(id+"F0.wireOp",EDGE,"E0.right");var subQ1=sQuery(id+"F0.wireOp",EDGE,"E0.bottom");var subQ2=makeQuery(id+"F2.opExtrude","SWEPT_FACE",FACE,{"disambiguationData":[OSD([subQ1])]});var subQ3=sQuery(id+"F0.wireOp",EDGE,"E0.left");var subQ4=makeQuery(id+"F3.opExtrude","SWEPT_FACE",FACE,{"disambiguationData":[OSD([subQ1,subQ3])]});var subQ5=sQuery(id+"F5.wireOp",EDGE,"E5");var subQ6=makeQuery(id+"F4.boolean.opBoolean","MERGE",EDGE,{"derivedFrom":[makeQuery(id+"F3.boolean.opBoolean","MERGE",EDGE,{"derivedFrom":[makeQuery(id+"F2.opExtrude","CAP_EDGE",EDGE,{"disambiguationData":[OSD([subQ1])],"isStart":false}),makeQuery(id+"F3.opExtrude","SWEPT_EDGE",EDGE,{"disambiguationData":[OSD([subQ1,subQ3]),TDD([makeQuery(id+"F2.opExtrude","CAP_VERTEX",VERTEX,{"disambiguationData":[OSD([subQ1,subQ3])],"isStart":false})])]})]}),makeQuery(id+"F4.opExtrude","SWEPT_EDGE",EDGE,{"disambiguationData":[OSD([subQ1,subQ0]),TDD([makeQuery(id+"F2.opExtrude","CAP_VERTEX",VERTEX,{"disambiguationData":[OSD([subQ1,subQ0])],"isStart":false})])]})]});var subQ7=sQuery(id+"F5.wireOp",EDGE,"E3");var subQ8=sQuery(id+"F0.wireOp",EDGE,"E0.top");var subQ9=sQuery(id+"F5.wireOp",EDGE,"E6");var subQ10=makeQuery(id+"F4.boolean.opBoolean","MERGE",EDGE,{"derivedFrom":[makeQuery(id+"F3.boolean.opBoolean","MERGE",EDGE,{"derivedFrom":[makeQuery(id+"F1.opExtrude","CAP_EDGE",EDGE,{"disambiguationData":[OSD([subQ1])],"isStart":false}),makeQuery(id+"F3.opExtrude","SWEPT_EDGE",EDGE,{"disambiguationData":[OSD([subQ1,subQ3]),TDD([makeQuery(id+"F1.opExtrude","CAP_VERTEX",VERTEX,{"disambiguationData":[OSD([subQ1,subQ3])],"isStart":false})])]})]}),makeQuery(id+"F4.opExtrude","SWEPT_EDGE",EDGE,{"disambiguationData":[OSD([subQ1,subQ0]),TDD([makeQuery(id+"F1.opExtrude","CAP_VERTEX",VERTEX,{"disambiguationData":[OSD([subQ1,subQ0])],"isStart":false})])]})]});var subQ11=sQuery(id+"F5.wireOp",EDGE,"E8");var subQ12=sQuery(id+"F5.wireOp",EDGE,"E7");var subQ13=sQuery(id+"F5.wireOp",EDGE,"E13");var subQ14=makeQuery(id+"F1.opExtrude","SWEPT_FACE",FACE,{"disambiguationData":[OSD([subQ1])]});var subQ15=makeQuery(id+"F4.opExtrude","SWEPT_FACE",FACE,{"disambiguationData":[OSD([subQ1,subQ0])]});var subQ16=sQuery(id+"F5.wireOp",EDGE,"E9");var subQ17=sQuery(id+"F5.wireOp",EDGE,"E10");Q0=makeQuery(id+"F11.boolean.opBoolean","COPY",FACE,{"derivedFrom":makeQuery(id+"F11.opExtrude","CAP_FACE",FACE,{"disambiguationData":[OSD([subQ1,subQ3,subQ0]),TDD([makeQuery(id+"F7.boolean.opBoolean","SPLIT",FACE,{"disambiguationData":[TD([subQ14,makeQuery(id+"F1.opExtrude","CAP_FACE",FACE,{"disambiguationData":[OSD([subQ1,subQ8,subQ3,subQ0])],"isStart":false}),subQ2,makeQuery(id+"F2.opExtrude","CAP_FACE",FACE,{"disambiguationData":[OSD([subQ1,subQ8,subQ3,subQ0])],"isStart":false}),makeQuery(id+"F3.opExtrude","SWEPT_FACE",FACE,{"disambiguationData":[OSD([subQ3]),TDD([makeQuery(id+"F1.opExtrude","CAP_EDGE",EDGE,{"disambiguationData":[OSD([subQ3])],"isStart":false})])]}),makeQuery(id+"F3.opExtrude","SWEPT_FACE",FACE,{"disambiguationData":[OSD([subQ3]),TDD([makeQuery(id+"F2.opExtrude","CAP_EDGE",EDGE,{"disambiguationData":[OSD([subQ3])],"isStart":false})])]}),subQ4,makeQuery(id+"F4.opExtrude","SWEPT_FACE",FACE,{"disambiguationData":[OSD([subQ0]),TDD([makeQuery(id+"F1.opExtrude","CAP_EDGE",EDGE,{"disambiguationData":[OSD([subQ0])],"isStart":false})])]}),makeQuery(id+"F4.opExtrude","SWEPT_FACE",FACE,{"disambiguationData":[OSD([subQ0]),TDD([makeQuery(id+"F2.opExtrude","CAP_EDGE",EDGE,{"disambiguationData":[OSD([subQ0])],"isStart":false})])]}),subQ15,makeQuery(id+"F7.opExtrude","SWEPT_FACE",FACE,{"disambiguationData":[OSD([subQ9])]}),makeQuery(id+"F7.opExtrude","SWEPT_FACE",FACE,{"disambiguationData":[OSD([subQ12])]}),makeQuery(id+"F7.opExtrude","SWEPT_FACE",FACE,{"disambiguationData":[OSD([subQ16])]}),makeQuery(id+"F7.opExtrude","SWEPT_FACE",FACE,{"disambiguationData":[OSD([subQ17])]}),makeQuery(id+"F7.opExtrude","SWEPT_FACE",FACE,{"disambiguationData":[OSD([subQ1,subQ3,subQ0]),TDD([makeQuery(id+"F5.imprint","IMPRINT",EDGE,{"disambiguationData":[TD([[makeQuery(id+"F5.imprint","INTERSECT",VERTEX,{"derivedFrom":[subQ10,subQ7,sQuery(id+"F5.wireOp",EDGE,"E4")]}),1.0]])],"derivedFrom":subQ10})])]}),makeQuery(id+"F7.opExtrude","SWEPT_FACE",FACE,{"disambiguationData":[OSD([subQ1,subQ3,subQ0]),TDD([makeQuery(id+"F5.imprint","IMPRINT",EDGE,{"disambiguationData":[TD([[makeQuery(id+"F5.imprint","INTERSECT",VERTEX,{"derivedFrom":[subQ10,subQ5,subQ9]}),-1.0]])],"derivedFrom":subQ10})])]}),makeQuery(id+"F7.opExtrude","SWEPT_FACE",FACE,{"disambiguationData":[OSD([subQ1,subQ3,subQ0]),TDD([makeQuery(id+"F5.imprint","IMPRINT",EDGE,{"disambiguationData":[TD([[makeQuery(id+"F5.imprint","INTERSECT",VERTEX,{"derivedFrom":[subQ6,sQuery(id+"F5.wireOp",EDGE,"E1"),subQ5]}),1.0]])],"derivedFrom":subQ6})])]}),makeQuery(id+"F7.opExtrude","SWEPT_FACE",FACE,{"disambiguationData":[OSD([subQ1,subQ3,subQ0]),TDD([makeQuery(id+"F5.imprint","IMPRINT",EDGE,{"disambiguationData":[TD([[makeQuery(id+"F5.imprint","INTERSECT",VERTEX,{"derivedFrom":[subQ6,subQ11,subQ16]}),-1.0]])],"derivedFrom":subQ6})])]}),makeQuery(id+"F7.opExtrude","SWEPT_FACE",FACE,{"disambiguationData":[OSD([subQ1,subQ3,subQ0]),TDD([makeQuery(id+"F5.imprint","IMPRINT",EDGE,{"disambiguationData":[TD([[makeQuery(id+"F5.imprint","INTERSECT",VERTEX,{"derivedFrom":[subQ6,subQ13,sQuery(id+"F5.wireOp",EDGE,"E14")]}),1.0]])],"derivedFrom":subQ6})])]})])],"derivedFrom":makeQuery(id+"F4.boolean.opBoolean","MERGE",FACE,{"derivedFrom":[makeQuery(id+"F3.boolean.opBoolean","MERGE",FACE,{"derivedFrom":[makeQuery(id+"F2.boolean.opBoolean","MERGE",FACE,{"derivedFrom":[subQ14,subQ2]}),subQ4]}),subQ15]})})])],"isStart":false})});}
            extrude(context, id + "F19", {"entities" : qUnion([Q0]), "operationType" : NewBodyOperationType.REMOVE, "oppositeDirection" : true, "depth" : 25.4 * mm, "offsetDistance" : 25.4 * mm});
        }
        {
            var Q0;
            {var subQ0=sQuery(id+"F0.wireOp",EDGE,"E0.right");var subQ1=sQuery(id+"F0.wireOp",EDGE,"E0.bottom");var subQ2=sQuery(id+"F0.wireOp",EDGE,"E0.left");var subQ3=makeQuery(id+"F4.boolean.opBoolean","MERGE",EDGE,{"derivedFrom":[makeQuery(id+"F3.boolean.opBoolean","MERGE",EDGE,{"derivedFrom":[makeQuery(id+"F2.opExtrude","CAP_EDGE",EDGE,{"disambiguationData":[OSD([subQ1])],"isStart":false}),makeQuery(id+"F3.opExtrude","SWEPT_EDGE",EDGE,{"disambiguationData":[OSD([subQ1,subQ2]),TDD([makeQuery(id+"F2.opExtrude","CAP_VERTEX",VERTEX,{"disambiguationData":[OSD([subQ1,subQ2])],"isStart":false})])]})]}),makeQuery(id+"F4.opExtrude","SWEPT_EDGE",EDGE,{"disambiguationData":[OSD([subQ1,subQ0]),TDD([makeQuery(id+"F2.opExtrude","CAP_VERTEX",VERTEX,{"disambiguationData":[OSD([subQ1,subQ0])],"isStart":false})])]})]});var subQ4=makeQuery(id+"F5.imprint","IMPRINT",EDGE,{"disambiguationData":[TD([[makeQuery(id+"F5.imprint","INTERSECT",VERTEX,{"derivedFrom":[subQ3,sQuery(id+"F5.wireOp",EDGE,"E13"),sQuery(id+"F5.wireOp",EDGE,"E14")]}),1.0]])],"derivedFrom":subQ3});var subQ5=sQuery(id+"F0.wireOp",EDGE,"E0.top");Q0=makeQuery(id+"F15.boolean.opBoolean","COPY",FACE,{"derivedFrom":makeQuery(id+"F15.opExtrude","SWEPT_FACE",FACE,{"disambiguationData":[OSD([subQ1,subQ5,subQ2,subQ0]),TDD([makeQuery(id+"F8.opChamfer","BLEND_EDGE",EDGE,{"blendedFrom":[makeQuery(id+"F7.opExtrude","CAP_EDGE",EDGE,{"disambiguationData":[OSD([subQ1,subQ2,subQ0]),TDD([subQ4])],"isStart":false}),makeQuery(id+"F7.boolean.opBoolean","MERGE",FACE,{"derivedFrom":[makeQuery(id+"F4.boolean.opBoolean","MERGE",FACE,{"derivedFrom":[makeQuery(id+"F3.boolean.opBoolean","MERGE",FACE,{"derivedFrom":[makeQuery(id+"F2.opExtrude","CAP_FACE",FACE,{"disambiguationData":[OSD([subQ1,subQ5,subQ2,subQ0])],"isStart":false}),makeQuery(id+"F3.opExtrude","SWEPT_FACE",FACE,{"disambiguationData":[OSD([subQ2]),TDD([makeQuery(id+"F2.opExtrude","CAP_EDGE",EDGE,{"disambiguationData":[OSD([subQ2])],"isStart":false})])]})]}),makeQuery(id+"F4.opExtrude","SWEPT_FACE",FACE,{"disambiguationData":[OSD([subQ0]),TDD([makeQuery(id+"F2.opExtrude","CAP_EDGE",EDGE,{"disambiguationData":[OSD([subQ0])],"isStart":false})])]})]}),makeQuery(id+"F7.opExtrude","SWEPT_FACE",FACE,{"disambiguationData":[OSD([subQ1,subQ2,subQ0]),TDD([makeQuery(id+"F5.imprint","IMPRINT",EDGE,{"disambiguationData":[TD([[makeQuery(id+"F5.imprint","INTERSECT",VERTEX,{"derivedFrom":[subQ3,sQuery(id+"F5.wireOp",EDGE,"E1"),sQuery(id+"F5.wireOp",EDGE,"E5")]}),1.0]])],"derivedFrom":subQ3})])]}),makeQuery(id+"F7.opExtrude","SWEPT_FACE",FACE,{"disambiguationData":[OSD([subQ1,subQ2,subQ0]),TDD([makeQuery(id+"F5.imprint","IMPRINT",EDGE,{"disambiguationData":[TD([[makeQuery(id+"F5.imprint","INTERSECT",VERTEX,{"derivedFrom":[subQ3,sQuery(id+"F5.wireOp",EDGE,"E8"),sQuery(id+"F5.wireOp",EDGE,"E9")]}),-1.0]])],"derivedFrom":subQ3})])]}),makeQuery(id+"F7.opExtrude","SWEPT_FACE",FACE,{"disambiguationData":[OSD([subQ1,subQ2,subQ0]),TDD([subQ4])]})]})],"blendedInto":[makeQuery(id+"F7.boolean.opBoolean","MERGE",FACE,{"derivedFrom":[makeQuery(id+"F4.boolean.opBoolean","MERGE",FACE,{"derivedFrom":[makeQuery(id+"F3.boolean.opBoolean","MERGE",FACE,{"derivedFrom":[makeQuery(id+"F2.opExtrude","CAP_FACE",FACE,{"disambiguationData":[OSD([subQ1,subQ5,subQ2,subQ0])],"isStart":false}),makeQuery(id+"F3.opExtrude","SWEPT_FACE",FACE,{"disambiguationData":[OSD([subQ2]),TDD([makeQuery(id+"F2.opExtrude","CAP_EDGE",EDGE,{"disambiguationData":[OSD([subQ2])],"isStart":false})])]})]}),makeQuery(id+"F4.opExtrude","SWEPT_FACE",FACE,{"disambiguationData":[OSD([subQ0]),TDD([makeQuery(id+"F2.opExtrude","CAP_EDGE",EDGE,{"disambiguationData":[OSD([subQ0])],"isStart":false})])]})]}),makeQuery(id+"F7.opExtrude","SWEPT_FACE",FACE,{"disambiguationData":[OSD([subQ1,subQ2,subQ0]),TDD([makeQuery(id+"F5.imprint","IMPRINT",EDGE,{"disambiguationData":[TD([[makeQuery(id+"F5.imprint","INTERSECT",VERTEX,{"derivedFrom":[subQ3,sQuery(id+"F5.wireOp",EDGE,"E1"),sQuery(id+"F5.wireOp",EDGE,"E5")]}),1.0]])],"derivedFrom":subQ3})])]}),makeQuery(id+"F7.opExtrude","SWEPT_FACE",FACE,{"disambiguationData":[OSD([subQ1,subQ2,subQ0]),TDD([makeQuery(id+"F5.imprint","IMPRINT",EDGE,{"disambiguationData":[TD([[makeQuery(id+"F5.imprint","INTERSECT",VERTEX,{"derivedFrom":[subQ3,sQuery(id+"F5.wireOp",EDGE,"E8"),sQuery(id+"F5.wireOp",EDGE,"E9")]}),-1.0]])],"derivedFrom":subQ3})])]}),makeQuery(id+"F7.opExtrude","SWEPT_FACE",FACE,{"disambiguationData":[OSD([subQ1,subQ2,subQ0]),TDD([subQ4])]})]})]})])]})});}
            extrude(context, id + "F20", {"entities" : qUnion([Q0]), "operationType" : NewBodyOperationType.ADD, "depth" : 2.54 * mm, "offsetDistance" : 25.4 * mm});
        }
        {
            var Q0;
            Q0=makeQuery(id+"F20.opExtrude","CAP_FACE",FACE,{"disambiguationData":[OSD([sQuery(id+"F0.wireOp",EDGE,"E0.bottom"),sQuery(id+"F0.wireOp",EDGE,"E0.top"),sQuery(id+"F0.wireOp",EDGE,"E0.left"),sQuery(id+"F0.wireOp",EDGE,"E0.right")])],"isStart":false});
            extrude(context, id + "F21", {"entities" : qUnion([Q0]), "operationType" : NewBodyOperationType.REMOVE, "oppositeDirection" : true, "depth" : 1.27 * mm, "offsetDistance" : 25.4 * mm});
        }
        {
            var Q0;
            {var subQ0=sQuery(id+"F0.wireOp",EDGE,"E0.right");var subQ1=sQuery(id+"F0.wireOp",EDGE,"E0.top");var subQ2=sQuery(id+"F0.wireOp",EDGE,"E0.left");var subQ3=makeQuery(id+"F4.boolean.opBoolean","MERGE",EDGE,{"derivedFrom":[makeQuery(id+"F3.boolean.opBoolean","MERGE",EDGE,{"derivedFrom":[makeQuery(id+"F2.opExtrude","CAP_EDGE",EDGE,{"disambiguationData":[OSD([subQ1])],"isStart":false}),makeQuery(id+"F3.opExtrude","SWEPT_EDGE",EDGE,{"disambiguationData":[OSD([subQ1,subQ2]),TDD([makeQuery(id+"F2.opExtrude","CAP_VERTEX",VERTEX,{"disambiguationData":[OSD([subQ1,subQ2])],"isStart":false})])]})]}),makeQuery(id+"F4.opExtrude","SWEPT_EDGE",EDGE,{"disambiguationData":[OSD([subQ1,subQ0]),TDD([makeQuery(id+"F2.opExtrude","CAP_VERTEX",VERTEX,{"disambiguationData":[OSD([subQ1,subQ0])],"isStart":false})])]})]});var subQ4=makeQuery(id+"F6.imprint","IMPRINT",EDGE,{"disambiguationData":[TD([[makeQuery(id+"F6.imprint","INTERSECT",VERTEX,{"derivedFrom":[subQ3,sQuery(id+"F6.wireOp",EDGE,"E21"),sQuery(id+"F6.wireOp",EDGE,"E22")]}),1.0]])],"derivedFrom":subQ3});var subQ5=sQuery(id+"F0.wireOp",EDGE,"E0.bottom");var subQ6=makeQuery(id+"F4.boolean.opBoolean","MERGE",EDGE,{"derivedFrom":[makeQuery(id+"F3.boolean.opBoolean","MERGE",EDGE,{"derivedFrom":[makeQuery(id+"F2.opExtrude","CAP_EDGE",EDGE,{"disambiguationData":[OSD([subQ5])],"isStart":false}),makeQuery(id+"F3.opExtrude","SWEPT_EDGE",EDGE,{"disambiguationData":[OSD([subQ5,subQ2]),TDD([makeQuery(id+"F2.opExtrude","CAP_VERTEX",VERTEX,{"disambiguationData":[OSD([subQ5,subQ2])],"isStart":false})])]})]}),makeQuery(id+"F4.opExtrude","SWEPT_EDGE",EDGE,{"disambiguationData":[OSD([subQ5,subQ0]),TDD([makeQuery(id+"F2.opExtrude","CAP_VERTEX",VERTEX,{"disambiguationData":[OSD([subQ5,subQ0])],"isStart":false})])]})]});Q0=makeQuery(id+"F15.boolean.opBoolean","COPY",FACE,{"derivedFrom":makeQuery(id+"F15.opExtrude","SWEPT_FACE",FACE,{"disambiguationData":[OSD([subQ5,subQ1,subQ2,subQ0]),TDD([makeQuery(id+"F10.opChamfer","BLEND_EDGE",EDGE,{"blendedFrom":[makeQuery(id+"F9.opExtrude","CAP_EDGE",EDGE,{"disambiguationData":[OSD([subQ1,subQ2,subQ0]),TDD([subQ4])],"isStart":false}),makeQuery(id+"F9.boolean.opBoolean","MERGE",FACE,{"derivedFrom":[makeQuery(id+"F7.boolean.opBoolean","MERGE",FACE,{"derivedFrom":[makeQuery(id+"F4.boolean.opBoolean","MERGE",FACE,{"derivedFrom":[makeQuery(id+"F3.boolean.opBoolean","MERGE",FACE,{"derivedFrom":[makeQuery(id+"F2.opExtrude","CAP_FACE",FACE,{"disambiguationData":[OSD([subQ5,subQ1,subQ2,subQ0])],"isStart":false}),makeQuery(id+"F3.opExtrude","SWEPT_FACE",FACE,{"disambiguationData":[OSD([subQ2]),TDD([makeQuery(id+"F2.opExtrude","CAP_EDGE",EDGE,{"disambiguationData":[OSD([subQ2])],"isStart":false})])]})]}),makeQuery(id+"F4.opExtrude","SWEPT_FACE",FACE,{"disambiguationData":[OSD([subQ0]),TDD([makeQuery(id+"F2.opExtrude","CAP_EDGE",EDGE,{"disambiguationData":[OSD([subQ0])],"isStart":false})])]})]}),makeQuery(id+"F7.opExtrude","SWEPT_FACE",FACE,{"disambiguationData":[OSD([subQ5,subQ2,subQ0]),TDD([makeQuery(id+"F5.imprint","IMPRINT",EDGE,{"disambiguationData":[TD([[makeQuery(id+"F5.imprint","INTERSECT",VERTEX,{"derivedFrom":[subQ6,sQuery(id+"F5.wireOp",EDGE,"E1"),sQuery(id+"F5.wireOp",EDGE,"E5")]}),1.0]])],"derivedFrom":subQ6})])]}),makeQuery(id+"F7.opExtrude","SWEPT_FACE",FACE,{"disambiguationData":[OSD([subQ5,subQ2,subQ0]),TDD([makeQuery(id+"F5.imprint","IMPRINT",EDGE,{"disambiguationData":[TD([[makeQuery(id+"F5.imprint","INTERSECT",VERTEX,{"derivedFrom":[subQ6,sQuery(id+"F5.wireOp",EDGE,"E8"),sQuery(id+"F5.wireOp",EDGE,"E9")]}),-1.0]])],"derivedFrom":subQ6})])]}),makeQuery(id+"F7.opExtrude","SWEPT_FACE",FACE,{"disambiguationData":[OSD([subQ5,subQ2,subQ0]),TDD([makeQuery(id+"F5.imprint","IMPRINT",EDGE,{"disambiguationData":[TD([[makeQuery(id+"F5.imprint","INTERSECT",VERTEX,{"derivedFrom":[subQ6,sQuery(id+"F5.wireOp",EDGE,"E13"),sQuery(id+"F5.wireOp",EDGE,"E14")]}),1.0]])],"derivedFrom":subQ6})])]})]}),makeQuery(id+"F9.opExtrude","SWEPT_FACE",FACE,{"disambiguationData":[OSD([subQ1,subQ2,subQ0]),TDD([makeQuery(id+"F6.imprint","IMPRINT",EDGE,{"disambiguationData":[TD([[makeQuery(id+"F6.imprint","INTERSECT",VERTEX,{"derivedFrom":[subQ3,sQuery(id+"F6.wireOp",EDGE,"E17"),sQuery(id+"F6.wireOp",EDGE,"E18")]}),-1.0]])],"derivedFrom":subQ3})])]}),makeQuery(id+"F9.opExtrude","SWEPT_FACE",FACE,{"disambiguationData":[OSD([subQ1,subQ2,subQ0]),TDD([subQ4])]}),makeQuery(id+"F9.opExtrude","SWEPT_FACE",FACE,{"disambiguationData":[OSD([subQ1,subQ2,subQ0]),TDD([makeQuery(id+"F6.imprint","IMPRINT",EDGE,{"disambiguationData":[TD([[makeQuery(id+"F6.imprint","INTERSECT",VERTEX,{"derivedFrom":[subQ3,sQuery(id+"F6.wireOp",EDGE,"E29"),sQuery(id+"F6.wireOp",EDGE,"E30")]}),-1.0]])],"derivedFrom":subQ3})])]})]})],"blendedInto":[makeQuery(id+"F9.boolean.opBoolean","MERGE",FACE,{"derivedFrom":[makeQuery(id+"F7.boolean.opBoolean","MERGE",FACE,{"derivedFrom":[makeQuery(id+"F4.boolean.opBoolean","MERGE",FACE,{"derivedFrom":[makeQuery(id+"F3.boolean.opBoolean","MERGE",FACE,{"derivedFrom":[makeQuery(id+"F2.opExtrude","CAP_FACE",FACE,{"disambiguationData":[OSD([subQ5,subQ1,subQ2,subQ0])],"isStart":false}),makeQuery(id+"F3.opExtrude","SWEPT_FACE",FACE,{"disambiguationData":[OSD([subQ2]),TDD([makeQuery(id+"F2.opExtrude","CAP_EDGE",EDGE,{"disambiguationData":[OSD([subQ2])],"isStart":false})])]})]}),makeQuery(id+"F4.opExtrude","SWEPT_FACE",FACE,{"disambiguationData":[OSD([subQ0]),TDD([makeQuery(id+"F2.opExtrude","CAP_EDGE",EDGE,{"disambiguationData":[OSD([subQ0])],"isStart":false})])]})]}),makeQuery(id+"F7.opExtrude","SWEPT_FACE",FACE,{"disambiguationData":[OSD([subQ5,subQ2,subQ0]),TDD([makeQuery(id+"F5.imprint","IMPRINT",EDGE,{"disambiguationData":[TD([[makeQuery(id+"F5.imprint","INTERSECT",VERTEX,{"derivedFrom":[subQ6,sQuery(id+"F5.wireOp",EDGE,"E1"),sQuery(id+"F5.wireOp",EDGE,"E5")]}),1.0]])],"derivedFrom":subQ6})])]}),makeQuery(id+"F7.opExtrude","SWEPT_FACE",FACE,{"disambiguationData":[OSD([subQ5,subQ2,subQ0]),TDD([makeQuery(id+"F5.imprint","IMPRINT",EDGE,{"disambiguationData":[TD([[makeQuery(id+"F5.imprint","INTERSECT",VERTEX,{"derivedFrom":[subQ6,sQuery(id+"F5.wireOp",EDGE,"E8"),sQuery(id+"F5.wireOp",EDGE,"E9")]}),-1.0]])],"derivedFrom":subQ6})])]}),makeQuery(id+"F7.opExtrude","SWEPT_FACE",FACE,{"disambiguationData":[OSD([subQ5,subQ2,subQ0]),TDD([makeQuery(id+"F5.imprint","IMPRINT",EDGE,{"disambiguationData":[TD([[makeQuery(id+"F5.imprint","INTERSECT",VERTEX,{"derivedFrom":[subQ6,sQuery(id+"F5.wireOp",EDGE,"E13"),sQuery(id+"F5.wireOp",EDGE,"E14")]}),1.0]])],"derivedFrom":subQ6})])]})]}),makeQuery(id+"F9.opExtrude","SWEPT_FACE",FACE,{"disambiguationData":[OSD([subQ1,subQ2,subQ0]),TDD([makeQuery(id+"F6.imprint","IMPRINT",EDGE,{"disambiguationData":[TD([[makeQuery(id+"F6.imprint","INTERSECT",VERTEX,{"derivedFrom":[subQ3,sQuery(id+"F6.wireOp",EDGE,"E17"),sQuery(id+"F6.wireOp",EDGE,"E18")]}),-1.0]])],"derivedFrom":subQ3})])]}),makeQuery(id+"F9.opExtrude","SWEPT_FACE",FACE,{"disambiguationData":[OSD([subQ1,subQ2,subQ0]),TDD([subQ4])]}),makeQuery(id+"F9.opExtrude","SWEPT_FACE",FACE,{"disambiguationData":[OSD([subQ1,subQ2,subQ0]),TDD([makeQuery(id+"F6.imprint","IMPRINT",EDGE,{"disambiguationData":[TD([[makeQuery(id+"F6.imprint","INTERSECT",VERTEX,{"derivedFrom":[subQ3,sQuery(id+"F6.wireOp",EDGE,"E29"),sQuery(id+"F6.wireOp",EDGE,"E30")]}),-1.0]])],"derivedFrom":subQ3})])]})]})]})])]})});}
            extrude(context, id + "F22", {"entities" : qUnion([Q0]), "operationType" : NewBodyOperationType.ADD, "depth" : 1.27 * mm, "offsetDistance" : 25.4 * mm});
        }
        {
            var Q0;
            {var subQ0=sQuery(id+"F0.wireOp",EDGE,"E0.right");var subQ1=sQuery(id+"F0.wireOp",EDGE,"E0.bottom");var subQ2=sQuery(id+"F0.wireOp",EDGE,"E0.left");var subQ3=makeQuery(id+"F4.boolean.opBoolean","MERGE",EDGE,{"derivedFrom":[makeQuery(id+"F3.boolean.opBoolean","MERGE",EDGE,{"derivedFrom":[makeQuery(id+"F2.opExtrude","CAP_EDGE",EDGE,{"disambiguationData":[OSD([subQ1])],"isStart":false}),makeQuery(id+"F3.opExtrude","SWEPT_EDGE",EDGE,{"disambiguationData":[OSD([subQ1,subQ2]),TDD([makeQuery(id+"F2.opExtrude","CAP_VERTEX",VERTEX,{"disambiguationData":[OSD([subQ1,subQ2])],"isStart":false})])]})]}),makeQuery(id+"F4.opExtrude","SWEPT_EDGE",EDGE,{"disambiguationData":[OSD([subQ1,subQ0]),TDD([makeQuery(id+"F2.opExtrude","CAP_VERTEX",VERTEX,{"disambiguationData":[OSD([subQ1,subQ0])],"isStart":false})])]})]});var subQ4=makeQuery(id+"F5.imprint","IMPRINT",EDGE,{"disambiguationData":[TD([[makeQuery(id+"F5.imprint","INTERSECT",VERTEX,{"derivedFrom":[subQ3,sQuery(id+"F5.wireOp",EDGE,"E1"),sQuery(id+"F5.wireOp",EDGE,"E5")]}),1.0]])],"derivedFrom":subQ3});var subQ5=sQuery(id+"F0.wireOp",EDGE,"E0.top");Q0=makeQuery(id+"F15.boolean.opBoolean","COPY",FACE,{"derivedFrom":makeQuery(id+"F15.opExtrude","SWEPT_FACE",FACE,{"disambiguationData":[OSD([subQ1,subQ5,subQ2,subQ0]),TDD([makeQuery(id+"F8.opChamfer","BLEND_EDGE",EDGE,{"blendedFrom":[makeQuery(id+"F7.opExtrude","CAP_EDGE",EDGE,{"disambiguationData":[OSD([subQ1,subQ2,subQ0]),TDD([subQ4])],"isStart":false}),makeQuery(id+"F7.boolean.opBoolean","MERGE",FACE,{"derivedFrom":[makeQuery(id+"F4.boolean.opBoolean","MERGE",FACE,{"derivedFrom":[makeQuery(id+"F3.boolean.opBoolean","MERGE",FACE,{"derivedFrom":[makeQuery(id+"F2.opExtrude","CAP_FACE",FACE,{"disambiguationData":[OSD([subQ1,subQ5,subQ2,subQ0])],"isStart":false}),makeQuery(id+"F3.opExtrude","SWEPT_FACE",FACE,{"disambiguationData":[OSD([subQ2]),TDD([makeQuery(id+"F2.opExtrude","CAP_EDGE",EDGE,{"disambiguationData":[OSD([subQ2])],"isStart":false})])]})]}),makeQuery(id+"F4.opExtrude","SWEPT_FACE",FACE,{"disambiguationData":[OSD([subQ0]),TDD([makeQuery(id+"F2.opExtrude","CAP_EDGE",EDGE,{"disambiguationData":[OSD([subQ0])],"isStart":false})])]})]}),makeQuery(id+"F7.opExtrude","SWEPT_FACE",FACE,{"disambiguationData":[OSD([subQ1,subQ2,subQ0]),TDD([subQ4])]}),makeQuery(id+"F7.opExtrude","SWEPT_FACE",FACE,{"disambiguationData":[OSD([subQ1,subQ2,subQ0]),TDD([makeQuery(id+"F5.imprint","IMPRINT",EDGE,{"disambiguationData":[TD([[makeQuery(id+"F5.imprint","INTERSECT",VERTEX,{"derivedFrom":[subQ3,sQuery(id+"F5.wireOp",EDGE,"E8"),sQuery(id+"F5.wireOp",EDGE,"E9")]}),-1.0]])],"derivedFrom":subQ3})])]}),makeQuery(id+"F7.opExtrude","SWEPT_FACE",FACE,{"disambiguationData":[OSD([subQ1,subQ2,subQ0]),TDD([makeQuery(id+"F5.imprint","IMPRINT",EDGE,{"disambiguationData":[TD([[makeQuery(id+"F5.imprint","INTERSECT",VERTEX,{"derivedFrom":[subQ3,sQuery(id+"F5.wireOp",EDGE,"E13"),sQuery(id+"F5.wireOp",EDGE,"E14")]}),1.0]])],"derivedFrom":subQ3})])]})]})],"blendedInto":[makeQuery(id+"F7.boolean.opBoolean","MERGE",FACE,{"derivedFrom":[makeQuery(id+"F4.boolean.opBoolean","MERGE",FACE,{"derivedFrom":[makeQuery(id+"F3.boolean.opBoolean","MERGE",FACE,{"derivedFrom":[makeQuery(id+"F2.opExtrude","CAP_FACE",FACE,{"disambiguationData":[OSD([subQ1,subQ5,subQ2,subQ0])],"isStart":false}),makeQuery(id+"F3.opExtrude","SWEPT_FACE",FACE,{"disambiguationData":[OSD([subQ2]),TDD([makeQuery(id+"F2.opExtrude","CAP_EDGE",EDGE,{"disambiguationData":[OSD([subQ2])],"isStart":false})])]})]}),makeQuery(id+"F4.opExtrude","SWEPT_FACE",FACE,{"disambiguationData":[OSD([subQ0]),TDD([makeQuery(id+"F2.opExtrude","CAP_EDGE",EDGE,{"disambiguationData":[OSD([subQ0])],"isStart":false})])]})]}),makeQuery(id+"F7.opExtrude","SWEPT_FACE",FACE,{"disambiguationData":[OSD([subQ1,subQ2,subQ0]),TDD([subQ4])]}),makeQuery(id+"F7.opExtrude","SWEPT_FACE",FACE,{"disambiguationData":[OSD([subQ1,subQ2,subQ0]),TDD([makeQuery(id+"F5.imprint","IMPRINT",EDGE,{"disambiguationData":[TD([[makeQuery(id+"F5.imprint","INTERSECT",VERTEX,{"derivedFrom":[subQ3,sQuery(id+"F5.wireOp",EDGE,"E8"),sQuery(id+"F5.wireOp",EDGE,"E9")]}),-1.0]])],"derivedFrom":subQ3})])]}),makeQuery(id+"F7.opExtrude","SWEPT_FACE",FACE,{"disambiguationData":[OSD([subQ1,subQ2,subQ0]),TDD([makeQuery(id+"F5.imprint","IMPRINT",EDGE,{"disambiguationData":[TD([[makeQuery(id+"F5.imprint","INTERSECT",VERTEX,{"derivedFrom":[subQ3,sQuery(id+"F5.wireOp",EDGE,"E13"),sQuery(id+"F5.wireOp",EDGE,"E14")]}),1.0]])],"derivedFrom":subQ3})])]})]})]})])]})});}
            extrude(context, id + "F23", {"entities" : qUnion([Q0]), "operationType" : NewBodyOperationType.ADD, "depth" : 1.27 * mm, "offsetDistance" : 25.4 * mm});
        }
        {
            var Q0;
            {var subQ0=sQuery(id+"F0.wireOp",EDGE,"E0.right");var subQ1=sQuery(id+"F0.wireOp",EDGE,"E0.top");var subQ2=sQuery(id+"F0.wireOp",EDGE,"E0.left");var subQ3=makeQuery(id+"F4.boolean.opBoolean","MERGE",EDGE,{"derivedFrom":[makeQuery(id+"F3.boolean.opBoolean","MERGE",EDGE,{"derivedFrom":[makeQuery(id+"F2.opExtrude","CAP_EDGE",EDGE,{"disambiguationData":[OSD([subQ1])],"isStart":false}),makeQuery(id+"F3.opExtrude","SWEPT_EDGE",EDGE,{"disambiguationData":[OSD([subQ1,subQ2]),TDD([makeQuery(id+"F2.opExtrude","CAP_VERTEX",VERTEX,{"disambiguationData":[OSD([subQ1,subQ2])],"isStart":false})])]})]}),makeQuery(id+"F4.opExtrude","SWEPT_EDGE",EDGE,{"disambiguationData":[OSD([subQ1,subQ0]),TDD([makeQuery(id+"F2.opExtrude","CAP_VERTEX",VERTEX,{"disambiguationData":[OSD([subQ1,subQ0])],"isStart":false})])]})]});var subQ4=makeQuery(id+"F6.imprint","IMPRINT",EDGE,{"disambiguationData":[TD([[makeQuery(id+"F6.imprint","INTERSECT",VERTEX,{"derivedFrom":[subQ3,sQuery(id+"F6.wireOp",EDGE,"E17"),sQuery(id+"F6.wireOp",EDGE,"E18")]}),-1.0]])],"derivedFrom":subQ3});var subQ5=sQuery(id+"F0.wireOp",EDGE,"E0.bottom");var subQ6=makeQuery(id+"F4.boolean.opBoolean","MERGE",EDGE,{"derivedFrom":[makeQuery(id+"F3.boolean.opBoolean","MERGE",EDGE,{"derivedFrom":[makeQuery(id+"F2.opExtrude","CAP_EDGE",EDGE,{"disambiguationData":[OSD([subQ5])],"isStart":false}),makeQuery(id+"F3.opExtrude","SWEPT_EDGE",EDGE,{"disambiguationData":[OSD([subQ5,subQ2]),TDD([makeQuery(id+"F2.opExtrude","CAP_VERTEX",VERTEX,{"disambiguationData":[OSD([subQ5,subQ2])],"isStart":false})])]})]}),makeQuery(id+"F4.opExtrude","SWEPT_EDGE",EDGE,{"disambiguationData":[OSD([subQ5,subQ0]),TDD([makeQuery(id+"F2.opExtrude","CAP_VERTEX",VERTEX,{"disambiguationData":[OSD([subQ5,subQ0])],"isStart":false})])]})]});Q0=makeQuery(id+"F15.boolean.opBoolean","COPY",FACE,{"derivedFrom":makeQuery(id+"F15.opExtrude","SWEPT_FACE",FACE,{"disambiguationData":[OSD([subQ5,subQ1,subQ2,subQ0]),TDD([makeQuery(id+"F10.opChamfer","BLEND_EDGE",EDGE,{"blendedFrom":[makeQuery(id+"F9.opExtrude","CAP_EDGE",EDGE,{"disambiguationData":[OSD([subQ1,subQ2,subQ0]),TDD([subQ4])],"isStart":false}),makeQuery(id+"F9.boolean.opBoolean","MERGE",FACE,{"derivedFrom":[makeQuery(id+"F7.boolean.opBoolean","MERGE",FACE,{"derivedFrom":[makeQuery(id+"F4.boolean.opBoolean","MERGE",FACE,{"derivedFrom":[makeQuery(id+"F3.boolean.opBoolean","MERGE",FACE,{"derivedFrom":[makeQuery(id+"F2.opExtrude","CAP_FACE",FACE,{"disambiguationData":[OSD([subQ5,subQ1,subQ2,subQ0])],"isStart":false}),makeQuery(id+"F3.opExtrude","SWEPT_FACE",FACE,{"disambiguationData":[OSD([subQ2]),TDD([makeQuery(id+"F2.opExtrude","CAP_EDGE",EDGE,{"disambiguationData":[OSD([subQ2])],"isStart":false})])]})]}),makeQuery(id+"F4.opExtrude","SWEPT_FACE",FACE,{"disambiguationData":[OSD([subQ0]),TDD([makeQuery(id+"F2.opExtrude","CAP_EDGE",EDGE,{"disambiguationData":[OSD([subQ0])],"isStart":false})])]})]}),makeQuery(id+"F7.opExtrude","SWEPT_FACE",FACE,{"disambiguationData":[OSD([subQ5,subQ2,subQ0]),TDD([makeQuery(id+"F5.imprint","IMPRINT",EDGE,{"disambiguationData":[TD([[makeQuery(id+"F5.imprint","INTERSECT",VERTEX,{"derivedFrom":[subQ6,sQuery(id+"F5.wireOp",EDGE,"E1"),sQuery(id+"F5.wireOp",EDGE,"E5")]}),1.0]])],"derivedFrom":subQ6})])]}),makeQuery(id+"F7.opExtrude","SWEPT_FACE",FACE,{"disambiguationData":[OSD([subQ5,subQ2,subQ0]),TDD([makeQuery(id+"F5.imprint","IMPRINT",EDGE,{"disambiguationData":[TD([[makeQuery(id+"F5.imprint","INTERSECT",VERTEX,{"derivedFrom":[subQ6,sQuery(id+"F5.wireOp",EDGE,"E8"),sQuery(id+"F5.wireOp",EDGE,"E9")]}),-1.0]])],"derivedFrom":subQ6})])]}),makeQuery(id+"F7.opExtrude","SWEPT_FACE",FACE,{"disambiguationData":[OSD([subQ5,subQ2,subQ0]),TDD([makeQuery(id+"F5.imprint","IMPRINT",EDGE,{"disambiguationData":[TD([[makeQuery(id+"F5.imprint","INTERSECT",VERTEX,{"derivedFrom":[subQ6,sQuery(id+"F5.wireOp",EDGE,"E13"),sQuery(id+"F5.wireOp",EDGE,"E14")]}),1.0]])],"derivedFrom":subQ6})])]})]}),makeQuery(id+"F9.opExtrude","SWEPT_FACE",FACE,{"disambiguationData":[OSD([subQ1,subQ2,subQ0]),TDD([subQ4])]}),makeQuery(id+"F9.opExtrude","SWEPT_FACE",FACE,{"disambiguationData":[OSD([subQ1,subQ2,subQ0]),TDD([makeQuery(id+"F6.imprint","IMPRINT",EDGE,{"disambiguationData":[TD([[makeQuery(id+"F6.imprint","INTERSECT",VERTEX,{"derivedFrom":[subQ3,sQuery(id+"F6.wireOp",EDGE,"E21"),sQuery(id+"F6.wireOp",EDGE,"E22")]}),1.0]])],"derivedFrom":subQ3})])]}),makeQuery(id+"F9.opExtrude","SWEPT_FACE",FACE,{"disambiguationData":[OSD([subQ1,subQ2,subQ0]),TDD([makeQuery(id+"F6.imprint","IMPRINT",EDGE,{"disambiguationData":[TD([[makeQuery(id+"F6.imprint","INTERSECT",VERTEX,{"derivedFrom":[subQ3,sQuery(id+"F6.wireOp",EDGE,"E29"),sQuery(id+"F6.wireOp",EDGE,"E30")]}),-1.0]])],"derivedFrom":subQ3})])]})]})],"blendedInto":[makeQuery(id+"F9.boolean.opBoolean","MERGE",FACE,{"derivedFrom":[makeQuery(id+"F7.boolean.opBoolean","MERGE",FACE,{"derivedFrom":[makeQuery(id+"F4.boolean.opBoolean","MERGE",FACE,{"derivedFrom":[makeQuery(id+"F3.boolean.opBoolean","MERGE",FACE,{"derivedFrom":[makeQuery(id+"F2.opExtrude","CAP_FACE",FACE,{"disambiguationData":[OSD([subQ5,subQ1,subQ2,subQ0])],"isStart":false}),makeQuery(id+"F3.opExtrude","SWEPT_FACE",FACE,{"disambiguationData":[OSD([subQ2]),TDD([makeQuery(id+"F2.opExtrude","CAP_EDGE",EDGE,{"disambiguationData":[OSD([subQ2])],"isStart":false})])]})]}),makeQuery(id+"F4.opExtrude","SWEPT_FACE",FACE,{"disambiguationData":[OSD([subQ0]),TDD([makeQuery(id+"F2.opExtrude","CAP_EDGE",EDGE,{"disambiguationData":[OSD([subQ0])],"isStart":false})])]})]}),makeQuery(id+"F7.opExtrude","SWEPT_FACE",FACE,{"disambiguationData":[OSD([subQ5,subQ2,subQ0]),TDD([makeQuery(id+"F5.imprint","IMPRINT",EDGE,{"disambiguationData":[TD([[makeQuery(id+"F5.imprint","INTERSECT",VERTEX,{"derivedFrom":[subQ6,sQuery(id+"F5.wireOp",EDGE,"E1"),sQuery(id+"F5.wireOp",EDGE,"E5")]}),1.0]])],"derivedFrom":subQ6})])]}),makeQuery(id+"F7.opExtrude","SWEPT_FACE",FACE,{"disambiguationData":[OSD([subQ5,subQ2,subQ0]),TDD([makeQuery(id+"F5.imprint","IMPRINT",EDGE,{"disambiguationData":[TD([[makeQuery(id+"F5.imprint","INTERSECT",VERTEX,{"derivedFrom":[subQ6,sQuery(id+"F5.wireOp",EDGE,"E8"),sQuery(id+"F5.wireOp",EDGE,"E9")]}),-1.0]])],"derivedFrom":subQ6})])]}),makeQuery(id+"F7.opExtrude","SWEPT_FACE",FACE,{"disambiguationData":[OSD([subQ5,subQ2,subQ0]),TDD([makeQuery(id+"F5.imprint","IMPRINT",EDGE,{"disambiguationData":[TD([[makeQuery(id+"F5.imprint","INTERSECT",VERTEX,{"derivedFrom":[subQ6,sQuery(id+"F5.wireOp",EDGE,"E13"),sQuery(id+"F5.wireOp",EDGE,"E14")]}),1.0]])],"derivedFrom":subQ6})])]})]}),makeQuery(id+"F9.opExtrude","SWEPT_FACE",FACE,{"disambiguationData":[OSD([subQ1,subQ2,subQ0]),TDD([subQ4])]}),makeQuery(id+"F9.opExtrude","SWEPT_FACE",FACE,{"disambiguationData":[OSD([subQ1,subQ2,subQ0]),TDD([makeQuery(id+"F6.imprint","IMPRINT",EDGE,{"disambiguationData":[TD([[makeQuery(id+"F6.imprint","INTERSECT",VERTEX,{"derivedFrom":[subQ3,sQuery(id+"F6.wireOp",EDGE,"E21"),sQuery(id+"F6.wireOp",EDGE,"E22")]}),1.0]])],"derivedFrom":subQ3})])]}),makeQuery(id+"F9.opExtrude","SWEPT_FACE",FACE,{"disambiguationData":[OSD([subQ1,subQ2,subQ0]),TDD([makeQuery(id+"F6.imprint","IMPRINT",EDGE,{"disambiguationData":[TD([[makeQuery(id+"F6.imprint","INTERSECT",VERTEX,{"derivedFrom":[subQ3,sQuery(id+"F6.wireOp",EDGE,"E29"),sQuery(id+"F6.wireOp",EDGE,"E30")]}),-1.0]])],"derivedFrom":subQ3})])]})]})]})])]})});}
            extrude(context, id + "F24", {"entities" : qUnion([Q0]), "operationType" : NewBodyOperationType.ADD, "depth" : 1.27 * mm, "offsetDistance" : 25.4 * mm});
        }
        {
            var Q0;
            {var subQ0=sQuery(id+"F0.wireOp",EDGE,"E0.right");var subQ1=sQuery(id+"F0.wireOp",EDGE,"E0.bottom");var subQ2=sQuery(id+"F0.wireOp",EDGE,"E0.left");var subQ3=makeQuery(id+"F4.boolean.opBoolean","MERGE",EDGE,{"derivedFrom":[makeQuery(id+"F3.boolean.opBoolean","MERGE",EDGE,{"derivedFrom":[makeQuery(id+"F2.opExtrude","CAP_EDGE",EDGE,{"disambiguationData":[OSD([subQ1])],"isStart":false}),makeQuery(id+"F3.opExtrude","SWEPT_EDGE",EDGE,{"disambiguationData":[OSD([subQ1,subQ2]),TDD([makeQuery(id+"F2.opExtrude","CAP_VERTEX",VERTEX,{"disambiguationData":[OSD([subQ1,subQ2])],"isStart":false})])]})]}),makeQuery(id+"F4.opExtrude","SWEPT_EDGE",EDGE,{"disambiguationData":[OSD([subQ1,subQ0]),TDD([makeQuery(id+"F2.opExtrude","CAP_VERTEX",VERTEX,{"disambiguationData":[OSD([subQ1,subQ0])],"isStart":false})])]})]});var subQ4=makeQuery(id+"F5.imprint","IMPRINT",EDGE,{"disambiguationData":[TD([[makeQuery(id+"F5.imprint","INTERSECT",VERTEX,{"derivedFrom":[subQ3,sQuery(id+"F5.wireOp",EDGE,"E8"),sQuery(id+"F5.wireOp",EDGE,"E9")]}),-1.0]])],"derivedFrom":subQ3});var subQ5=sQuery(id+"F0.wireOp",EDGE,"E0.top");Q0=makeQuery(id+"F15.boolean.opBoolean","COPY",FACE,{"derivedFrom":makeQuery(id+"F15.opExtrude","SWEPT_FACE",FACE,{"disambiguationData":[OSD([subQ1,subQ5,subQ2,subQ0]),TDD([makeQuery(id+"F8.opChamfer","BLEND_EDGE",EDGE,{"blendedFrom":[makeQuery(id+"F7.opExtrude","CAP_EDGE",EDGE,{"disambiguationData":[OSD([subQ1,subQ2,subQ0]),TDD([subQ4])],"isStart":false}),makeQuery(id+"F7.boolean.opBoolean","MERGE",FACE,{"derivedFrom":[makeQuery(id+"F4.boolean.opBoolean","MERGE",FACE,{"derivedFrom":[makeQuery(id+"F3.boolean.opBoolean","MERGE",FACE,{"derivedFrom":[makeQuery(id+"F2.opExtrude","CAP_FACE",FACE,{"disambiguationData":[OSD([subQ1,subQ5,subQ2,subQ0])],"isStart":false}),makeQuery(id+"F3.opExtrude","SWEPT_FACE",FACE,{"disambiguationData":[OSD([subQ2]),TDD([makeQuery(id+"F2.opExtrude","CAP_EDGE",EDGE,{"disambiguationData":[OSD([subQ2])],"isStart":false})])]})]}),makeQuery(id+"F4.opExtrude","SWEPT_FACE",FACE,{"disambiguationData":[OSD([subQ0]),TDD([makeQuery(id+"F2.opExtrude","CAP_EDGE",EDGE,{"disambiguationData":[OSD([subQ0])],"isStart":false})])]})]}),makeQuery(id+"F7.opExtrude","SWEPT_FACE",FACE,{"disambiguationData":[OSD([subQ1,subQ2,subQ0]),TDD([makeQuery(id+"F5.imprint","IMPRINT",EDGE,{"disambiguationData":[TD([[makeQuery(id+"F5.imprint","INTERSECT",VERTEX,{"derivedFrom":[subQ3,sQuery(id+"F5.wireOp",EDGE,"E1"),sQuery(id+"F5.wireOp",EDGE,"E5")]}),1.0]])],"derivedFrom":subQ3})])]}),makeQuery(id+"F7.opExtrude","SWEPT_FACE",FACE,{"disambiguationData":[OSD([subQ1,subQ2,subQ0]),TDD([subQ4])]}),makeQuery(id+"F7.opExtrude","SWEPT_FACE",FACE,{"disambiguationData":[OSD([subQ1,subQ2,subQ0]),TDD([makeQuery(id+"F5.imprint","IMPRINT",EDGE,{"disambiguationData":[TD([[makeQuery(id+"F5.imprint","INTERSECT",VERTEX,{"derivedFrom":[subQ3,sQuery(id+"F5.wireOp",EDGE,"E13"),sQuery(id+"F5.wireOp",EDGE,"E14")]}),1.0]])],"derivedFrom":subQ3})])]})]})],"blendedInto":[makeQuery(id+"F7.boolean.opBoolean","MERGE",FACE,{"derivedFrom":[makeQuery(id+"F4.boolean.opBoolean","MERGE",FACE,{"derivedFrom":[makeQuery(id+"F3.boolean.opBoolean","MERGE",FACE,{"derivedFrom":[makeQuery(id+"F2.opExtrude","CAP_FACE",FACE,{"disambiguationData":[OSD([subQ1,subQ5,subQ2,subQ0])],"isStart":false}),makeQuery(id+"F3.opExtrude","SWEPT_FACE",FACE,{"disambiguationData":[OSD([subQ2]),TDD([makeQuery(id+"F2.opExtrude","CAP_EDGE",EDGE,{"disambiguationData":[OSD([subQ2])],"isStart":false})])]})]}),makeQuery(id+"F4.opExtrude","SWEPT_FACE",FACE,{"disambiguationData":[OSD([subQ0]),TDD([makeQuery(id+"F2.opExtrude","CAP_EDGE",EDGE,{"disambiguationData":[OSD([subQ0])],"isStart":false})])]})]}),makeQuery(id+"F7.opExtrude","SWEPT_FACE",FACE,{"disambiguationData":[OSD([subQ1,subQ2,subQ0]),TDD([makeQuery(id+"F5.imprint","IMPRINT",EDGE,{"disambiguationData":[TD([[makeQuery(id+"F5.imprint","INTERSECT",VERTEX,{"derivedFrom":[subQ3,sQuery(id+"F5.wireOp",EDGE,"E1"),sQuery(id+"F5.wireOp",EDGE,"E5")]}),1.0]])],"derivedFrom":subQ3})])]}),makeQuery(id+"F7.opExtrude","SWEPT_FACE",FACE,{"disambiguationData":[OSD([subQ1,subQ2,subQ0]),TDD([subQ4])]}),makeQuery(id+"F7.opExtrude","SWEPT_FACE",FACE,{"disambiguationData":[OSD([subQ1,subQ2,subQ0]),TDD([makeQuery(id+"F5.imprint","IMPRINT",EDGE,{"disambiguationData":[TD([[makeQuery(id+"F5.imprint","INTERSECT",VERTEX,{"derivedFrom":[subQ3,sQuery(id+"F5.wireOp",EDGE,"E13"),sQuery(id+"F5.wireOp",EDGE,"E14")]}),1.0]])],"derivedFrom":subQ3})])]})]})]})])]})});}
            extrude(context, id + "F25", {"entities" : qUnion([Q0]), "operationType" : NewBodyOperationType.ADD, "depth" : 1.27 * mm, "offsetDistance" : 25.4 * mm});
        }
        {
            var Q0;
            {var subQ0=sQuery(id+"F0.wireOp",EDGE,"E0.right");var subQ1=sQuery(id+"F0.wireOp",EDGE,"E0.top");var subQ2=sQuery(id+"F0.wireOp",EDGE,"E0.left");var subQ3=makeQuery(id+"F4.boolean.opBoolean","MERGE",EDGE,{"derivedFrom":[makeQuery(id+"F3.boolean.opBoolean","MERGE",EDGE,{"derivedFrom":[makeQuery(id+"F2.opExtrude","CAP_EDGE",EDGE,{"disambiguationData":[OSD([subQ1])],"isStart":false}),makeQuery(id+"F3.opExtrude","SWEPT_EDGE",EDGE,{"disambiguationData":[OSD([subQ1,subQ2]),TDD([makeQuery(id+"F2.opExtrude","CAP_VERTEX",VERTEX,{"disambiguationData":[OSD([subQ1,subQ2])],"isStart":false})])]})]}),makeQuery(id+"F4.opExtrude","SWEPT_EDGE",EDGE,{"disambiguationData":[OSD([subQ1,subQ0]),TDD([makeQuery(id+"F2.opExtrude","CAP_VERTEX",VERTEX,{"disambiguationData":[OSD([subQ1,subQ0])],"isStart":false})])]})]});var subQ4=makeQuery(id+"F6.imprint","IMPRINT",EDGE,{"disambiguationData":[TD([[makeQuery(id+"F6.imprint","INTERSECT",VERTEX,{"derivedFrom":[subQ3,sQuery(id+"F6.wireOp",EDGE,"E29"),sQuery(id+"F6.wireOp",EDGE,"E30")]}),-1.0]])],"derivedFrom":subQ3});var subQ5=sQuery(id+"F0.wireOp",EDGE,"E0.bottom");var subQ6=makeQuery(id+"F4.boolean.opBoolean","MERGE",EDGE,{"derivedFrom":[makeQuery(id+"F3.boolean.opBoolean","MERGE",EDGE,{"derivedFrom":[makeQuery(id+"F2.opExtrude","CAP_EDGE",EDGE,{"disambiguationData":[OSD([subQ5])],"isStart":false}),makeQuery(id+"F3.opExtrude","SWEPT_EDGE",EDGE,{"disambiguationData":[OSD([subQ5,subQ2]),TDD([makeQuery(id+"F2.opExtrude","CAP_VERTEX",VERTEX,{"disambiguationData":[OSD([subQ5,subQ2])],"isStart":false})])]})]}),makeQuery(id+"F4.opExtrude","SWEPT_EDGE",EDGE,{"disambiguationData":[OSD([subQ5,subQ0]),TDD([makeQuery(id+"F2.opExtrude","CAP_VERTEX",VERTEX,{"disambiguationData":[OSD([subQ5,subQ0])],"isStart":false})])]})]});Q0=makeQuery(id+"F15.boolean.opBoolean","COPY",FACE,{"derivedFrom":makeQuery(id+"F15.opExtrude","SWEPT_FACE",FACE,{"disambiguationData":[OSD([subQ5,subQ1,subQ2,subQ0]),TDD([makeQuery(id+"F10.opChamfer","BLEND_EDGE",EDGE,{"blendedFrom":[makeQuery(id+"F9.opExtrude","CAP_EDGE",EDGE,{"disambiguationData":[OSD([subQ1,subQ2,subQ0]),TDD([subQ4])],"isStart":false}),makeQuery(id+"F9.boolean.opBoolean","MERGE",FACE,{"derivedFrom":[makeQuery(id+"F7.boolean.opBoolean","MERGE",FACE,{"derivedFrom":[makeQuery(id+"F4.boolean.opBoolean","MERGE",FACE,{"derivedFrom":[makeQuery(id+"F3.boolean.opBoolean","MERGE",FACE,{"derivedFrom":[makeQuery(id+"F2.opExtrude","CAP_FACE",FACE,{"disambiguationData":[OSD([subQ5,subQ1,subQ2,subQ0])],"isStart":false}),makeQuery(id+"F3.opExtrude","SWEPT_FACE",FACE,{"disambiguationData":[OSD([subQ2]),TDD([makeQuery(id+"F2.opExtrude","CAP_EDGE",EDGE,{"disambiguationData":[OSD([subQ2])],"isStart":false})])]})]}),makeQuery(id+"F4.opExtrude","SWEPT_FACE",FACE,{"disambiguationData":[OSD([subQ0]),TDD([makeQuery(id+"F2.opExtrude","CAP_EDGE",EDGE,{"disambiguationData":[OSD([subQ0])],"isStart":false})])]})]}),makeQuery(id+"F7.opExtrude","SWEPT_FACE",FACE,{"disambiguationData":[OSD([subQ5,subQ2,subQ0]),TDD([makeQuery(id+"F5.imprint","IMPRINT",EDGE,{"disambiguationData":[TD([[makeQuery(id+"F5.imprint","INTERSECT",VERTEX,{"derivedFrom":[subQ6,sQuery(id+"F5.wireOp",EDGE,"E1"),sQuery(id+"F5.wireOp",EDGE,"E5")]}),1.0]])],"derivedFrom":subQ6})])]}),makeQuery(id+"F7.opExtrude","SWEPT_FACE",FACE,{"disambiguationData":[OSD([subQ5,subQ2,subQ0]),TDD([makeQuery(id+"F5.imprint","IMPRINT",EDGE,{"disambiguationData":[TD([[makeQuery(id+"F5.imprint","INTERSECT",VERTEX,{"derivedFrom":[subQ6,sQuery(id+"F5.wireOp",EDGE,"E8"),sQuery(id+"F5.wireOp",EDGE,"E9")]}),-1.0]])],"derivedFrom":subQ6})])]}),makeQuery(id+"F7.opExtrude","SWEPT_FACE",FACE,{"disambiguationData":[OSD([subQ5,subQ2,subQ0]),TDD([makeQuery(id+"F5.imprint","IMPRINT",EDGE,{"disambiguationData":[TD([[makeQuery(id+"F5.imprint","INTERSECT",VERTEX,{"derivedFrom":[subQ6,sQuery(id+"F5.wireOp",EDGE,"E13"),sQuery(id+"F5.wireOp",EDGE,"E14")]}),1.0]])],"derivedFrom":subQ6})])]})]}),makeQuery(id+"F9.opExtrude","SWEPT_FACE",FACE,{"disambiguationData":[OSD([subQ1,subQ2,subQ0]),TDD([makeQuery(id+"F6.imprint","IMPRINT",EDGE,{"disambiguationData":[TD([[makeQuery(id+"F6.imprint","INTERSECT",VERTEX,{"derivedFrom":[subQ3,sQuery(id+"F6.wireOp",EDGE,"E17"),sQuery(id+"F6.wireOp",EDGE,"E18")]}),-1.0]])],"derivedFrom":subQ3})])]}),makeQuery(id+"F9.opExtrude","SWEPT_FACE",FACE,{"disambiguationData":[OSD([subQ1,subQ2,subQ0]),TDD([makeQuery(id+"F6.imprint","IMPRINT",EDGE,{"disambiguationData":[TD([[makeQuery(id+"F6.imprint","INTERSECT",VERTEX,{"derivedFrom":[subQ3,sQuery(id+"F6.wireOp",EDGE,"E21"),sQuery(id+"F6.wireOp",EDGE,"E22")]}),1.0]])],"derivedFrom":subQ3})])]}),makeQuery(id+"F9.opExtrude","SWEPT_FACE",FACE,{"disambiguationData":[OSD([subQ1,subQ2,subQ0]),TDD([subQ4])]})]})],"blendedInto":[makeQuery(id+"F9.boolean.opBoolean","MERGE",FACE,{"derivedFrom":[makeQuery(id+"F7.boolean.opBoolean","MERGE",FACE,{"derivedFrom":[makeQuery(id+"F4.boolean.opBoolean","MERGE",FACE,{"derivedFrom":[makeQuery(id+"F3.boolean.opBoolean","MERGE",FACE,{"derivedFrom":[makeQuery(id+"F2.opExtrude","CAP_FACE",FACE,{"disambiguationData":[OSD([subQ5,subQ1,subQ2,subQ0])],"isStart":false}),makeQuery(id+"F3.opExtrude","SWEPT_FACE",FACE,{"disambiguationData":[OSD([subQ2]),TDD([makeQuery(id+"F2.opExtrude","CAP_EDGE",EDGE,{"disambiguationData":[OSD([subQ2])],"isStart":false})])]})]}),makeQuery(id+"F4.opExtrude","SWEPT_FACE",FACE,{"disambiguationData":[OSD([subQ0]),TDD([makeQuery(id+"F2.opExtrude","CAP_EDGE",EDGE,{"disambiguationData":[OSD([subQ0])],"isStart":false})])]})]}),makeQuery(id+"F7.opExtrude","SWEPT_FACE",FACE,{"disambiguationData":[OSD([subQ5,subQ2,subQ0]),TDD([makeQuery(id+"F5.imprint","IMPRINT",EDGE,{"disambiguationData":[TD([[makeQuery(id+"F5.imprint","INTERSECT",VERTEX,{"derivedFrom":[subQ6,sQuery(id+"F5.wireOp",EDGE,"E1"),sQuery(id+"F5.wireOp",EDGE,"E5")]}),1.0]])],"derivedFrom":subQ6})])]}),makeQuery(id+"F7.opExtrude","SWEPT_FACE",FACE,{"disambiguationData":[OSD([subQ5,subQ2,subQ0]),TDD([makeQuery(id+"F5.imprint","IMPRINT",EDGE,{"disambiguationData":[TD([[makeQuery(id+"F5.imprint","INTERSECT",VERTEX,{"derivedFrom":[subQ6,sQuery(id+"F5.wireOp",EDGE,"E8"),sQuery(id+"F5.wireOp",EDGE,"E9")]}),-1.0]])],"derivedFrom":subQ6})])]}),makeQuery(id+"F7.opExtrude","SWEPT_FACE",FACE,{"disambiguationData":[OSD([subQ5,subQ2,subQ0]),TDD([makeQuery(id+"F5.imprint","IMPRINT",EDGE,{"disambiguationData":[TD([[makeQuery(id+"F5.imprint","INTERSECT",VERTEX,{"derivedFrom":[subQ6,sQuery(id+"F5.wireOp",EDGE,"E13"),sQuery(id+"F5.wireOp",EDGE,"E14")]}),1.0]])],"derivedFrom":subQ6})])]})]}),makeQuery(id+"F9.opExtrude","SWEPT_FACE",FACE,{"disambiguationData":[OSD([subQ1,subQ2,subQ0]),TDD([makeQuery(id+"F6.imprint","IMPRINT",EDGE,{"disambiguationData":[TD([[makeQuery(id+"F6.imprint","INTERSECT",VERTEX,{"derivedFrom":[subQ3,sQuery(id+"F6.wireOp",EDGE,"E17"),sQuery(id+"F6.wireOp",EDGE,"E18")]}),-1.0]])],"derivedFrom":subQ3})])]}),makeQuery(id+"F9.opExtrude","SWEPT_FACE",FACE,{"disambiguationData":[OSD([subQ1,subQ2,subQ0]),TDD([makeQuery(id+"F6.imprint","IMPRINT",EDGE,{"disambiguationData":[TD([[makeQuery(id+"F6.imprint","INTERSECT",VERTEX,{"derivedFrom":[subQ3,sQuery(id+"F6.wireOp",EDGE,"E21"),sQuery(id+"F6.wireOp",EDGE,"E22")]}),1.0]])],"derivedFrom":subQ3})])]}),makeQuery(id+"F9.opExtrude","SWEPT_FACE",FACE,{"disambiguationData":[OSD([subQ1,subQ2,subQ0]),TDD([subQ4])]})]})]})])]})});}
            extrude(context, id + "F26", {"entities" : qUnion([Q0]), "operationType" : NewBodyOperationType.ADD, "depth" : 1.27 * mm, "offsetDistance" : 25.4 * mm});
        }
    });
